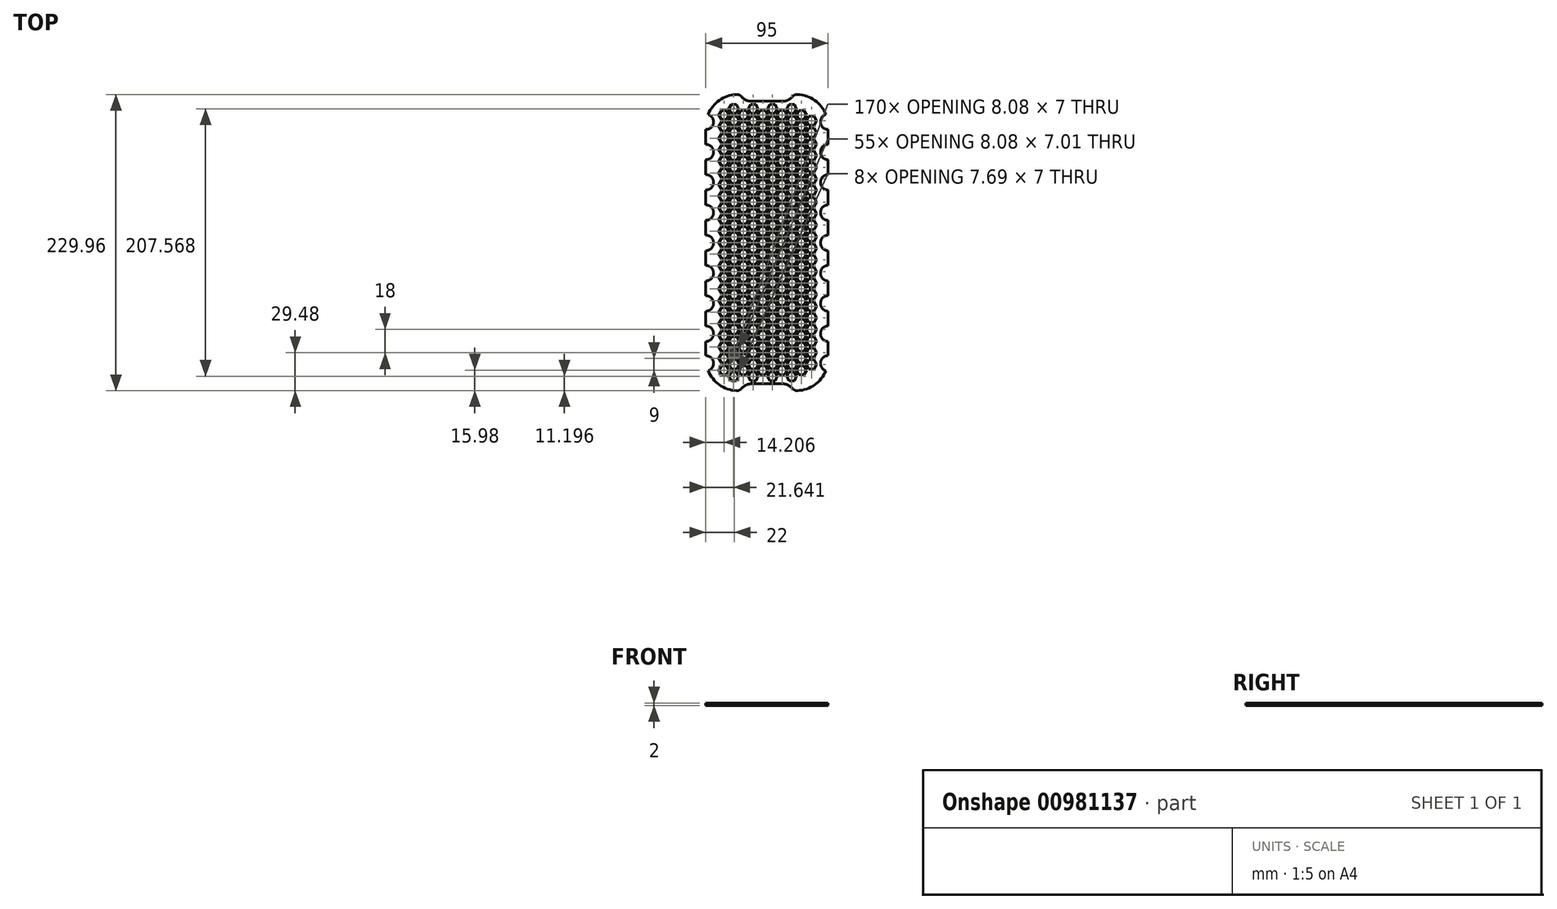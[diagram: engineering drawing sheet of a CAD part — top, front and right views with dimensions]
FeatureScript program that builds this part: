
annotation { "Feature Type Name" : "Feature", "Feature Type Description" : "" }
export const myFeature = defineFeature(function(context is Context, id is Id, definition is map)
    precondition{}
    {
        {
            var Q0;
            Q0=qCreatedBy(makeId("Top.planeOp"),FACE);
            var sketch = newSketch(context, id + "F0", { "sketchPlane" : qUnion([Q0])});
            skLineSegment(sketch, "E0.bottom", {"start": v(47.5, 115) * mm, "end": v(-47.5, 115) * mm});
            skLineSegment(sketch, "E0.top", {"start": v(47.5, -115) * mm, "end": v(-47.5, -115) * mm});
            skLineSegment(sketch, "E0.left", {"start": v(47.5, 115) * mm, "end": v(47.5, -115) * mm});
            skLineSegment(sketch, "E0.right", {"start": v(-47.5, 115) * mm, "end": v(-47.5, -115) * mm});
            skPoint(sketch, "E0.middle", {"position": v(0, 0) * mm});
            skSolve(sketch);
        }
        {
            var Q0;
            Q0 = qSketchRegion(id + "F0", true);
            extrude(context, id + "F1", {"entities" : qUnion([Q0]), "depth" : 2 * mm, "offsetDistance" : 25 * mm});
        }
        {
            var Q0;
            Q0=makeQuery(id+"F1.opExtrude","SWEPT_EDGE",EDGE,{"disambiguationData":[OSD([sQuery(id+"F0.wireOp",EDGE,"E0.top"),sQuery(id+"F0.wireOp",EDGE,"E0.right")])]});
            var Q1;
            Q1=makeQuery(id+"F1.opExtrude","SWEPT_EDGE",EDGE,{"disambiguationData":[OSD([sQuery(id+"F0.wireOp",EDGE,"E0.bottom"),sQuery(id+"F0.wireOp",EDGE,"E0.right")])]});
            var Q2;
            Q2=makeQuery(id+"F1.opExtrude","SWEPT_EDGE",EDGE,{"disambiguationData":[OSD([sQuery(id+"F0.wireOp",EDGE,"E0.bottom"),sQuery(id+"F0.wireOp",EDGE,"E0.left")])]});
            var Q3;
            Q3=makeQuery(id+"F1.opExtrude","SWEPT_EDGE",EDGE,{"disambiguationData":[OSD([sQuery(id+"F0.wireOp",EDGE,"E0.top"),sQuery(id+"F0.wireOp",EDGE,"E0.left")])]});
            fillet(context, id + "F2", {"entities" : qUnion([Q0, Q1, Q2, Q3]), "radius" : 25 * mm, "tangentPropagation" : true, "allowEdgeOverflow" : false});
        }
        {
            var Q0;
            Q0=qCreatedBy(makeId("Top.planeOp"),FACE);
            var sketch = newSketch(context, id + "F3", { "sketchPlane" : qUnion([Q0])});
            skCircle(sketch, "E1", {"center": v(-47.48, 93.75) * mm, "radius": 6 * mm});
            skCircle(sketch, "E2.MirrorC", {"center": v(47.48, 93.75) * mm, "radius": 6 * mm});
            skCircle(sketch, "E3.MirrorC", {"center": v(-47.48, -93.75) * mm, "radius": 6 * mm});
            skCircle(sketch, "E4.MirrorC", {"center": v(47.48, -93.75) * mm, "radius": 6 * mm});
            skCircle(sketch, "E5.0.1.0", {"center": v(-47.48, 70.25) * mm, "radius": 6 * mm});
            skLineSegment(sketch, "E5.direction1", {"start": v(-47.48, 93.75) * mm, "end": v(-47.48, 93.75) * mm});
            skLineSegment(sketch, "E5.direction2", {"start": v(-47.48, 93.75) * mm, "end": v(-47.48, 70.25) * mm, "construction": true});
            skCircle(sketch, "E6.0.0.2", {"center": v(-47.48, 46.75) * mm, "radius": 6 * mm});
            skCircle(sketch, "E6.0.0.3", {"center": v(-47.48, 23.25) * mm, "radius": 6 * mm});
            skCircle(sketch, "E7.0.0.4", {"center": v(-47.48, -0.25) * mm, "radius": 6 * mm});
            skCircle(sketch, "E8.0.0.5", {"center": v(-47.48, -23.75) * mm, "radius": 6 * mm});
            skCircle(sketch, "E9.0.0.6", {"center": v(-47.48, -47.25) * mm, "radius": 6 * mm});
            skCircle(sketch, "E10.MirrorC", {"center": v(47.48, 70.25) * mm, "radius": 6 * mm});
            skCircle(sketch, "E11.MirrorC", {"center": v(47.48, 46.75) * mm, "radius": 6 * mm});
            skCircle(sketch, "E12.MirrorC", {"center": v(47.48, 23.25) * mm, "radius": 6 * mm});
            skCircle(sketch, "E13.MirrorC", {"center": v(47.48, -0.25) * mm, "radius": 6 * mm});
            skCircle(sketch, "E14.MirrorC", {"center": v(47.48, -23.75) * mm, "radius": 6 * mm});
            skCircle(sketch, "E15.MirrorC", {"center": v(47.48, -47.25) * mm, "radius": 6 * mm});
            skCircle(sketch, "E16.MirrorC", {"center": v(47.48, -70.75) * mm, "radius": 6 * mm});
            skCircle(sketch, "E17.0.0.7", {"center": v(-47.48, -70.75) * mm, "radius": 6 * mm});
            skLineSegment(sketch, "E18.bottom", {"start": v(20.86, -109.66) * mm, "end": v(-20.86, -109.66) * mm});
            skLineSegment(sketch, "E18.top", {"start": v(20.86, -119.66) * mm, "end": v(-20.86, -119.66) * mm});
            skLineSegment(sketch, "E18.left", {"start": v(20.86, -109.66) * mm, "end": v(20.86, -119.66) * mm});
            skLineSegment(sketch, "E18.right", {"start": v(-20.86, -109.66) * mm, "end": v(-20.86, -119.66) * mm});
            skPoint(sketch, "E18.middle", {"position": v(0, -114.66) * mm});
            skLineSegment(sketch, "E19.MirrorCS", {"start": v(20.86, 119.66) * mm, "end": v(-20.86, 119.66) * mm});
            skLineSegment(sketch, "E20.MirrorCS", {"start": v(-20.86, 109.66) * mm, "end": v(-20.86, 119.66) * mm});
            skLineSegment(sketch, "E21.MirrorCS", {"start": v(20.86, 109.66) * mm, "end": v(-20.86, 109.66) * mm});
            skLineSegment(sketch, "E22.MirrorCS", {"start": v(20.86, 109.66) * mm, "end": v(20.86, 119.66) * mm});
            skSolve(sketch);
        }
        {
            var Q0;
            Q0 = qSketchRegion(id + "F3", true);
            extrude(context, id + "F4", {"entities" : qUnion([Q0]), "operationType" : NewBodyOperationType.REMOVE, "depth" : 10 * mm, "offsetDistance" : 25 * mm});
        }
        {
            var Q0;
            Q0=makeQuery(id+"F4.boolean.opBoolean","COPY",EDGE,{"derivedFrom":makeQuery(id+"F4.opExtrude","SWEPT_EDGE",EDGE,{"disambiguationData":[OSD([sQuery(id+"F3.wireOp",EDGE,"E18.bottom"),sQuery(id+"F3.wireOp",EDGE,"E18.right")])]})});
            var Q1;
            Q1=makeQuery(id+"F4.boolean.opBoolean","COPY",EDGE,{"derivedFrom":makeQuery(id+"F4.opExtrude","SWEPT_EDGE",EDGE,{"disambiguationData":[OSD([sQuery(id+"F3.wireOp",EDGE,"E18.bottom"),sQuery(id+"F3.wireOp",EDGE,"E18.left")])]})});
            var Q2;
            Q2=makeQuery(id+"F4.boolean.opBoolean","COPY",EDGE,{"derivedFrom":makeQuery(id+"F4.opExtrude","SWEPT_EDGE",EDGE,{"disambiguationData":[OSD([sQuery(id+"F3.wireOp",EDGE,"E20.MirrorCS"),sQuery(id+"F3.wireOp",EDGE,"E21.MirrorCS")])]})});
            var Q3;
            Q3=makeQuery(id+"F4.boolean.opBoolean","COPY",EDGE,{"derivedFrom":makeQuery(id+"F4.opExtrude","SWEPT_EDGE",EDGE,{"disambiguationData":[OSD([sQuery(id+"F3.wireOp",EDGE,"E21.MirrorCS"),sQuery(id+"F3.wireOp",EDGE,"E22.MirrorCS")])]})});
            fillet(context, id + "F5", {"entities" : qUnion([Q0, Q1, Q2, Q3]), "radius" : 10 * mm, "tangentPropagation" : true, "allowEdgeOverflow" : false});
        }
        {
            var Q0;
            {var subQ3=sQuery(id+"F0.wireOp",EDGE,"E0.bottom");var subQ4=sQuery(id+"F3.wireOp",EDGE,"E20.MirrorCS");Q0=makeQuery(id+"F5.opFillet","BLEND_EDGE",EDGE,{"blendedFrom":[makeQuery(id+"F4.boolean.opBoolean","COPY",EDGE,{"derivedFrom":makeQuery(id+"F4.opExtrude","SWEPT_EDGE",EDGE,{"disambiguationData":[OSD([subQ4,sQuery(id+"F3.wireOp",EDGE,"E21.MirrorCS")])]})}),makeQuery(id+"F4.boolean.opBoolean","SPLIT",FACE,{"disambiguationData":[TD([makeQuery(id+"F4.opExtrude","SWEPT_FACE",FACE,{"disambiguationData":[OSD([subQ4])]})])],"derivedFrom":makeQuery(id+"F1.opExtrude","SWEPT_FACE",FACE,{"disambiguationData":[OSD([subQ3])]})})],"blendedInto":[makeQuery(id+"F4.boolean.opBoolean","SPLIT",FACE,{"disambiguationData":[TD([makeQuery(id+"F4.opExtrude","SWEPT_FACE",FACE,{"disambiguationData":[OSD([subQ4])]})])],"derivedFrom":makeQuery(id+"F1.opExtrude","SWEPT_FACE",FACE,{"disambiguationData":[OSD([subQ3])]})})]});}
            var Q1;
            {var subQ3=sQuery(id+"F0.wireOp",EDGE,"E0.bottom");var subQ4=sQuery(id+"F3.wireOp",EDGE,"E22.MirrorCS");Q1=makeQuery(id+"F5.opFillet","BLEND_EDGE",EDGE,{"blendedFrom":[makeQuery(id+"F4.boolean.opBoolean","COPY",EDGE,{"derivedFrom":makeQuery(id+"F4.opExtrude","SWEPT_EDGE",EDGE,{"disambiguationData":[OSD([sQuery(id+"F3.wireOp",EDGE,"E21.MirrorCS"),subQ4])]})}),makeQuery(id+"F4.boolean.opBoolean","SPLIT",FACE,{"disambiguationData":[TD([makeQuery(id+"F4.opExtrude","SWEPT_FACE",FACE,{"disambiguationData":[OSD([subQ4])]})])],"derivedFrom":makeQuery(id+"F1.opExtrude","SWEPT_FACE",FACE,{"disambiguationData":[OSD([subQ3])]})})],"blendedInto":[makeQuery(id+"F4.boolean.opBoolean","SPLIT",FACE,{"disambiguationData":[TD([makeQuery(id+"F4.opExtrude","SWEPT_FACE",FACE,{"disambiguationData":[OSD([subQ4])]})])],"derivedFrom":makeQuery(id+"F1.opExtrude","SWEPT_FACE",FACE,{"disambiguationData":[OSD([subQ3])]})})]});}
            var Q2;
            {var subQ2=sQuery(id+"F0.wireOp",EDGE,"E0.top");var subQ4=sQuery(id+"F3.wireOp",EDGE,"E18.right");Q2=makeQuery(id+"F5.opFillet","BLEND_EDGE",EDGE,{"blendedFrom":[makeQuery(id+"F4.boolean.opBoolean","COPY",EDGE,{"derivedFrom":makeQuery(id+"F4.opExtrude","SWEPT_EDGE",EDGE,{"disambiguationData":[OSD([sQuery(id+"F3.wireOp",EDGE,"E18.bottom"),subQ4])]})}),makeQuery(id+"F4.boolean.opBoolean","SPLIT",FACE,{"disambiguationData":[TD([makeQuery(id+"F4.opExtrude","SWEPT_FACE",FACE,{"disambiguationData":[OSD([subQ4])]})])],"derivedFrom":makeQuery(id+"F1.opExtrude","SWEPT_FACE",FACE,{"disambiguationData":[OSD([subQ2])]})})],"blendedInto":[makeQuery(id+"F4.boolean.opBoolean","SPLIT",FACE,{"disambiguationData":[TD([makeQuery(id+"F4.opExtrude","SWEPT_FACE",FACE,{"disambiguationData":[OSD([subQ4])]})])],"derivedFrom":makeQuery(id+"F1.opExtrude","SWEPT_FACE",FACE,{"disambiguationData":[OSD([subQ2])]})})]});}
            var Q3;
            {var subQ2=sQuery(id+"F0.wireOp",EDGE,"E0.top");var subQ4=sQuery(id+"F3.wireOp",EDGE,"E18.left");Q3=makeQuery(id+"F5.opFillet","BLEND_EDGE",EDGE,{"blendedFrom":[makeQuery(id+"F4.boolean.opBoolean","COPY",EDGE,{"derivedFrom":makeQuery(id+"F4.opExtrude","SWEPT_EDGE",EDGE,{"disambiguationData":[OSD([sQuery(id+"F3.wireOp",EDGE,"E18.bottom"),subQ4])]})}),makeQuery(id+"F4.boolean.opBoolean","SPLIT",FACE,{"disambiguationData":[TD([makeQuery(id+"F4.opExtrude","SWEPT_FACE",FACE,{"disambiguationData":[OSD([subQ4])]})])],"derivedFrom":makeQuery(id+"F1.opExtrude","SWEPT_FACE",FACE,{"disambiguationData":[OSD([subQ2])]})})],"blendedInto":[makeQuery(id+"F4.boolean.opBoolean","SPLIT",FACE,{"disambiguationData":[TD([makeQuery(id+"F4.opExtrude","SWEPT_FACE",FACE,{"disambiguationData":[OSD([subQ4])]})])],"derivedFrom":makeQuery(id+"F1.opExtrude","SWEPT_FACE",FACE,{"disambiguationData":[OSD([subQ2])]})})]});}
            fillet(context, id + "F6", {"entities" : qUnion([Q0, Q1, Q2, Q3]), "radius" : 5 * mm, "tangentPropagation" : true, "allowEdgeOverflow" : false});
        }
        {
            var Q0;
            Q0=qCreatedBy(makeId("Top.planeOp"),FACE);
            var sketch = newSketch(context, id + "F7", { "sketchPlane" : qUnion([Q0])});
            skCircle(sketch, "E23.cCircle", {"center": v(34.5, -94.5) * mm, "radius": 3.5 * mm, "construction": true});
            skLineSegment(sketch, "E23.0", {"start": v(30.46, -94.5) * mm, "end": v(32.48, -91) * mm});
            skLineSegment(sketch, "E23.1", {"start": v(32.48, -91) * mm, "end": v(36.52, -91) * mm});
            skLineSegment(sketch, "E23.2", {"start": v(36.52, -91) * mm, "end": v(38.54, -94.5) * mm});
            skLineSegment(sketch, "E23.3", {"start": v(38.54, -94.5) * mm, "end": v(36.52, -98) * mm});
            skLineSegment(sketch, "E23.4", {"start": v(36.52, -98) * mm, "end": v(32.48, -98) * mm});
            skLineSegment(sketch, "E23.5", {"start": v(32.48, -98) * mm, "end": v(30.46, -94.5) * mm});
            skPoint(sketch, "E23.0.midPoint", {"position": v(31.47, -92.75) * mm});
            skCircle(sketch, "E24.cCircle", {"center": v(34.5, -85.5) * mm, "radius": 3.5 * mm, "construction": true});
            skLineSegment(sketch, "E24.0", {"start": v(30.46, -85.5) * mm, "end": v(32.47, -82) * mm});
            skLineSegment(sketch, "E24.1", {"start": v(32.47, -82) * mm, "end": v(36.51, -82) * mm});
            skLineSegment(sketch, "E24.2", {"start": v(36.51, -82) * mm, "end": v(38.54, -85.5) * mm});
            skLineSegment(sketch, "E24.3", {"start": v(38.54, -85.5) * mm, "end": v(36.53, -89) * mm});
            skLineSegment(sketch, "E24.4", {"start": v(36.53, -89) * mm, "end": v(32.49, -89) * mm});
            skLineSegment(sketch, "E24.5", {"start": v(32.49, -89) * mm, "end": v(30.46, -85.5) * mm});
            skPoint(sketch, "E24.0.midPoint", {"position": v(31.47, -83.76) * mm});
            skCircle(sketch, "E25.0.1.0", {"center": v(34.5, -76.5) * mm, "radius": 3.5 * mm, "construction": true});
            skPoint(sketch, "E25.0.1.1", {"position": v(31.47, -74.75) * mm});
            skLineSegment(sketch, "E25.0.1.2", {"start": v(36.52, -80) * mm, "end": v(32.48, -80) * mm});
            skCircle(sketch, "E25.0.1.3", {"center": v(34.5, -67.5) * mm, "radius": 3.5 * mm, "construction": true});
            skPoint(sketch, "E25.0.1.4", {"position": v(31.47, -65.76) * mm});
            skLineSegment(sketch, "E25.0.1.5", {"start": v(32.49, -71) * mm, "end": v(30.46, -67.5) * mm});
            skLineSegment(sketch, "E25.0.1.6", {"start": v(32.47, -64) * mm, "end": v(36.51, -64) * mm});
            skLineSegment(sketch, "E25.0.1.7", {"start": v(36.53, -71) * mm, "end": v(32.49, -71) * mm});
            skLineSegment(sketch, "E25.0.1.8", {"start": v(36.52, -73) * mm, "end": v(38.54, -76.5) * mm});
            skLineSegment(sketch, "E25.0.1.9", {"start": v(30.46, -76.5) * mm, "end": v(32.48, -73) * mm});
            skLineSegment(sketch, "E25.0.1.10", {"start": v(36.51, -64) * mm, "end": v(38.54, -67.5) * mm});
            skLineSegment(sketch, "E25.0.1.11", {"start": v(30.46, -67.5) * mm, "end": v(32.47, -64) * mm});
            skLineSegment(sketch, "E25.0.1.12", {"start": v(32.48, -80) * mm, "end": v(30.46, -76.5) * mm});
            skLineSegment(sketch, "E25.0.1.13", {"start": v(38.54, -76.5) * mm, "end": v(36.52, -80) * mm});
            skLineSegment(sketch, "E25.0.1.14", {"start": v(38.54, -67.5) * mm, "end": v(36.53, -71) * mm});
            skLineSegment(sketch, "E25.0.1.15", {"start": v(32.48, -73) * mm, "end": v(36.52, -73) * mm});
            skCircle(sketch, "E25.0.2.0", {"center": v(34.5, -58.5) * mm, "radius": 3.5 * mm, "construction": true});
            skPoint(sketch, "E25.0.2.1", {"position": v(31.47, -56.75) * mm});
            skLineSegment(sketch, "E25.0.2.2", {"start": v(36.52, -62) * mm, "end": v(32.48, -62) * mm});
            skCircle(sketch, "E25.0.2.3", {"center": v(34.5, -49.5) * mm, "radius": 3.5 * mm, "construction": true});
            skPoint(sketch, "E25.0.2.4", {"position": v(31.47, -47.76) * mm});
            skLineSegment(sketch, "E25.0.2.5", {"start": v(32.49, -53) * mm, "end": v(30.46, -49.5) * mm});
            skLineSegment(sketch, "E25.0.2.6", {"start": v(32.47, -46) * mm, "end": v(36.51, -46) * mm});
            skLineSegment(sketch, "E25.0.2.7", {"start": v(36.53, -53) * mm, "end": v(32.49, -53) * mm});
            skLineSegment(sketch, "E25.0.2.8", {"start": v(36.52, -55) * mm, "end": v(38.54, -58.5) * mm});
            skLineSegment(sketch, "E25.0.2.9", {"start": v(30.46, -58.5) * mm, "end": v(32.48, -55) * mm});
            skLineSegment(sketch, "E25.0.2.10", {"start": v(36.51, -46) * mm, "end": v(38.54, -49.5) * mm});
            skLineSegment(sketch, "E25.0.2.11", {"start": v(30.46, -49.5) * mm, "end": v(32.47, -46) * mm});
            skLineSegment(sketch, "E25.0.2.12", {"start": v(32.48, -62) * mm, "end": v(30.46, -58.5) * mm});
            skLineSegment(sketch, "E25.0.2.13", {"start": v(38.54, -58.5) * mm, "end": v(36.52, -62) * mm});
            skLineSegment(sketch, "E25.0.2.14", {"start": v(38.54, -49.5) * mm, "end": v(36.53, -53) * mm});
            skLineSegment(sketch, "E25.0.2.15", {"start": v(32.48, -55) * mm, "end": v(36.52, -55) * mm});
            skCircle(sketch, "E25.0.3.0", {"center": v(34.5, -40.5) * mm, "radius": 3.5 * mm, "construction": true});
            skPoint(sketch, "E25.0.3.1", {"position": v(31.47, -38.75) * mm});
            skLineSegment(sketch, "E25.0.3.2", {"start": v(36.52, -44) * mm, "end": v(32.48, -44) * mm});
            skCircle(sketch, "E25.0.3.3", {"center": v(34.5, -31.5) * mm, "radius": 3.5 * mm, "construction": true});
            skPoint(sketch, "E25.0.3.4", {"position": v(31.47, -29.76) * mm});
            skLineSegment(sketch, "E25.0.3.5", {"start": v(32.49, -35) * mm, "end": v(30.46, -31.5) * mm});
            skLineSegment(sketch, "E25.0.3.6", {"start": v(32.47, -28) * mm, "end": v(36.51, -28) * mm});
            skLineSegment(sketch, "E25.0.3.7", {"start": v(36.53, -35) * mm, "end": v(32.49, -35) * mm});
            skLineSegment(sketch, "E25.0.3.8", {"start": v(36.52, -37) * mm, "end": v(38.54, -40.5) * mm});
            skLineSegment(sketch, "E25.0.3.9", {"start": v(30.46, -40.5) * mm, "end": v(32.48, -37) * mm});
            skLineSegment(sketch, "E25.0.3.10", {"start": v(36.51, -28) * mm, "end": v(38.54, -31.5) * mm});
            skLineSegment(sketch, "E25.0.3.11", {"start": v(30.46, -31.5) * mm, "end": v(32.47, -28) * mm});
            skLineSegment(sketch, "E25.0.3.12", {"start": v(32.48, -44) * mm, "end": v(30.46, -40.5) * mm});
            skLineSegment(sketch, "E25.0.3.13", {"start": v(38.54, -40.5) * mm, "end": v(36.52, -44) * mm});
            skLineSegment(sketch, "E25.0.3.14", {"start": v(38.54, -31.5) * mm, "end": v(36.53, -35) * mm});
            skLineSegment(sketch, "E25.0.3.15", {"start": v(32.48, -37) * mm, "end": v(36.52, -37) * mm});
            skCircle(sketch, "E25.0.4.0", {"center": v(34.5, -22.5) * mm, "radius": 3.5 * mm, "construction": true});
            skPoint(sketch, "E25.0.4.1", {"position": v(31.47, -20.75) * mm});
            skLineSegment(sketch, "E25.0.4.2", {"start": v(36.52, -26) * mm, "end": v(32.48, -26) * mm});
            skCircle(sketch, "E25.0.4.3", {"center": v(34.5, -13.5) * mm, "radius": 3.5 * mm, "construction": true});
            skPoint(sketch, "E25.0.4.4", {"position": v(31.47, -11.76) * mm});
            skLineSegment(sketch, "E25.0.4.5", {"start": v(32.49, -17) * mm, "end": v(30.46, -13.5) * mm});
            skLineSegment(sketch, "E25.0.4.6", {"start": v(32.47, -10) * mm, "end": v(36.51, -10) * mm});
            skLineSegment(sketch, "E25.0.4.7", {"start": v(36.53, -17) * mm, "end": v(32.49, -17) * mm});
            skLineSegment(sketch, "E25.0.4.8", {"start": v(36.52, -19) * mm, "end": v(38.54, -22.5) * mm});
            skLineSegment(sketch, "E25.0.4.9", {"start": v(30.46, -22.5) * mm, "end": v(32.48, -19) * mm});
            skLineSegment(sketch, "E25.0.4.10", {"start": v(36.51, -10) * mm, "end": v(38.54, -13.5) * mm});
            skLineSegment(sketch, "E25.0.4.11", {"start": v(30.46, -13.5) * mm, "end": v(32.47, -10) * mm});
            skLineSegment(sketch, "E25.0.4.12", {"start": v(32.48, -26) * mm, "end": v(30.46, -22.5) * mm});
            skLineSegment(sketch, "E25.0.4.13", {"start": v(38.54, -22.5) * mm, "end": v(36.52, -26) * mm});
            skLineSegment(sketch, "E25.0.4.14", {"start": v(38.54, -13.5) * mm, "end": v(36.53, -17) * mm});
            skLineSegment(sketch, "E25.0.4.15", {"start": v(32.48, -19) * mm, "end": v(36.52, -19) * mm});
            skCircle(sketch, "E25.0.5.0", {"center": v(34.5, -4.5) * mm, "radius": 3.5 * mm, "construction": true});
            skPoint(sketch, "E25.0.5.1", {"position": v(31.47, -2.75) * mm});
            skLineSegment(sketch, "E25.0.5.2", {"start": v(36.52, -8) * mm, "end": v(32.48, -8) * mm});
            skCircle(sketch, "E25.0.5.3", {"center": v(34.5, 4.5) * mm, "radius": 3.5 * mm, "construction": true});
            skPoint(sketch, "E25.0.5.4", {"position": v(31.47, 6.24) * mm});
            skLineSegment(sketch, "E25.0.5.5", {"start": v(32.49, 1) * mm, "end": v(30.46, 4.5) * mm});
            skLineSegment(sketch, "E25.0.5.6", {"start": v(32.47, 8) * mm, "end": v(36.51, 8) * mm});
            skLineSegment(sketch, "E25.0.5.7", {"start": v(36.53, 1) * mm, "end": v(32.49, 1) * mm});
            skLineSegment(sketch, "E25.0.5.8", {"start": v(36.52, -1) * mm, "end": v(38.54, -4.5) * mm});
            skLineSegment(sketch, "E25.0.5.9", {"start": v(30.46, -4.5) * mm, "end": v(32.48, -1) * mm});
            skLineSegment(sketch, "E25.0.5.10", {"start": v(36.51, 8) * mm, "end": v(38.54, 4.5) * mm});
            skLineSegment(sketch, "E25.0.5.11", {"start": v(30.46, 4.5) * mm, "end": v(32.47, 8) * mm});
            skLineSegment(sketch, "E25.0.5.12", {"start": v(32.48, -8) * mm, "end": v(30.46, -4.5) * mm});
            skLineSegment(sketch, "E25.0.5.13", {"start": v(38.54, -4.5) * mm, "end": v(36.52, -8) * mm});
            skLineSegment(sketch, "E25.0.5.14", {"start": v(38.54, 4.5) * mm, "end": v(36.53, 1) * mm});
            skLineSegment(sketch, "E25.0.5.15", {"start": v(32.48, -1) * mm, "end": v(36.52, -1) * mm});
            skCircle(sketch, "E25.0.6.0", {"center": v(34.5, 13.5) * mm, "radius": 3.5 * mm, "construction": true});
            skPoint(sketch, "E25.0.6.1", {"position": v(31.47, 15.25) * mm});
            skLineSegment(sketch, "E25.0.6.2", {"start": v(36.52, 10) * mm, "end": v(32.48, 10) * mm});
            skCircle(sketch, "E25.0.6.3", {"center": v(34.5, 22.5) * mm, "radius": 3.5 * mm, "construction": true});
            skPoint(sketch, "E25.0.6.4", {"position": v(31.47, 24.24) * mm});
            skLineSegment(sketch, "E25.0.6.5", {"start": v(32.49, 19) * mm, "end": v(30.46, 22.5) * mm});
            skLineSegment(sketch, "E25.0.6.6", {"start": v(32.47, 26) * mm, "end": v(36.51, 26) * mm});
            skLineSegment(sketch, "E25.0.6.7", {"start": v(36.53, 19) * mm, "end": v(32.49, 19) * mm});
            skLineSegment(sketch, "E25.0.6.8", {"start": v(36.52, 17) * mm, "end": v(38.54, 13.5) * mm});
            skLineSegment(sketch, "E25.0.6.9", {"start": v(30.46, 13.5) * mm, "end": v(32.48, 17) * mm});
            skLineSegment(sketch, "E25.0.6.10", {"start": v(36.51, 26) * mm, "end": v(38.54, 22.5) * mm});
            skLineSegment(sketch, "E25.0.6.11", {"start": v(30.46, 22.5) * mm, "end": v(32.47, 26) * mm});
            skLineSegment(sketch, "E25.0.6.12", {"start": v(32.48, 10) * mm, "end": v(30.46, 13.5) * mm});
            skLineSegment(sketch, "E25.0.6.13", {"start": v(38.54, 13.5) * mm, "end": v(36.52, 10) * mm});
            skLineSegment(sketch, "E25.0.6.14", {"start": v(38.54, 22.5) * mm, "end": v(36.53, 19) * mm});
            skLineSegment(sketch, "E25.0.6.15", {"start": v(32.48, 17) * mm, "end": v(36.52, 17) * mm});
            skCircle(sketch, "E25.0.7.0", {"center": v(34.5, 31.5) * mm, "radius": 3.5 * mm, "construction": true});
            skPoint(sketch, "E25.0.7.1", {"position": v(31.47, 33.25) * mm});
            skLineSegment(sketch, "E25.0.7.2", {"start": v(36.52, 28) * mm, "end": v(32.48, 28) * mm});
            skCircle(sketch, "E25.0.7.3", {"center": v(34.5, 40.5) * mm, "radius": 3.5 * mm, "construction": true});
            skPoint(sketch, "E25.0.7.4", {"position": v(31.47, 42.24) * mm});
            skLineSegment(sketch, "E25.0.7.5", {"start": v(32.49, 37) * mm, "end": v(30.46, 40.5) * mm});
            skLineSegment(sketch, "E25.0.7.6", {"start": v(32.47, 44) * mm, "end": v(36.51, 44) * mm});
            skLineSegment(sketch, "E25.0.7.7", {"start": v(36.53, 37) * mm, "end": v(32.49, 37) * mm});
            skLineSegment(sketch, "E25.0.7.8", {"start": v(36.52, 35) * mm, "end": v(38.54, 31.5) * mm});
            skLineSegment(sketch, "E25.0.7.9", {"start": v(30.46, 31.5) * mm, "end": v(32.48, 35) * mm});
            skLineSegment(sketch, "E25.0.7.10", {"start": v(36.51, 44) * mm, "end": v(38.54, 40.5) * mm});
            skLineSegment(sketch, "E25.0.7.11", {"start": v(30.46, 40.5) * mm, "end": v(32.47, 44) * mm});
            skLineSegment(sketch, "E25.0.7.12", {"start": v(32.48, 28) * mm, "end": v(30.46, 31.5) * mm});
            skLineSegment(sketch, "E25.0.7.13", {"start": v(38.54, 31.5) * mm, "end": v(36.52, 28) * mm});
            skLineSegment(sketch, "E25.0.7.14", {"start": v(38.54, 40.5) * mm, "end": v(36.53, 37) * mm});
            skLineSegment(sketch, "E25.0.7.15", {"start": v(32.48, 35) * mm, "end": v(36.52, 35) * mm});
            skCircle(sketch, "E25.0.8.0", {"center": v(34.5, 49.5) * mm, "radius": 3.5 * mm, "construction": true});
            skPoint(sketch, "E25.0.8.1", {"position": v(31.47, 51.25) * mm});
            skLineSegment(sketch, "E25.0.8.2", {"start": v(36.52, 46) * mm, "end": v(32.48, 46) * mm});
            skCircle(sketch, "E25.0.8.3", {"center": v(34.5, 58.5) * mm, "radius": 3.5 * mm, "construction": true});
            skPoint(sketch, "E25.0.8.4", {"position": v(31.47, 60.24) * mm});
            skLineSegment(sketch, "E25.0.8.5", {"start": v(32.49, 55) * mm, "end": v(30.46, 58.5) * mm});
            skLineSegment(sketch, "E25.0.8.6", {"start": v(32.47, 62) * mm, "end": v(36.51, 62) * mm});
            skLineSegment(sketch, "E25.0.8.7", {"start": v(36.53, 55) * mm, "end": v(32.49, 55) * mm});
            skLineSegment(sketch, "E25.0.8.8", {"start": v(36.52, 53) * mm, "end": v(38.54, 49.5) * mm});
            skLineSegment(sketch, "E25.0.8.9", {"start": v(30.46, 49.5) * mm, "end": v(32.48, 53) * mm});
            skLineSegment(sketch, "E25.0.8.10", {"start": v(36.51, 62) * mm, "end": v(38.54, 58.5) * mm});
            skLineSegment(sketch, "E25.0.8.11", {"start": v(30.46, 58.5) * mm, "end": v(32.47, 62) * mm});
            skLineSegment(sketch, "E25.0.8.12", {"start": v(32.48, 46) * mm, "end": v(30.46, 49.5) * mm});
            skLineSegment(sketch, "E25.0.8.13", {"start": v(38.54, 49.5) * mm, "end": v(36.52, 46) * mm});
            skLineSegment(sketch, "E25.0.8.14", {"start": v(38.54, 58.5) * mm, "end": v(36.53, 55) * mm});
            skLineSegment(sketch, "E25.0.8.15", {"start": v(32.48, 53) * mm, "end": v(36.52, 53) * mm});
            skCircle(sketch, "E25.0.9.0", {"center": v(34.5, 67.5) * mm, "radius": 3.5 * mm, "construction": true});
            skPoint(sketch, "E25.0.9.1", {"position": v(31.47, 69.25) * mm});
            skLineSegment(sketch, "E25.0.9.2", {"start": v(36.52, 64) * mm, "end": v(32.48, 64) * mm});
            skCircle(sketch, "E25.0.9.3", {"center": v(34.5, 76.5) * mm, "radius": 3.5 * mm, "construction": true});
            skPoint(sketch, "E25.0.9.4", {"position": v(31.47, 78.24) * mm});
            skLineSegment(sketch, "E25.0.9.5", {"start": v(32.49, 73) * mm, "end": v(30.46, 76.5) * mm});
            skLineSegment(sketch, "E25.0.9.6", {"start": v(32.47, 80) * mm, "end": v(36.51, 80) * mm});
            skLineSegment(sketch, "E25.0.9.7", {"start": v(36.53, 73) * mm, "end": v(32.49, 73) * mm});
            skLineSegment(sketch, "E25.0.9.8", {"start": v(36.52, 71) * mm, "end": v(38.54, 67.5) * mm});
            skLineSegment(sketch, "E25.0.9.9", {"start": v(30.46, 67.5) * mm, "end": v(32.48, 71) * mm});
            skLineSegment(sketch, "E25.0.9.10", {"start": v(36.51, 80) * mm, "end": v(38.54, 76.5) * mm});
            skLineSegment(sketch, "E25.0.9.11", {"start": v(30.46, 76.5) * mm, "end": v(32.47, 80) * mm});
            skLineSegment(sketch, "E25.0.9.12", {"start": v(32.48, 64) * mm, "end": v(30.46, 67.5) * mm});
            skLineSegment(sketch, "E25.0.9.13", {"start": v(38.54, 67.5) * mm, "end": v(36.52, 64) * mm});
            skLineSegment(sketch, "E25.0.9.14", {"start": v(38.54, 76.5) * mm, "end": v(36.53, 73) * mm});
            skLineSegment(sketch, "E25.0.9.15", {"start": v(32.48, 71) * mm, "end": v(36.52, 71) * mm});
            skCircle(sketch, "E25.0.10.0", {"center": v(34.5, 85.5) * mm, "radius": 3.5 * mm, "construction": true});
            skPoint(sketch, "E25.0.10.1", {"position": v(31.47, 87.25) * mm});
            skLineSegment(sketch, "E25.0.10.2", {"start": v(36.52, 82) * mm, "end": v(32.48, 82) * mm});
            skCircle(sketch, "E25.0.10.3", {"center": v(34.5, 94.5) * mm, "radius": 3.5 * mm, "construction": true});
            skPoint(sketch, "E25.0.10.4", {"position": v(31.47, 96.24) * mm});
            skLineSegment(sketch, "E25.0.10.5", {"start": v(32.49, 91) * mm, "end": v(30.46, 94.5) * mm});
            skLineSegment(sketch, "E25.0.10.6", {"start": v(32.47, 98) * mm, "end": v(36.51, 98) * mm});
            skLineSegment(sketch, "E25.0.10.7", {"start": v(36.53, 91) * mm, "end": v(32.49, 91) * mm});
            skLineSegment(sketch, "E25.0.10.8", {"start": v(36.52, 89) * mm, "end": v(38.54, 85.5) * mm});
            skLineSegment(sketch, "E25.0.10.9", {"start": v(30.46, 85.5) * mm, "end": v(32.48, 89) * mm});
            skLineSegment(sketch, "E25.0.10.10", {"start": v(36.51, 98) * mm, "end": v(38.54, 94.5) * mm});
            skLineSegment(sketch, "E25.0.10.11", {"start": v(30.46, 94.5) * mm, "end": v(32.47, 98) * mm});
            skLineSegment(sketch, "E25.0.10.12", {"start": v(32.48, 82) * mm, "end": v(30.46, 85.5) * mm});
            skLineSegment(sketch, "E25.0.10.13", {"start": v(38.54, 85.5) * mm, "end": v(36.52, 82) * mm});
            skLineSegment(sketch, "E25.0.10.14", {"start": v(38.54, 94.5) * mm, "end": v(36.53, 91) * mm});
            skLineSegment(sketch, "E25.0.10.15", {"start": v(32.48, 89) * mm, "end": v(36.52, 89) * mm});
            skLineSegment(sketch, "E25.direction1", {"start": v(32.48, -98) * mm, "end": v(57.3, -98) * mm, "construction": true});
            skLineSegment(sketch, "E25.direction2", {"start": v(32.48, -98) * mm, "end": v(32.48, -80) * mm, "construction": true});
            skCircle(sketch, "E26.cCircle", {"center": v(26.7, -99) * mm, "radius": 3.5 * mm, "construction": true});
            skLineSegment(sketch, "E26.0", {"start": v(24.69, -95.5) * mm, "end": v(28.73, -95.5) * mm});
            skLineSegment(sketch, "E26.1", {"start": v(28.73, -95.5) * mm, "end": v(30.75, -99) * mm});
            skLineSegment(sketch, "E26.2", {"start": v(30.75, -99) * mm, "end": v(28.73, -102.5) * mm});
            skLineSegment(sketch, "E26.3", {"start": v(28.73, -102.5) * mm, "end": v(24.69, -102.5) * mm});
            skLineSegment(sketch, "E26.4", {"start": v(24.69, -102.5) * mm, "end": v(22.66, -99) * mm});
            skLineSegment(sketch, "E26.5", {"start": v(22.66, -99) * mm, "end": v(24.69, -95.5) * mm});
            skPoint(sketch, "E26.0.midPoint", {"position": v(26.7, -95.5) * mm});
            skLineSegment(sketch, "E27.0.1.0", {"start": v(30.75, -90) * mm, "end": v(28.73, -93.5) * mm});
            skLineSegment(sketch, "E27.0.1.1", {"start": v(28.73, -93.5) * mm, "end": v(24.69, -93.5) * mm});
            skLineSegment(sketch, "E27.0.1.2", {"start": v(24.69, -86.5) * mm, "end": v(28.73, -86.5) * mm});
            skLineSegment(sketch, "E27.0.1.3", {"start": v(22.66, -90) * mm, "end": v(24.69, -86.5) * mm});
            skLineSegment(sketch, "E27.0.1.4", {"start": v(24.69, -93.5) * mm, "end": v(22.66, -90) * mm});
            skLineSegment(sketch, "E27.0.1.5", {"start": v(28.73, -86.5) * mm, "end": v(30.75, -90) * mm});
            skCircle(sketch, "E27.0.1.6", {"center": v(26.7, -90) * mm, "radius": 3.5 * mm, "construction": true});
            skLineSegment(sketch, "E27.0.2.0", {"start": v(30.75, -81) * mm, "end": v(28.73, -84.5) * mm});
            skLineSegment(sketch, "E27.0.2.1", {"start": v(28.73, -84.5) * mm, "end": v(24.69, -84.5) * mm});
            skLineSegment(sketch, "E27.0.2.2", {"start": v(24.69, -77.5) * mm, "end": v(28.73, -77.5) * mm});
            skLineSegment(sketch, "E27.0.2.3", {"start": v(22.66, -81) * mm, "end": v(24.69, -77.5) * mm});
            skLineSegment(sketch, "E27.0.2.4", {"start": v(24.69, -84.5) * mm, "end": v(22.66, -81) * mm});
            skLineSegment(sketch, "E27.0.2.5", {"start": v(28.73, -77.5) * mm, "end": v(30.75, -81) * mm});
            skCircle(sketch, "E27.0.2.6", {"center": v(26.7, -81) * mm, "radius": 3.5 * mm, "construction": true});
            skLineSegment(sketch, "E27.0.3.0", {"start": v(30.75, -72) * mm, "end": v(28.73, -75.5) * mm});
            skLineSegment(sketch, "E27.0.3.1", {"start": v(28.73, -75.5) * mm, "end": v(24.69, -75.5) * mm});
            skLineSegment(sketch, "E27.0.3.2", {"start": v(24.69, -68.5) * mm, "end": v(28.73, -68.5) * mm});
            skLineSegment(sketch, "E27.0.3.3", {"start": v(22.66, -72) * mm, "end": v(24.69, -68.5) * mm});
            skLineSegment(sketch, "E27.0.3.4", {"start": v(24.69, -75.5) * mm, "end": v(22.66, -72) * mm});
            skLineSegment(sketch, "E27.0.3.5", {"start": v(28.73, -68.5) * mm, "end": v(30.75, -72) * mm});
            skCircle(sketch, "E27.0.3.6", {"center": v(26.7, -72) * mm, "radius": 3.5 * mm, "construction": true});
            skLineSegment(sketch, "E27.0.4.0", {"start": v(30.75, -63) * mm, "end": v(28.73, -66.5) * mm});
            skLineSegment(sketch, "E27.0.4.1", {"start": v(28.73, -66.5) * mm, "end": v(24.69, -66.5) * mm});
            skLineSegment(sketch, "E27.0.4.2", {"start": v(24.69, -59.5) * mm, "end": v(28.73, -59.5) * mm});
            skLineSegment(sketch, "E27.0.4.3", {"start": v(22.66, -63) * mm, "end": v(24.69, -59.5) * mm});
            skLineSegment(sketch, "E27.0.4.4", {"start": v(24.69, -66.5) * mm, "end": v(22.66, -63) * mm});
            skLineSegment(sketch, "E27.0.4.5", {"start": v(28.73, -59.5) * mm, "end": v(30.75, -63) * mm});
            skCircle(sketch, "E27.0.4.6", {"center": v(26.7, -63) * mm, "radius": 3.5 * mm, "construction": true});
            skLineSegment(sketch, "E27.0.5.0", {"start": v(30.75, -54) * mm, "end": v(28.73, -57.5) * mm});
            skLineSegment(sketch, "E27.0.5.1", {"start": v(28.73, -57.5) * mm, "end": v(24.69, -57.5) * mm});
            skLineSegment(sketch, "E27.0.5.2", {"start": v(24.69, -50.5) * mm, "end": v(28.73, -50.5) * mm});
            skLineSegment(sketch, "E27.0.5.3", {"start": v(22.66, -54) * mm, "end": v(24.69, -50.5) * mm});
            skLineSegment(sketch, "E27.0.5.4", {"start": v(24.69, -57.5) * mm, "end": v(22.66, -54) * mm});
            skLineSegment(sketch, "E27.0.5.5", {"start": v(28.73, -50.5) * mm, "end": v(30.75, -54) * mm});
            skCircle(sketch, "E27.0.5.6", {"center": v(26.7, -54) * mm, "radius": 3.5 * mm, "construction": true});
            skLineSegment(sketch, "E27.0.6.0", {"start": v(30.75, -45) * mm, "end": v(28.73, -48.5) * mm});
            skLineSegment(sketch, "E27.0.6.1", {"start": v(28.73, -48.5) * mm, "end": v(24.69, -48.5) * mm});
            skLineSegment(sketch, "E27.0.6.2", {"start": v(24.69, -41.5) * mm, "end": v(28.73, -41.5) * mm});
            skLineSegment(sketch, "E27.0.6.3", {"start": v(22.66, -45) * mm, "end": v(24.69, -41.5) * mm});
            skLineSegment(sketch, "E27.0.6.4", {"start": v(24.69, -48.5) * mm, "end": v(22.66, -45) * mm});
            skLineSegment(sketch, "E27.0.6.5", {"start": v(28.73, -41.5) * mm, "end": v(30.75, -45) * mm});
            skCircle(sketch, "E27.0.6.6", {"center": v(26.7, -45) * mm, "radius": 3.5 * mm, "construction": true});
            skLineSegment(sketch, "E27.0.7.0", {"start": v(30.75, -36) * mm, "end": v(28.73, -39.5) * mm});
            skLineSegment(sketch, "E27.0.7.1", {"start": v(28.73, -39.5) * mm, "end": v(24.69, -39.5) * mm});
            skLineSegment(sketch, "E27.0.7.2", {"start": v(24.69, -32.5) * mm, "end": v(28.73, -32.5) * mm});
            skLineSegment(sketch, "E27.0.7.3", {"start": v(22.66, -36) * mm, "end": v(24.69, -32.5) * mm});
            skLineSegment(sketch, "E27.0.7.4", {"start": v(24.69, -39.5) * mm, "end": v(22.66, -36) * mm});
            skLineSegment(sketch, "E27.0.7.5", {"start": v(28.73, -32.5) * mm, "end": v(30.75, -36) * mm});
            skCircle(sketch, "E27.0.7.6", {"center": v(26.7, -36) * mm, "radius": 3.5 * mm, "construction": true});
            skLineSegment(sketch, "E27.0.8.0", {"start": v(30.75, -27) * mm, "end": v(28.73, -30.5) * mm});
            skLineSegment(sketch, "E27.0.8.1", {"start": v(28.73, -30.5) * mm, "end": v(24.69, -30.5) * mm});
            skLineSegment(sketch, "E27.0.8.2", {"start": v(24.69, -23.5) * mm, "end": v(28.73, -23.5) * mm});
            skLineSegment(sketch, "E27.0.8.3", {"start": v(22.66, -27) * mm, "end": v(24.69, -23.5) * mm});
            skLineSegment(sketch, "E27.0.8.4", {"start": v(24.69, -30.5) * mm, "end": v(22.66, -27) * mm});
            skLineSegment(sketch, "E27.0.8.5", {"start": v(28.73, -23.5) * mm, "end": v(30.75, -27) * mm});
            skCircle(sketch, "E27.0.8.6", {"center": v(26.7, -27) * mm, "radius": 3.5 * mm, "construction": true});
            skLineSegment(sketch, "E27.0.9.0", {"start": v(30.75, -18) * mm, "end": v(28.73, -21.5) * mm});
            skLineSegment(sketch, "E27.0.9.1", {"start": v(28.73, -21.5) * mm, "end": v(24.69, -21.5) * mm});
            skLineSegment(sketch, "E27.0.9.2", {"start": v(24.69, -14.5) * mm, "end": v(28.73, -14.5) * mm});
            skLineSegment(sketch, "E27.0.9.3", {"start": v(22.66, -18) * mm, "end": v(24.69, -14.5) * mm});
            skLineSegment(sketch, "E27.0.9.4", {"start": v(24.69, -21.5) * mm, "end": v(22.66, -18) * mm});
            skLineSegment(sketch, "E27.0.9.5", {"start": v(28.73, -14.5) * mm, "end": v(30.75, -18) * mm});
            skCircle(sketch, "E27.0.9.6", {"center": v(26.7, -18) * mm, "radius": 3.5 * mm, "construction": true});
            skLineSegment(sketch, "E27.0.10.0", {"start": v(30.75, -9) * mm, "end": v(28.73, -12.5) * mm});
            skLineSegment(sketch, "E27.0.10.1", {"start": v(28.73, -12.5) * mm, "end": v(24.69, -12.5) * mm});
            skLineSegment(sketch, "E27.0.10.2", {"start": v(24.69, -5.5) * mm, "end": v(28.73, -5.5) * mm});
            skLineSegment(sketch, "E27.0.10.3", {"start": v(22.66, -9) * mm, "end": v(24.69, -5.5) * mm});
            skLineSegment(sketch, "E27.0.10.4", {"start": v(24.69, -12.5) * mm, "end": v(22.66, -9) * mm});
            skLineSegment(sketch, "E27.0.10.5", {"start": v(28.73, -5.5) * mm, "end": v(30.75, -9) * mm});
            skCircle(sketch, "E27.0.10.6", {"center": v(26.7, -9) * mm, "radius": 3.5 * mm, "construction": true});
            skLineSegment(sketch, "E27.0.11.0", {"start": v(30.75, 0) * mm, "end": v(28.73, -3.5) * mm});
            skLineSegment(sketch, "E27.0.11.1", {"start": v(28.73, -3.5) * mm, "end": v(24.69, -3.5) * mm});
            skLineSegment(sketch, "E27.0.11.2", {"start": v(24.69, 3.5) * mm, "end": v(28.73, 3.5) * mm});
            skLineSegment(sketch, "E27.0.11.3", {"start": v(22.66, 0) * mm, "end": v(24.69, 3.5) * mm});
            skLineSegment(sketch, "E27.0.11.4", {"start": v(24.69, -3.5) * mm, "end": v(22.66, 0) * mm});
            skLineSegment(sketch, "E27.0.11.5", {"start": v(28.73, 3.5) * mm, "end": v(30.75, 0) * mm});
            skCircle(sketch, "E27.0.11.6", {"center": v(26.7, 0) * mm, "radius": 3.5 * mm, "construction": true});
            skLineSegment(sketch, "E27.direction1", {"start": v(24.69, -102.5) * mm, "end": v(49.69, -102.5) * mm, "construction": true});
            skLineSegment(sketch, "E27.direction2", {"start": v(24.69, -102.5) * mm, "end": v(24.69, -93.5) * mm, "construction": true});
            skLineSegment(sketch, "E28.0.0.12", {"start": v(30.75, 9) * mm, "end": v(28.73, 5.5) * mm});
            skLineSegment(sketch, "E28.3.0.12", {"start": v(28.73, 5.5) * mm, "end": v(24.69, 5.5) * mm});
            skLineSegment(sketch, "E28.6.0.12", {"start": v(24.69, 12.5) * mm, "end": v(28.73, 12.5) * mm});
            skLineSegment(sketch, "E28.9.0.12", {"start": v(22.66, 9) * mm, "end": v(24.69, 12.5) * mm});
            skLineSegment(sketch, "E28.12.0.12", {"start": v(24.69, 5.5) * mm, "end": v(22.66, 9) * mm});
            skLineSegment(sketch, "E28.15.0.12", {"start": v(28.73, 12.5) * mm, "end": v(30.75, 9) * mm});
            skCircle(sketch, "E28.18.0.12", {"center": v(26.7, 9) * mm, "radius": 3.5 * mm, "construction": true});
            skLineSegment(sketch, "E28.0.0.13", {"start": v(30.75, 18) * mm, "end": v(28.73, 14.5) * mm});
            skLineSegment(sketch, "E28.3.0.13", {"start": v(28.73, 14.5) * mm, "end": v(24.69, 14.5) * mm});
            skLineSegment(sketch, "E28.6.0.13", {"start": v(24.69, 21.5) * mm, "end": v(28.73, 21.5) * mm});
            skLineSegment(sketch, "E28.9.0.13", {"start": v(22.66, 18) * mm, "end": v(24.69, 21.5) * mm});
            skLineSegment(sketch, "E28.12.0.13", {"start": v(24.69, 14.5) * mm, "end": v(22.66, 18) * mm});
            skLineSegment(sketch, "E28.15.0.13", {"start": v(28.73, 21.5) * mm, "end": v(30.75, 18) * mm});
            skCircle(sketch, "E28.18.0.13", {"center": v(26.7, 18) * mm, "radius": 3.5 * mm, "construction": true});
            skLineSegment(sketch, "E28.0.0.14", {"start": v(30.75, 27) * mm, "end": v(28.73, 23.5) * mm});
            skLineSegment(sketch, "E28.3.0.14", {"start": v(28.73, 23.5) * mm, "end": v(24.69, 23.5) * mm});
            skLineSegment(sketch, "E28.6.0.14", {"start": v(24.69, 30.5) * mm, "end": v(28.73, 30.5) * mm});
            skLineSegment(sketch, "E28.9.0.14", {"start": v(22.66, 27) * mm, "end": v(24.69, 30.5) * mm});
            skLineSegment(sketch, "E28.12.0.14", {"start": v(24.69, 23.5) * mm, "end": v(22.66, 27) * mm});
            skLineSegment(sketch, "E28.15.0.14", {"start": v(28.73, 30.5) * mm, "end": v(30.75, 27) * mm});
            skCircle(sketch, "E28.18.0.14", {"center": v(26.7, 27) * mm, "radius": 3.5 * mm, "construction": true});
            skLineSegment(sketch, "E28.0.0.15", {"start": v(30.75, 36) * mm, "end": v(28.73, 32.5) * mm});
            skLineSegment(sketch, "E28.3.0.15", {"start": v(28.73, 32.5) * mm, "end": v(24.69, 32.5) * mm});
            skLineSegment(sketch, "E28.6.0.15", {"start": v(24.69, 39.5) * mm, "end": v(28.73, 39.5) * mm});
            skLineSegment(sketch, "E28.9.0.15", {"start": v(22.66, 36) * mm, "end": v(24.69, 39.5) * mm});
            skLineSegment(sketch, "E28.12.0.15", {"start": v(24.69, 32.5) * mm, "end": v(22.66, 36) * mm});
            skLineSegment(sketch, "E28.15.0.15", {"start": v(28.73, 39.5) * mm, "end": v(30.75, 36) * mm});
            skCircle(sketch, "E28.18.0.15", {"center": v(26.7, 36) * mm, "radius": 3.5 * mm, "construction": true});
            skLineSegment(sketch, "E28.0.0.16", {"start": v(30.75, 45) * mm, "end": v(28.73, 41.5) * mm});
            skLineSegment(sketch, "E28.3.0.16", {"start": v(28.73, 41.5) * mm, "end": v(24.69, 41.5) * mm});
            skLineSegment(sketch, "E28.6.0.16", {"start": v(24.69, 48.5) * mm, "end": v(28.73, 48.5) * mm});
            skLineSegment(sketch, "E28.9.0.16", {"start": v(22.66, 45) * mm, "end": v(24.69, 48.5) * mm});
            skLineSegment(sketch, "E28.12.0.16", {"start": v(24.69, 41.5) * mm, "end": v(22.66, 45) * mm});
            skLineSegment(sketch, "E28.15.0.16", {"start": v(28.73, 48.5) * mm, "end": v(30.75, 45) * mm});
            skCircle(sketch, "E28.18.0.16", {"center": v(26.7, 45) * mm, "radius": 3.5 * mm, "construction": true});
            skLineSegment(sketch, "E28.0.0.17", {"start": v(30.75, 54) * mm, "end": v(28.73, 50.5) * mm});
            skLineSegment(sketch, "E28.3.0.17", {"start": v(28.73, 50.5) * mm, "end": v(24.69, 50.5) * mm});
            skLineSegment(sketch, "E28.6.0.17", {"start": v(24.69, 57.5) * mm, "end": v(28.73, 57.5) * mm});
            skLineSegment(sketch, "E28.9.0.17", {"start": v(22.66, 54) * mm, "end": v(24.69, 57.5) * mm});
            skLineSegment(sketch, "E28.12.0.17", {"start": v(24.69, 50.5) * mm, "end": v(22.66, 54) * mm});
            skLineSegment(sketch, "E28.15.0.17", {"start": v(28.73, 57.5) * mm, "end": v(30.75, 54) * mm});
            skCircle(sketch, "E28.18.0.17", {"center": v(26.7, 54) * mm, "radius": 3.5 * mm, "construction": true});
            skLineSegment(sketch, "E28.0.0.18", {"start": v(30.75, 63) * mm, "end": v(28.73, 59.5) * mm});
            skLineSegment(sketch, "E28.3.0.18", {"start": v(28.73, 59.5) * mm, "end": v(24.69, 59.5) * mm});
            skLineSegment(sketch, "E28.6.0.18", {"start": v(24.69, 66.5) * mm, "end": v(28.73, 66.5) * mm});
            skLineSegment(sketch, "E28.9.0.18", {"start": v(22.66, 63) * mm, "end": v(24.69, 66.5) * mm});
            skLineSegment(sketch, "E28.12.0.18", {"start": v(24.69, 59.5) * mm, "end": v(22.66, 63) * mm});
            skLineSegment(sketch, "E28.15.0.18", {"start": v(28.73, 66.5) * mm, "end": v(30.75, 63) * mm});
            skCircle(sketch, "E28.18.0.18", {"center": v(26.7, 63) * mm, "radius": 3.5 * mm, "construction": true});
            skLineSegment(sketch, "E28.0.0.19", {"start": v(30.75, 72) * mm, "end": v(28.73, 68.5) * mm});
            skLineSegment(sketch, "E28.3.0.19", {"start": v(28.73, 68.5) * mm, "end": v(24.69, 68.5) * mm});
            skLineSegment(sketch, "E28.6.0.19", {"start": v(24.69, 75.5) * mm, "end": v(28.73, 75.5) * mm});
            skLineSegment(sketch, "E28.9.0.19", {"start": v(22.66, 72) * mm, "end": v(24.69, 75.5) * mm});
            skLineSegment(sketch, "E28.12.0.19", {"start": v(24.69, 68.5) * mm, "end": v(22.66, 72) * mm});
            skLineSegment(sketch, "E28.15.0.19", {"start": v(28.73, 75.5) * mm, "end": v(30.75, 72) * mm});
            skCircle(sketch, "E28.18.0.19", {"center": v(26.7, 72) * mm, "radius": 3.5 * mm, "construction": true});
            skLineSegment(sketch, "E28.0.0.20", {"start": v(30.75, 81) * mm, "end": v(28.73, 77.5) * mm});
            skLineSegment(sketch, "E28.3.0.20", {"start": v(28.73, 77.5) * mm, "end": v(24.69, 77.5) * mm});
            skLineSegment(sketch, "E28.6.0.20", {"start": v(24.69, 84.5) * mm, "end": v(28.73, 84.5) * mm});
            skLineSegment(sketch, "E28.9.0.20", {"start": v(22.66, 81) * mm, "end": v(24.69, 84.5) * mm});
            skLineSegment(sketch, "E28.12.0.20", {"start": v(24.69, 77.5) * mm, "end": v(22.66, 81) * mm});
            skLineSegment(sketch, "E28.15.0.20", {"start": v(28.73, 84.5) * mm, "end": v(30.75, 81) * mm});
            skCircle(sketch, "E28.18.0.20", {"center": v(26.7, 81) * mm, "radius": 3.5 * mm, "construction": true});
            skLineSegment(sketch, "E28.0.0.21", {"start": v(30.75, 90) * mm, "end": v(28.73, 86.5) * mm});
            skLineSegment(sketch, "E28.3.0.21", {"start": v(28.73, 86.5) * mm, "end": v(24.69, 86.5) * mm});
            skLineSegment(sketch, "E28.6.0.21", {"start": v(24.69, 93.5) * mm, "end": v(28.73, 93.5) * mm});
            skLineSegment(sketch, "E28.9.0.21", {"start": v(22.66, 90) * mm, "end": v(24.69, 93.5) * mm});
            skLineSegment(sketch, "E28.12.0.21", {"start": v(24.69, 86.5) * mm, "end": v(22.66, 90) * mm});
            skLineSegment(sketch, "E28.15.0.21", {"start": v(28.73, 93.5) * mm, "end": v(30.75, 90) * mm});
            skCircle(sketch, "E28.18.0.21", {"center": v(26.7, 90) * mm, "radius": 3.5 * mm, "construction": true});
            skLineSegment(sketch, "E28.0.0.22", {"start": v(30.75, 99) * mm, "end": v(28.73, 95.5) * mm});
            skLineSegment(sketch, "E28.3.0.22", {"start": v(28.73, 95.5) * mm, "end": v(24.69, 95.5) * mm});
            skLineSegment(sketch, "E28.6.0.22", {"start": v(24.69, 102.5) * mm, "end": v(28.73, 102.5) * mm});
            skLineSegment(sketch, "E28.9.0.22", {"start": v(22.66, 99) * mm, "end": v(24.69, 102.5) * mm});
            skLineSegment(sketch, "E28.12.0.22", {"start": v(24.69, 95.5) * mm, "end": v(22.66, 99) * mm});
            skLineSegment(sketch, "E28.15.0.22", {"start": v(28.73, 102.5) * mm, "end": v(30.75, 99) * mm});
            skCircle(sketch, "E28.18.0.22", {"center": v(26.7, 99) * mm, "radius": 3.5 * mm, "construction": true});
            skCircle(sketch, "E29.1.0.0", {"center": v(11.7, 0) * mm, "radius": 3.5 * mm, "construction": true});
            skLineSegment(sketch, "E29.1.0.1", {"start": v(17.47, -46) * mm, "end": v(21.51, -46) * mm});
            skCircle(sketch, "E29.1.0.2", {"center": v(11.7, -63) * mm, "radius": 3.5 * mm, "construction": true});
            skPoint(sketch, "E29.1.0.3", {"position": v(16.47, 33.25) * mm});
            skPoint(sketch, "E29.1.0.4", {"position": v(16.47, -11.76) * mm});
            skPoint(sketch, "E29.1.0.5", {"position": v(16.47, 42.24) * mm});
            skCircle(sketch, "E29.1.0.6", {"center": v(11.7, 54) * mm, "radius": 3.5 * mm, "construction": true});
            skPoint(sketch, "E29.1.0.7", {"position": v(16.47, -29.76) * mm});
            skLineSegment(sketch, "E29.1.0.8", {"start": v(17.48, -55) * mm, "end": v(21.52, -55) * mm});
            skPoint(sketch, "E29.1.0.9", {"position": v(16.47, -56.75) * mm});
            skLineSegment(sketch, "E29.1.0.10", {"start": v(9.69, -41.5) * mm, "end": v(13.73, -41.5) * mm});
            skCircle(sketch, "E29.1.0.11", {"center": v(11.7, -72) * mm, "radius": 3.5 * mm, "construction": true});
            skCircle(sketch, "E29.1.0.12", {"center": v(11.7, -36) * mm, "radius": 3.5 * mm, "construction": true});
            skCircle(sketch, "E29.1.0.13", {"center": v(19.5, 94.5) * mm, "radius": 3.5 * mm, "construction": true});
            skPoint(sketch, "E29.1.0.14", {"position": v(16.47, -92.75) * mm});
            skCircle(sketch, "E29.1.0.15", {"center": v(11.7, 63) * mm, "radius": 3.5 * mm, "construction": true});
            skCircle(sketch, "E29.1.0.16", {"center": v(11.7, -9) * mm, "radius": 3.5 * mm, "construction": true});
            skLineSegment(sketch, "E29.1.0.17", {"start": v(9.69, -32.5) * mm, "end": v(13.73, -32.5) * mm});
            skPoint(sketch, "E29.1.0.18", {"position": v(16.47, -74.75) * mm});
            skCircle(sketch, "E29.1.0.19", {"center": v(11.7, -90) * mm, "radius": 3.5 * mm, "construction": true});
            skLineSegment(sketch, "E29.1.0.20", {"start": v(9.69, -59.5) * mm, "end": v(13.73, -59.5) * mm});
            skCircle(sketch, "E29.1.0.21", {"center": v(11.7, 99) * mm, "radius": 3.5 * mm, "construction": true});
            skPoint(sketch, "E29.1.0.22", {"position": v(11.7, -95.5) * mm});
            skCircle(sketch, "E29.1.0.23", {"center": v(11.7, -99) * mm, "radius": 3.5 * mm, "construction": true});
            skLineSegment(sketch, "E29.1.0.24", {"start": v(9.69, -77.5) * mm, "end": v(13.73, -77.5) * mm});
            skCircle(sketch, "E29.1.0.25", {"center": v(19.5, 13.5) * mm, "radius": 3.5 * mm, "construction": true});
            skCircle(sketch, "E29.1.0.26", {"center": v(11.7, -81) * mm, "radius": 3.5 * mm, "construction": true});
            skLineSegment(sketch, "E29.1.0.27", {"start": v(17.48, -73) * mm, "end": v(21.52, -73) * mm});
            skCircle(sketch, "E29.1.0.28", {"center": v(11.7, 9) * mm, "radius": 3.5 * mm, "construction": true});
            skLineSegment(sketch, "E29.1.0.29", {"start": v(17.48, -37) * mm, "end": v(21.52, -37) * mm});
            skPoint(sketch, "E29.1.0.30", {"position": v(16.47, 51.25) * mm});
            skCircle(sketch, "E29.1.0.31", {"center": v(19.5, 76.5) * mm, "radius": 3.5 * mm, "construction": true});
            skCircle(sketch, "E29.1.0.32", {"center": v(19.5, -58.5) * mm, "radius": 3.5 * mm, "construction": true});
            skCircle(sketch, "E29.1.0.33", {"center": v(19.5, -49.5) * mm, "radius": 3.5 * mm, "construction": true});
            skPoint(sketch, "E29.1.0.34", {"position": v(16.47, 78.24) * mm});
            skLineSegment(sketch, "E29.1.0.35", {"start": v(9.69, -86.5) * mm, "end": v(13.73, -86.5) * mm});
            skCircle(sketch, "E29.1.0.36", {"center": v(19.5, -40.5) * mm, "radius": 3.5 * mm, "construction": true});
            skCircle(sketch, "E29.1.0.37", {"center": v(19.5, -94.5) * mm, "radius": 3.5 * mm, "construction": true});
            skCircle(sketch, "E29.1.0.38", {"center": v(19.5, -13.5) * mm, "radius": 3.5 * mm, "construction": true});
            skPoint(sketch, "E29.1.0.39", {"position": v(16.47, 60.24) * mm});
            skPoint(sketch, "E29.1.0.40", {"position": v(16.47, 15.25) * mm});
            skLineSegment(sketch, "E29.1.0.41", {"start": v(9.69, -50.5) * mm, "end": v(13.73, -50.5) * mm});
            skCircle(sketch, "E29.1.0.42", {"center": v(19.5, -85.5) * mm, "radius": 3.5 * mm, "construction": true});
            skCircle(sketch, "E29.1.0.43", {"center": v(19.5, 31.5) * mm, "radius": 3.5 * mm, "construction": true});
            skCircle(sketch, "E29.1.0.44", {"center": v(11.7, 36) * mm, "radius": 3.5 * mm, "construction": true});
            skCircle(sketch, "E29.1.0.45", {"center": v(19.5, -76.5) * mm, "radius": 3.5 * mm, "construction": true});
            skPoint(sketch, "E29.1.0.46", {"position": v(16.47, 96.24) * mm});
            skPoint(sketch, "E29.1.0.47", {"position": v(16.47, -2.75) * mm});
            skPoint(sketch, "E29.1.0.48", {"position": v(16.47, -83.76) * mm});
            skCircle(sketch, "E29.1.0.49", {"center": v(11.7, -45) * mm, "radius": 3.5 * mm, "construction": true});
            skCircle(sketch, "E29.1.0.50", {"center": v(11.7, 45) * mm, "radius": 3.5 * mm, "construction": true});
            skPoint(sketch, "E29.1.0.51", {"position": v(16.47, -20.75) * mm});
            skCircle(sketch, "E29.1.0.52", {"center": v(19.5, 67.5) * mm, "radius": 3.5 * mm, "construction": true});
            skLineSegment(sketch, "E29.1.0.53", {"start": v(17.47, -64) * mm, "end": v(21.51, -64) * mm});
            skLineSegment(sketch, "E29.1.0.54", {"start": v(9.69, -68.5) * mm, "end": v(13.73, -68.5) * mm});
            skCircle(sketch, "E29.1.0.55", {"center": v(11.7, 27) * mm, "radius": 3.5 * mm, "construction": true});
            skCircle(sketch, "E29.1.0.56", {"center": v(19.5, -67.5) * mm, "radius": 3.5 * mm, "construction": true});
            skCircle(sketch, "E29.1.0.57", {"center": v(11.7, -54) * mm, "radius": 3.5 * mm, "construction": true});
            skCircle(sketch, "E29.1.0.58", {"center": v(19.5, 85.5) * mm, "radius": 3.5 * mm, "construction": true});
            skCircle(sketch, "E29.1.0.59", {"center": v(11.7, 90) * mm, "radius": 3.5 * mm, "construction": true});
            skPoint(sketch, "E29.1.0.60", {"position": v(16.47, -47.76) * mm});
            skCircle(sketch, "E29.1.0.61", {"center": v(11.7, -18) * mm, "radius": 3.5 * mm, "construction": true});
            skCircle(sketch, "E29.1.0.62", {"center": v(19.5, -31.5) * mm, "radius": 3.5 * mm, "construction": true});
            skPoint(sketch, "E29.1.0.63", {"position": v(16.47, 24.24) * mm});
            skLineSegment(sketch, "E29.1.0.64", {"start": v(17.47, -28) * mm, "end": v(21.51, -28) * mm});
            skCircle(sketch, "E29.1.0.65", {"center": v(11.7, 81) * mm, "radius": 3.5 * mm, "construction": true});
            skPoint(sketch, "E29.1.0.66", {"position": v(16.47, 6.24) * mm});
            skPoint(sketch, "E29.1.0.67", {"position": v(16.47, 87.25) * mm});
            skCircle(sketch, "E29.1.0.68", {"center": v(11.7, 72) * mm, "radius": 3.5 * mm, "construction": true});
            skPoint(sketch, "E29.1.0.69", {"position": v(16.47, 69.25) * mm});
            skLineSegment(sketch, "E29.1.0.70", {"start": v(9.69, -23.5) * mm, "end": v(13.73, -23.5) * mm});
            skPoint(sketch, "E29.1.0.71", {"position": v(16.47, -38.75) * mm});
            skCircle(sketch, "E29.1.0.72", {"center": v(19.5, 58.5) * mm, "radius": 3.5 * mm, "construction": true});
            skLineSegment(sketch, "E29.1.0.73", {"start": v(9.69, -102.5) * mm, "end": v(9.69, -93.5) * mm, "construction": true});
            skCircle(sketch, "E29.1.0.74", {"center": v(11.7, 18) * mm, "radius": 3.5 * mm, "construction": true});
            skLineSegment(sketch, "E29.1.0.75", {"start": v(17.48, -91) * mm, "end": v(21.52, -91) * mm});
            skPoint(sketch, "E29.1.0.76", {"position": v(16.47, -65.76) * mm});
            skCircle(sketch, "E29.1.0.77", {"center": v(19.5, 4.5) * mm, "radius": 3.5 * mm, "construction": true});
            skCircle(sketch, "E29.1.0.78", {"center": v(11.7, -27) * mm, "radius": 3.5 * mm, "construction": true});
            skCircle(sketch, "E29.1.0.79", {"center": v(19.5, -22.5) * mm, "radius": 3.5 * mm, "construction": true});
            skCircle(sketch, "E29.1.0.80", {"center": v(19.5, 40.5) * mm, "radius": 3.5 * mm, "construction": true});
            skCircle(sketch, "E29.1.0.81", {"center": v(19.5, 49.5) * mm, "radius": 3.5 * mm, "construction": true});
            skCircle(sketch, "E29.1.0.82", {"center": v(19.5, 22.5) * mm, "radius": 3.5 * mm, "construction": true});
            skLineSegment(sketch, "E29.1.0.83", {"start": v(17.48, -98) * mm, "end": v(17.48, -80) * mm, "construction": true});
            skCircle(sketch, "E29.1.0.84", {"center": v(19.5, -4.5) * mm, "radius": 3.5 * mm, "construction": true});
            skLineSegment(sketch, "E29.1.0.85", {"start": v(21.51, -10) * mm, "end": v(23.54, -13.5) * mm});
            skLineSegment(sketch, "E29.1.0.86", {"start": v(13.73, -59.5) * mm, "end": v(15.75, -63) * mm});
            skLineSegment(sketch, "E29.1.0.87", {"start": v(13.73, -12.5) * mm, "end": v(9.69, -12.5) * mm});
            skLineSegment(sketch, "E29.1.0.88", {"start": v(21.53, -17) * mm, "end": v(17.49, -17) * mm});
            skLineSegment(sketch, "E29.1.0.89", {"start": v(13.73, -23.5) * mm, "end": v(15.75, -27) * mm});
            skLineSegment(sketch, "E29.1.0.90", {"start": v(13.73, -68.5) * mm, "end": v(15.75, -72) * mm});
            skLineSegment(sketch, "E29.1.0.91", {"start": v(21.52, 28) * mm, "end": v(17.48, 28) * mm});
            skLineSegment(sketch, "E29.1.0.92", {"start": v(21.53, -89) * mm, "end": v(17.49, -89) * mm});
            skLineSegment(sketch, "E29.1.0.93", {"start": v(13.73, -41.5) * mm, "end": v(15.75, -45) * mm});
            skLineSegment(sketch, "E29.1.0.94", {"start": v(13.73, 14.5) * mm, "end": v(9.69, 14.5) * mm});
            skLineSegment(sketch, "E29.1.0.95", {"start": v(21.52, -8) * mm, "end": v(17.48, -8) * mm});
            skLineSegment(sketch, "E29.1.0.96", {"start": v(15.46, -94.5) * mm, "end": v(17.48, -91) * mm});
            skLineSegment(sketch, "E29.1.0.97", {"start": v(9.69, 30.5) * mm, "end": v(13.73, 30.5) * mm});
            skLineSegment(sketch, "E29.1.0.98", {"start": v(7.66, -63) * mm, "end": v(9.69, -59.5) * mm});
            skLineSegment(sketch, "E29.1.0.99", {"start": v(21.51, -28) * mm, "end": v(23.54, -31.5) * mm});
            skLineSegment(sketch, "E29.1.0.100", {"start": v(9.69, -14.5) * mm, "end": v(13.73, -14.5) * mm});
            skLineSegment(sketch, "E29.1.0.101", {"start": v(9.69, -95.5) * mm, "end": v(13.73, -95.5) * mm});
            skLineSegment(sketch, "E29.1.0.102", {"start": v(13.73, 77.5) * mm, "end": v(9.69, 77.5) * mm});
            skLineSegment(sketch, "E29.1.0.103", {"start": v(13.73, -95.5) * mm, "end": v(15.75, -99) * mm});
            skLineSegment(sketch, "E29.1.0.104", {"start": v(7.66, -81) * mm, "end": v(9.69, -77.5) * mm});
            skLineSegment(sketch, "E29.1.0.105", {"start": v(21.51, -64) * mm, "end": v(23.54, -67.5) * mm});
            skLineSegment(sketch, "E29.1.0.106", {"start": v(17.48, 17) * mm, "end": v(21.52, 17) * mm});
            skLineSegment(sketch, "E29.1.0.107", {"start": v(13.73, 32.5) * mm, "end": v(9.69, 32.5) * mm});
            skLineSegment(sketch, "E29.1.0.108", {"start": v(13.73, 50.5) * mm, "end": v(9.69, 50.5) * mm});
            skLineSegment(sketch, "E29.1.0.109", {"start": v(7.66, -45) * mm, "end": v(9.69, -41.5) * mm});
            skLineSegment(sketch, "E29.1.0.110", {"start": v(13.73, -21.5) * mm, "end": v(9.69, -21.5) * mm});
            skLineSegment(sketch, "E29.1.0.111", {"start": v(17.48, 71) * mm, "end": v(21.52, 71) * mm});
            skLineSegment(sketch, "E29.1.0.112", {"start": v(21.52, 10) * mm, "end": v(17.48, 10) * mm});
            skLineSegment(sketch, "E29.1.0.113", {"start": v(21.53, -71) * mm, "end": v(17.49, -71) * mm});
            skLineSegment(sketch, "E29.1.0.114", {"start": v(15.46, -40.5) * mm, "end": v(17.48, -37) * mm});
            skLineSegment(sketch, "E29.1.0.115", {"start": v(17.47, 80) * mm, "end": v(21.51, 80) * mm});
            skLineSegment(sketch, "E29.1.0.116", {"start": v(21.52, 46) * mm, "end": v(17.48, 46) * mm});
            skLineSegment(sketch, "E29.1.0.117", {"start": v(21.52, 82) * mm, "end": v(17.48, 82) * mm});
            skLineSegment(sketch, "E29.1.0.118", {"start": v(21.53, -53) * mm, "end": v(17.49, -53) * mm});
            skLineSegment(sketch, "E29.1.0.119", {"start": v(21.52, -26) * mm, "end": v(17.48, -26) * mm});
            skLineSegment(sketch, "E29.1.0.120", {"start": v(13.73, -93.5) * mm, "end": v(9.69, -93.5) * mm});
            skLineSegment(sketch, "E29.1.0.121", {"start": v(21.52, 64) * mm, "end": v(17.48, 64) * mm});
            skLineSegment(sketch, "E29.1.0.122", {"start": v(21.53, 37) * mm, "end": v(17.49, 37) * mm});
            skLineSegment(sketch, "E29.1.0.123", {"start": v(13.73, -75.5) * mm, "end": v(9.69, -75.5) * mm});
            skLineSegment(sketch, "E29.1.0.124", {"start": v(9.69, 21.5) * mm, "end": v(13.73, 21.5) * mm});
            skLineSegment(sketch, "E29.1.0.125", {"start": v(21.53, 91) * mm, "end": v(17.49, 91) * mm});
            skLineSegment(sketch, "E29.1.0.126", {"start": v(15.46, -67.5) * mm, "end": v(17.47, -64) * mm});
            skLineSegment(sketch, "E29.1.0.127", {"start": v(21.52, -44) * mm, "end": v(17.48, -44) * mm});
            skLineSegment(sketch, "E29.1.0.128", {"start": v(13.73, 41.5) * mm, "end": v(9.69, 41.5) * mm});
            skLineSegment(sketch, "E29.1.0.129", {"start": v(21.52, -80) * mm, "end": v(17.48, -80) * mm});
            skLineSegment(sketch, "E29.1.0.130", {"start": v(17.47, 98) * mm, "end": v(21.51, 98) * mm});
            skLineSegment(sketch, "E29.1.0.131", {"start": v(13.73, 86.5) * mm, "end": v(9.69, 86.5) * mm});
            skLineSegment(sketch, "E29.1.0.132", {"start": v(21.53, 73) * mm, "end": v(17.49, 73) * mm});
            skLineSegment(sketch, "E29.1.0.133", {"start": v(21.51, -46) * mm, "end": v(23.54, -49.5) * mm});
            skLineSegment(sketch, "E29.1.0.134", {"start": v(13.73, -84.5) * mm, "end": v(9.69, -84.5) * mm});
            skLineSegment(sketch, "E29.1.0.135", {"start": v(13.73, -30.5) * mm, "end": v(9.69, -30.5) * mm});
            skLineSegment(sketch, "E29.1.0.136", {"start": v(7.66, -27) * mm, "end": v(9.69, -23.5) * mm});
            skLineSegment(sketch, "E29.1.0.137", {"start": v(9.69, 84.5) * mm, "end": v(13.73, 84.5) * mm});
            skLineSegment(sketch, "E29.1.0.138", {"start": v(9.69, 75.5) * mm, "end": v(13.73, 75.5) * mm});
            skLineSegment(sketch, "E29.1.0.139", {"start": v(17.47, -82) * mm, "end": v(21.51, -82) * mm});
            skLineSegment(sketch, "E29.1.0.140", {"start": v(13.73, -66.5) * mm, "end": v(9.69, -66.5) * mm});
            skLineSegment(sketch, "E29.1.0.141", {"start": v(21.53, 19) * mm, "end": v(17.49, 19) * mm});
            skLineSegment(sketch, "E29.1.0.142", {"start": v(17.47, -10) * mm, "end": v(21.51, -10) * mm});
            skLineSegment(sketch, "E29.1.0.143", {"start": v(13.73, -32.5) * mm, "end": v(15.75, -36) * mm});
            skLineSegment(sketch, "E29.1.0.144", {"start": v(17.48, -1) * mm, "end": v(21.52, -1) * mm});
            skLineSegment(sketch, "E29.1.0.145", {"start": v(21.52, -98) * mm, "end": v(17.48, -98) * mm});
            skLineSegment(sketch, "E29.1.0.146", {"start": v(13.73, 59.5) * mm, "end": v(9.69, 59.5) * mm});
            skLineSegment(sketch, "E29.1.0.147", {"start": v(21.53, 1) * mm, "end": v(17.49, 1) * mm});
            skLineSegment(sketch, "E29.1.0.148", {"start": v(7.66, -99) * mm, "end": v(9.69, -95.5) * mm});
            skLineSegment(sketch, "E29.1.0.149", {"start": v(13.73, -39.5) * mm, "end": v(9.69, -39.5) * mm});
            skLineSegment(sketch, "E29.1.0.150", {"start": v(17.47, 26) * mm, "end": v(21.51, 26) * mm});
            skLineSegment(sketch, "E29.1.0.151", {"start": v(21.52, -37) * mm, "end": v(23.54, -40.5) * mm});
            skLineSegment(sketch, "E29.1.0.152", {"start": v(17.48, -19) * mm, "end": v(21.52, -19) * mm});
            skLineSegment(sketch, "E29.1.0.153", {"start": v(15.46, -85.5) * mm, "end": v(17.47, -82) * mm});
            skLineSegment(sketch, "E29.1.0.154", {"start": v(17.47, 44) * mm, "end": v(21.51, 44) * mm});
            skLineSegment(sketch, "E29.1.0.155", {"start": v(13.73, 23.5) * mm, "end": v(9.69, 23.5) * mm});
            skLineSegment(sketch, "E29.1.0.156", {"start": v(13.73, -3.5) * mm, "end": v(9.69, -3.5) * mm});
            skLineSegment(sketch, "E29.1.0.157", {"start": v(7.66, -72) * mm, "end": v(9.69, -68.5) * mm});
            skLineSegment(sketch, "E29.1.0.158", {"start": v(21.52, -91) * mm, "end": v(23.54, -94.5) * mm});
            skLineSegment(sketch, "E29.1.0.159", {"start": v(7.66, -54) * mm, "end": v(9.69, -50.5) * mm});
            skLineSegment(sketch, "E29.1.0.160", {"start": v(15.46, -76.5) * mm, "end": v(17.48, -73) * mm});
            skLineSegment(sketch, "E29.1.0.161", {"start": v(17.47, 62) * mm, "end": v(21.51, 62) * mm});
            skLineSegment(sketch, "E29.1.0.162", {"start": v(21.51, -82) * mm, "end": v(23.54, -85.5) * mm});
            skLineSegment(sketch, "E29.1.0.163", {"start": v(17.48, 53) * mm, "end": v(21.52, 53) * mm});
            skLineSegment(sketch, "E29.1.0.164", {"start": v(7.66, -36) * mm, "end": v(9.69, -32.5) * mm});
            skLineSegment(sketch, "E29.1.0.165", {"start": v(9.69, 102.5) * mm, "end": v(13.73, 102.5) * mm});
            skLineSegment(sketch, "E29.1.0.166", {"start": v(15.46, -58.5) * mm, "end": v(17.48, -55) * mm});
            skLineSegment(sketch, "E29.1.0.167", {"start": v(13.73, -48.5) * mm, "end": v(9.69, -48.5) * mm});
            skLineSegment(sketch, "E29.1.0.168", {"start": v(21.52, -55) * mm, "end": v(23.54, -58.5) * mm});
            skLineSegment(sketch, "E29.1.0.169", {"start": v(9.69, 39.5) * mm, "end": v(13.73, 39.5) * mm});
            skLineSegment(sketch, "E29.1.0.170", {"start": v(13.73, -57.5) * mm, "end": v(9.69, -57.5) * mm});
            skLineSegment(sketch, "E29.1.0.171", {"start": v(21.53, 55) * mm, "end": v(17.49, 55) * mm});
            skLineSegment(sketch, "E29.1.0.172", {"start": v(9.69, 48.5) * mm, "end": v(13.73, 48.5) * mm});
            skLineSegment(sketch, "E29.1.0.173", {"start": v(9.69, 3.5) * mm, "end": v(13.73, 3.5) * mm});
            skLineSegment(sketch, "E29.1.0.174", {"start": v(9.69, 12.5) * mm, "end": v(13.73, 12.5) * mm});
            skLineSegment(sketch, "E29.1.0.175", {"start": v(13.73, -50.5) * mm, "end": v(15.75, -54) * mm});
            skLineSegment(sketch, "E29.1.0.176", {"start": v(9.69, 93.5) * mm, "end": v(13.73, 93.5) * mm});
            skLineSegment(sketch, "E29.1.0.177", {"start": v(17.48, 89) * mm, "end": v(21.52, 89) * mm});
            skLineSegment(sketch, "E29.1.0.178", {"start": v(13.73, -77.5) * mm, "end": v(15.75, -81) * mm});
            skLineSegment(sketch, "E29.1.0.179", {"start": v(13.73, 5.5) * mm, "end": v(9.69, 5.5) * mm});
            skLineSegment(sketch, "E29.1.0.180", {"start": v(21.52, -73) * mm, "end": v(23.54, -76.5) * mm});
            skLineSegment(sketch, "E29.1.0.181", {"start": v(13.73, -102.5) * mm, "end": v(9.69, -102.5) * mm});
            skLineSegment(sketch, "E29.1.0.182", {"start": v(17.48, 35) * mm, "end": v(21.52, 35) * mm});
            skLineSegment(sketch, "E29.1.0.183", {"start": v(17.47, 8) * mm, "end": v(21.51, 8) * mm});
            skLineSegment(sketch, "E29.1.0.184", {"start": v(9.69, -5.5) * mm, "end": v(13.73, -5.5) * mm});
            skLineSegment(sketch, "E29.1.0.185", {"start": v(13.73, -86.5) * mm, "end": v(15.75, -90) * mm});
            skLineSegment(sketch, "E29.1.0.186", {"start": v(9.69, 57.5) * mm, "end": v(13.73, 57.5) * mm});
            skLineSegment(sketch, "E29.1.0.187", {"start": v(13.73, 68.5) * mm, "end": v(9.69, 68.5) * mm});
            skLineSegment(sketch, "E29.1.0.188", {"start": v(21.52, -62) * mm, "end": v(17.48, -62) * mm});
            skLineSegment(sketch, "E29.1.0.189", {"start": v(15.46, -49.5) * mm, "end": v(17.47, -46) * mm});
            skLineSegment(sketch, "E29.1.0.190", {"start": v(13.73, 95.5) * mm, "end": v(9.69, 95.5) * mm});
            skLineSegment(sketch, "E29.1.0.191", {"start": v(9.69, 66.5) * mm, "end": v(13.73, 66.5) * mm});
            skLineSegment(sketch, "E29.1.0.192", {"start": v(7.66, -90) * mm, "end": v(9.69, -86.5) * mm});
            skLineSegment(sketch, "E29.1.0.193", {"start": v(21.53, -35) * mm, "end": v(17.49, -35) * mm});
            skLineSegment(sketch, "E29.1.0.194", {"start": v(23.54, 40.5) * mm, "end": v(21.53, 37) * mm});
            skLineSegment(sketch, "E29.1.0.195", {"start": v(17.49, 55) * mm, "end": v(15.46, 58.5) * mm});
            skLineSegment(sketch, "E29.1.0.196", {"start": v(9.69, -84.5) * mm, "end": v(7.66, -81) * mm});
            skLineSegment(sketch, "E29.1.0.197", {"start": v(23.54, -31.5) * mm, "end": v(21.53, -35) * mm});
            skLineSegment(sketch, "E29.1.0.198", {"start": v(9.69, -66.5) * mm, "end": v(7.66, -63) * mm});
            skLineSegment(sketch, "E29.1.0.199", {"start": v(23.54, -67.5) * mm, "end": v(21.53, -71) * mm});
            skLineSegment(sketch, "E29.1.0.200", {"start": v(23.54, -4.5) * mm, "end": v(21.52, -8) * mm});
            skLineSegment(sketch, "E29.1.0.201", {"start": v(17.48, -8) * mm, "end": v(15.46, -4.5) * mm});
            skLineSegment(sketch, "E29.1.0.202", {"start": v(21.51, 98) * mm, "end": v(23.54, 94.5) * mm});
            skLineSegment(sketch, "E29.1.0.203", {"start": v(17.49, 37) * mm, "end": v(15.46, 40.5) * mm});
            skLineSegment(sketch, "E29.1.0.204", {"start": v(9.69, -39.5) * mm, "end": v(7.66, -36) * mm});
            skLineSegment(sketch, "E29.1.0.205", {"start": v(7.66, 72) * mm, "end": v(9.69, 75.5) * mm});
            skLineSegment(sketch, "E29.1.0.206", {"start": v(23.54, -94.5) * mm, "end": v(21.52, -98) * mm});
            skLineSegment(sketch, "E29.1.0.207", {"start": v(15.75, -63) * mm, "end": v(13.73, -66.5) * mm});
            skLineSegment(sketch, "E29.1.0.208", {"start": v(9.69, 86.5) * mm, "end": v(7.66, 90) * mm});
            skLineSegment(sketch, "E29.1.0.209", {"start": v(7.66, 81) * mm, "end": v(9.69, 84.5) * mm});
            skLineSegment(sketch, "E29.1.0.210", {"start": v(15.75, 72) * mm, "end": v(13.73, 68.5) * mm});
            skLineSegment(sketch, "E29.1.0.211", {"start": v(9.69, 23.5) * mm, "end": v(7.66, 27) * mm});
            skLineSegment(sketch, "E29.1.0.212", {"start": v(15.46, -31.5) * mm, "end": v(17.47, -28) * mm});
            skLineSegment(sketch, "E29.1.0.213", {"start": v(23.54, 31.5) * mm, "end": v(21.52, 28) * mm});
            skLineSegment(sketch, "E29.1.0.214", {"start": v(17.48, 82) * mm, "end": v(15.46, 85.5) * mm});
            skLineSegment(sketch, "E29.1.0.215", {"start": v(17.48, 64) * mm, "end": v(15.46, 67.5) * mm});
            skLineSegment(sketch, "E29.1.0.216", {"start": v(15.46, 13.5) * mm, "end": v(17.48, 17) * mm});
            skLineSegment(sketch, "E29.1.0.217", {"start": v(15.46, -4.5) * mm, "end": v(17.48, -1) * mm});
            skLineSegment(sketch, "E29.1.0.218", {"start": v(17.49, -35) * mm, "end": v(15.46, -31.5) * mm});
            skLineSegment(sketch, "E29.1.0.219", {"start": v(7.66, 18) * mm, "end": v(9.69, 21.5) * mm});
            skLineSegment(sketch, "E29.1.0.220", {"start": v(23.54, -85.5) * mm, "end": v(21.53, -89) * mm});
            skLineSegment(sketch, "E29.1.0.221", {"start": v(15.46, 76.5) * mm, "end": v(17.47, 80) * mm});
            skLineSegment(sketch, "E29.1.0.222", {"start": v(13.73, 84.5) * mm, "end": v(15.75, 81) * mm});
            skLineSegment(sketch, "E29.1.0.223", {"start": v(15.75, -9) * mm, "end": v(13.73, -12.5) * mm});
            skLineSegment(sketch, "E29.1.0.224", {"start": v(9.69, -57.5) * mm, "end": v(7.66, -54) * mm});
            skLineSegment(sketch, "E29.1.0.225", {"start": v(23.54, -22.5) * mm, "end": v(21.52, -26) * mm});
            skLineSegment(sketch, "E29.1.0.226", {"start": v(13.73, 3.5) * mm, "end": v(15.75, 0) * mm});
            skLineSegment(sketch, "E29.1.0.227", {"start": v(23.54, 94.5) * mm, "end": v(21.53, 91) * mm});
            skLineSegment(sketch, "E29.1.0.228", {"start": v(9.69, 5.5) * mm, "end": v(7.66, 9) * mm});
            skLineSegment(sketch, "E29.1.0.229", {"start": v(15.75, 90) * mm, "end": v(13.73, 86.5) * mm});
            skLineSegment(sketch, "E29.1.0.230", {"start": v(7.66, 45) * mm, "end": v(9.69, 48.5) * mm});
            skLineSegment(sketch, "E29.1.0.231", {"start": v(21.52, 71) * mm, "end": v(23.54, 67.5) * mm});
            skLineSegment(sketch, "E29.1.0.232", {"start": v(7.66, 0) * mm, "end": v(9.69, 3.5) * mm});
            skLineSegment(sketch, "E29.1.0.233", {"start": v(7.66, 54) * mm, "end": v(9.69, 57.5) * mm});
            skLineSegment(sketch, "E29.1.0.234", {"start": v(15.46, 4.5) * mm, "end": v(17.47, 8) * mm});
            skLineSegment(sketch, "E29.1.0.235", {"start": v(21.51, 26) * mm, "end": v(23.54, 22.5) * mm});
            skLineSegment(sketch, "E29.1.0.236", {"start": v(13.73, 75.5) * mm, "end": v(15.75, 72) * mm});
            skLineSegment(sketch, "E29.1.0.237", {"start": v(15.75, 99) * mm, "end": v(13.73, 95.5) * mm});
            skLineSegment(sketch, "E29.1.0.238", {"start": v(7.66, 90) * mm, "end": v(9.69, 93.5) * mm});
            skLineSegment(sketch, "E29.1.0.239", {"start": v(15.75, -90) * mm, "end": v(13.73, -93.5) * mm});
            skLineSegment(sketch, "E29.1.0.240", {"start": v(15.75, 45) * mm, "end": v(13.73, 41.5) * mm});
            skLineSegment(sketch, "E29.1.0.241", {"start": v(15.46, 49.5) * mm, "end": v(17.48, 53) * mm});
            skLineSegment(sketch, "E29.1.0.242", {"start": v(13.73, 57.5) * mm, "end": v(15.75, 54) * mm});
            skLineSegment(sketch, "E29.1.0.243", {"start": v(15.75, -54) * mm, "end": v(13.73, -57.5) * mm});
            skLineSegment(sketch, "E29.1.0.244", {"start": v(15.75, 63) * mm, "end": v(13.73, 59.5) * mm});
            skLineSegment(sketch, "E29.1.0.245", {"start": v(21.51, 8) * mm, "end": v(23.54, 4.5) * mm});
            skLineSegment(sketch, "E29.1.0.246", {"start": v(23.54, -76.5) * mm, "end": v(21.52, -80) * mm});
            skLineSegment(sketch, "E29.1.0.247", {"start": v(7.66, 99) * mm, "end": v(9.69, 102.5) * mm});
            skLineSegment(sketch, "E29.1.0.248", {"start": v(15.46, 40.5) * mm, "end": v(17.47, 44) * mm});
            skLineSegment(sketch, "E29.1.0.249", {"start": v(9.69, -48.5) * mm, "end": v(7.66, -45) * mm});
            skLineSegment(sketch, "E29.1.0.250", {"start": v(9.69, 41.5) * mm, "end": v(7.66, 45) * mm});
            skLineSegment(sketch, "E29.1.0.251", {"start": v(9.69, -102.5) * mm, "end": v(7.66, -99) * mm});
            skLineSegment(sketch, "E29.1.0.252", {"start": v(17.49, 91) * mm, "end": v(15.46, 94.5) * mm});
            skLineSegment(sketch, "E29.1.0.253", {"start": v(15.75, -18) * mm, "end": v(13.73, -21.5) * mm});
            skLineSegment(sketch, "E29.1.0.254", {"start": v(17.49, -53) * mm, "end": v(15.46, -49.5) * mm});
            skLineSegment(sketch, "E29.1.0.255", {"start": v(17.48, -80) * mm, "end": v(15.46, -76.5) * mm});
            skLineSegment(sketch, "E29.1.0.256", {"start": v(23.54, 76.5) * mm, "end": v(21.53, 73) * mm});
            skLineSegment(sketch, "E29.1.0.257", {"start": v(21.52, 35) * mm, "end": v(23.54, 31.5) * mm});
            skLineSegment(sketch, "E29.1.0.258", {"start": v(21.51, 62) * mm, "end": v(23.54, 58.5) * mm});
            skLineSegment(sketch, "E29.1.0.259", {"start": v(13.73, 30.5) * mm, "end": v(15.75, 27) * mm});
            skLineSegment(sketch, "E29.1.0.260", {"start": v(15.75, -99) * mm, "end": v(13.73, -102.5) * mm});
            skLineSegment(sketch, "E29.1.0.261", {"start": v(13.73, -14.5) * mm, "end": v(15.75, -18) * mm});
            skLineSegment(sketch, "E29.1.0.262", {"start": v(13.73, 93.5) * mm, "end": v(15.75, 90) * mm});
            skLineSegment(sketch, "E29.1.0.263", {"start": v(7.66, 9) * mm, "end": v(9.69, 12.5) * mm});
            skLineSegment(sketch, "E29.1.0.264", {"start": v(23.54, 67.5) * mm, "end": v(21.52, 64) * mm});
            skLineSegment(sketch, "E29.1.0.265", {"start": v(17.48, -62) * mm, "end": v(15.46, -58.5) * mm});
            skLineSegment(sketch, "E29.1.0.266", {"start": v(9.69, 68.5) * mm, "end": v(7.66, 72) * mm});
            skLineSegment(sketch, "E29.1.0.267", {"start": v(17.49, -17) * mm, "end": v(15.46, -13.5) * mm});
            skLineSegment(sketch, "E29.1.0.268", {"start": v(23.54, 4.5) * mm, "end": v(21.53, 1) * mm});
            skLineSegment(sketch, "E29.1.0.269", {"start": v(21.51, 80) * mm, "end": v(23.54, 76.5) * mm});
            skLineSegment(sketch, "E29.1.0.270", {"start": v(15.75, -27) * mm, "end": v(13.73, -30.5) * mm});
            skLineSegment(sketch, "E29.1.0.271", {"start": v(23.54, 13.5) * mm, "end": v(21.52, 10) * mm});
            skLineSegment(sketch, "E29.1.0.272", {"start": v(9.69, 32.5) * mm, "end": v(7.66, 36) * mm});
            skLineSegment(sketch, "E29.1.0.273", {"start": v(15.75, -72) * mm, "end": v(13.73, -75.5) * mm});
            skLineSegment(sketch, "E29.1.0.274", {"start": v(13.73, 39.5) * mm, "end": v(15.75, 36) * mm});
            skLineSegment(sketch, "E29.1.0.275", {"start": v(13.73, 102.5) * mm, "end": v(15.75, 99) * mm});
            skLineSegment(sketch, "E29.1.0.276", {"start": v(15.75, 54) * mm, "end": v(13.73, 50.5) * mm});
            skLineSegment(sketch, "E29.1.0.277", {"start": v(15.75, 81) * mm, "end": v(13.73, 77.5) * mm});
            skLineSegment(sketch, "E29.1.0.278", {"start": v(15.75, 0) * mm, "end": v(13.73, -3.5) * mm});
            skLineSegment(sketch, "E29.1.0.279", {"start": v(7.66, 63) * mm, "end": v(9.69, 66.5) * mm});
            skLineSegment(sketch, "E29.1.0.280", {"start": v(13.73, 66.5) * mm, "end": v(15.75, 63) * mm});
            skLineSegment(sketch, "E29.1.0.281", {"start": v(13.73, -5.5) * mm, "end": v(15.75, -9) * mm});
            skLineSegment(sketch, "E29.1.0.282", {"start": v(9.69, -75.5) * mm, "end": v(7.66, -72) * mm});
            skLineSegment(sketch, "E29.1.0.283", {"start": v(17.48, -26) * mm, "end": v(15.46, -22.5) * mm});
            skLineSegment(sketch, "E29.1.0.284", {"start": v(21.52, 17) * mm, "end": v(23.54, 13.5) * mm});
            skLineSegment(sketch, "E29.1.0.285", {"start": v(13.73, 21.5) * mm, "end": v(15.75, 18) * mm});
            skLineSegment(sketch, "E29.1.0.286", {"start": v(23.54, -13.5) * mm, "end": v(21.53, -17) * mm});
            skLineSegment(sketch, "E29.1.0.287", {"start": v(23.54, -58.5) * mm, "end": v(21.52, -62) * mm});
            skLineSegment(sketch, "E29.1.0.288", {"start": v(23.54, 58.5) * mm, "end": v(21.53, 55) * mm});
            skLineSegment(sketch, "E29.1.0.289", {"start": v(21.52, 89) * mm, "end": v(23.54, 85.5) * mm});
            skLineSegment(sketch, "E29.1.0.290", {"start": v(23.54, 22.5) * mm, "end": v(21.53, 19) * mm});
            skLineSegment(sketch, "E29.1.0.291", {"start": v(9.69, -93.5) * mm, "end": v(7.66, -90) * mm});
            skLineSegment(sketch, "E29.1.0.292", {"start": v(9.69, -3.5) * mm, "end": v(7.66, 0) * mm});
            skLineSegment(sketch, "E29.1.0.293", {"start": v(15.75, 18) * mm, "end": v(13.73, 14.5) * mm});
            skLineSegment(sketch, "E29.1.0.294", {"start": v(15.75, 36) * mm, "end": v(13.73, 32.5) * mm});
            skLineSegment(sketch, "E29.1.0.295", {"start": v(21.52, -1) * mm, "end": v(23.54, -4.5) * mm});
            skLineSegment(sketch, "E29.1.0.296", {"start": v(23.54, -49.5) * mm, "end": v(21.53, -53) * mm});
            skLineSegment(sketch, "E29.1.0.297", {"start": v(15.75, -45) * mm, "end": v(13.73, -48.5) * mm});
            skLineSegment(sketch, "E29.1.0.298", {"start": v(15.75, 27) * mm, "end": v(13.73, 23.5) * mm});
            skLineSegment(sketch, "E29.1.0.299", {"start": v(23.54, 85.5) * mm, "end": v(21.52, 82) * mm});
            skLineSegment(sketch, "E29.1.0.300", {"start": v(9.69, 95.5) * mm, "end": v(7.66, 99) * mm});
            skLineSegment(sketch, "E29.1.0.301", {"start": v(15.75, -36) * mm, "end": v(13.73, -39.5) * mm});
            skLineSegment(sketch, "E29.1.0.302", {"start": v(7.66, 27) * mm, "end": v(9.69, 30.5) * mm});
            skLineSegment(sketch, "E29.1.0.303", {"start": v(23.54, -40.5) * mm, "end": v(21.52, -44) * mm});
            skLineSegment(sketch, "E29.1.0.304", {"start": v(15.46, 85.5) * mm, "end": v(17.48, 89) * mm});
            skLineSegment(sketch, "E29.1.0.305", {"start": v(9.69, 50.5) * mm, "end": v(7.66, 54) * mm});
            skLineSegment(sketch, "E29.1.0.306", {"start": v(15.46, -22.5) * mm, "end": v(17.48, -19) * mm});
            skLineSegment(sketch, "E29.1.0.307", {"start": v(17.48, -44) * mm, "end": v(15.46, -40.5) * mm});
            skLineSegment(sketch, "E29.1.0.308", {"start": v(17.49, -89) * mm, "end": v(15.46, -85.5) * mm});
            skLineSegment(sketch, "E29.1.0.309", {"start": v(15.46, 31.5) * mm, "end": v(17.48, 35) * mm});
            skLineSegment(sketch, "E29.1.0.310", {"start": v(7.66, 36) * mm, "end": v(9.69, 39.5) * mm});
            skLineSegment(sketch, "E29.1.0.311", {"start": v(9.69, -30.5) * mm, "end": v(7.66, -27) * mm});
            skLineSegment(sketch, "E29.1.0.312", {"start": v(7.66, -9) * mm, "end": v(9.69, -5.5) * mm});
            skLineSegment(sketch, "E29.1.0.313", {"start": v(17.49, 19) * mm, "end": v(15.46, 22.5) * mm});
            skLineSegment(sketch, "E29.1.0.314", {"start": v(17.48, -98) * mm, "end": v(15.46, -94.5) * mm});
            skLineSegment(sketch, "E29.1.0.315", {"start": v(9.69, 77.5) * mm, "end": v(7.66, 81) * mm});
            skLineSegment(sketch, "E29.1.0.316", {"start": v(15.75, -81) * mm, "end": v(13.73, -84.5) * mm});
            skLineSegment(sketch, "E29.1.0.317", {"start": v(21.51, 44) * mm, "end": v(23.54, 40.5) * mm});
            skLineSegment(sketch, "E29.1.0.318", {"start": v(15.46, -13.5) * mm, "end": v(17.47, -10) * mm});
            skLineSegment(sketch, "E29.1.0.319", {"start": v(21.52, 53) * mm, "end": v(23.54, 49.5) * mm});
            skLineSegment(sketch, "E29.1.0.320", {"start": v(17.49, 1) * mm, "end": v(15.46, 4.5) * mm});
            skLineSegment(sketch, "E29.1.0.321", {"start": v(7.66, -18) * mm, "end": v(9.69, -14.5) * mm});
            skLineSegment(sketch, "E29.1.0.322", {"start": v(17.49, 73) * mm, "end": v(15.46, 76.5) * mm});
            skLineSegment(sketch, "E29.1.0.323", {"start": v(17.48, 10) * mm, "end": v(15.46, 13.5) * mm});
            skLineSegment(sketch, "E29.1.0.324", {"start": v(15.46, 67.5) * mm, "end": v(17.48, 71) * mm});
            skLineSegment(sketch, "E29.1.0.325", {"start": v(17.48, 46) * mm, "end": v(15.46, 49.5) * mm});
            skLineSegment(sketch, "E29.1.0.326", {"start": v(9.69, 59.5) * mm, "end": v(7.66, 63) * mm});
            skLineSegment(sketch, "E29.1.0.327", {"start": v(15.75, 9) * mm, "end": v(13.73, 5.5) * mm});
            skLineSegment(sketch, "E29.1.0.328", {"start": v(13.73, 12.5) * mm, "end": v(15.75, 9) * mm});
            skLineSegment(sketch, "E29.1.0.329", {"start": v(9.69, -21.5) * mm, "end": v(7.66, -18) * mm});
            skLineSegment(sketch, "E29.1.0.330", {"start": v(17.48, 28) * mm, "end": v(15.46, 31.5) * mm});
            skLineSegment(sketch, "E29.1.0.331", {"start": v(23.54, 49.5) * mm, "end": v(21.52, 46) * mm});
            skLineSegment(sketch, "E29.1.0.332", {"start": v(15.46, 58.5) * mm, "end": v(17.47, 62) * mm});
            skLineSegment(sketch, "E29.1.0.333", {"start": v(13.73, 48.5) * mm, "end": v(15.75, 45) * mm});
            skLineSegment(sketch, "E29.1.0.334", {"start": v(21.52, -19) * mm, "end": v(23.54, -22.5) * mm});
            skLineSegment(sketch, "E29.1.0.335", {"start": v(9.69, 14.5) * mm, "end": v(7.66, 18) * mm});
            skLineSegment(sketch, "E29.1.0.336", {"start": v(17.49, -71) * mm, "end": v(15.46, -67.5) * mm});
            skLineSegment(sketch, "E29.1.0.337", {"start": v(15.46, 94.5) * mm, "end": v(17.47, 98) * mm});
            skLineSegment(sketch, "E29.1.0.338", {"start": v(9.69, -12.5) * mm, "end": v(7.66, -9) * mm});
            skLineSegment(sketch, "E29.1.0.339", {"start": v(15.46, 22.5) * mm, "end": v(17.47, 26) * mm});
            skCircle(sketch, "E29.2.0.0", {"center": v(-3.3, 0) * mm, "radius": 3.5 * mm, "construction": true});
            skLineSegment(sketch, "E29.2.0.1", {"start": v(2.47, -46) * mm, "end": v(6.51, -46) * mm});
            skCircle(sketch, "E29.2.0.2", {"center": v(-3.3, -63) * mm, "radius": 3.5 * mm, "construction": true});
            skPoint(sketch, "E29.2.0.3", {"position": v(1.47, 33.25) * mm});
            skPoint(sketch, "E29.2.0.4", {"position": v(1.47, -11.76) * mm});
            skPoint(sketch, "E29.2.0.5", {"position": v(1.47, 42.24) * mm});
            skCircle(sketch, "E29.2.0.6", {"center": v(-3.3, 54) * mm, "radius": 3.5 * mm, "construction": true});
            skPoint(sketch, "E29.2.0.7", {"position": v(1.47, -29.76) * mm});
            skLineSegment(sketch, "E29.2.0.8", {"start": v(2.48, -55) * mm, "end": v(6.52, -55) * mm});
            skPoint(sketch, "E29.2.0.9", {"position": v(1.47, -56.75) * mm});
            skLineSegment(sketch, "E29.2.0.10", {"start": v(-5.31, -41.5) * mm, "end": v(-1.27, -41.5) * mm});
            skCircle(sketch, "E29.2.0.11", {"center": v(-3.3, -72) * mm, "radius": 3.5 * mm, "construction": true});
            skCircle(sketch, "E29.2.0.12", {"center": v(-3.3, -36) * mm, "radius": 3.5 * mm, "construction": true});
            skCircle(sketch, "E29.2.0.13", {"center": v(4.5, 94.5) * mm, "radius": 3.5 * mm, "construction": true});
            skPoint(sketch, "E29.2.0.14", {"position": v(1.47, -92.75) * mm});
            skCircle(sketch, "E29.2.0.15", {"center": v(-3.3, 63) * mm, "radius": 3.5 * mm, "construction": true});
            skCircle(sketch, "E29.2.0.16", {"center": v(-3.3, -9) * mm, "radius": 3.5 * mm, "construction": true});
            skLineSegment(sketch, "E29.2.0.17", {"start": v(-5.31, -32.5) * mm, "end": v(-1.27, -32.5) * mm});
            skPoint(sketch, "E29.2.0.18", {"position": v(1.47, -74.75) * mm});
            skCircle(sketch, "E29.2.0.19", {"center": v(-3.3, -90) * mm, "radius": 3.5 * mm, "construction": true});
            skLineSegment(sketch, "E29.2.0.20", {"start": v(-5.31, -59.5) * mm, "end": v(-1.27, -59.5) * mm});
            skCircle(sketch, "E29.2.0.21", {"center": v(-3.3, 99) * mm, "radius": 3.5 * mm, "construction": true});
            skPoint(sketch, "E29.2.0.22", {"position": v(-3.3, -95.5) * mm});
            skCircle(sketch, "E29.2.0.23", {"center": v(-3.3, -99) * mm, "radius": 3.5 * mm, "construction": true});
            skLineSegment(sketch, "E29.2.0.24", {"start": v(-5.31, -77.5) * mm, "end": v(-1.27, -77.5) * mm});
            skCircle(sketch, "E29.2.0.25", {"center": v(4.5, 13.5) * mm, "radius": 3.5 * mm, "construction": true});
            skCircle(sketch, "E29.2.0.26", {"center": v(-3.3, -81) * mm, "radius": 3.5 * mm, "construction": true});
            skLineSegment(sketch, "E29.2.0.27", {"start": v(2.48, -73) * mm, "end": v(6.52, -73) * mm});
            skCircle(sketch, "E29.2.0.28", {"center": v(-3.3, 9) * mm, "radius": 3.5 * mm, "construction": true});
            skLineSegment(sketch, "E29.2.0.29", {"start": v(2.48, -37) * mm, "end": v(6.52, -37) * mm});
            skPoint(sketch, "E29.2.0.30", {"position": v(1.47, 51.25) * mm});
            skCircle(sketch, "E29.2.0.31", {"center": v(4.5, 76.5) * mm, "radius": 3.5 * mm, "construction": true});
            skCircle(sketch, "E29.2.0.32", {"center": v(4.5, -58.5) * mm, "radius": 3.5 * mm, "construction": true});
            skCircle(sketch, "E29.2.0.33", {"center": v(4.5, -49.5) * mm, "radius": 3.5 * mm, "construction": true});
            skPoint(sketch, "E29.2.0.34", {"position": v(1.47, 78.24) * mm});
            skLineSegment(sketch, "E29.2.0.35", {"start": v(-5.31, -86.5) * mm, "end": v(-1.27, -86.5) * mm});
            skCircle(sketch, "E29.2.0.36", {"center": v(4.5, -40.5) * mm, "radius": 3.5 * mm, "construction": true});
            skCircle(sketch, "E29.2.0.37", {"center": v(4.5, -94.5) * mm, "radius": 3.5 * mm, "construction": true});
            skCircle(sketch, "E29.2.0.38", {"center": v(4.5, -13.5) * mm, "radius": 3.5 * mm, "construction": true});
            skPoint(sketch, "E29.2.0.39", {"position": v(1.47, 60.24) * mm});
            skPoint(sketch, "E29.2.0.40", {"position": v(1.47, 15.25) * mm});
            skLineSegment(sketch, "E29.2.0.41", {"start": v(-5.31, -50.5) * mm, "end": v(-1.27, -50.5) * mm});
            skCircle(sketch, "E29.2.0.42", {"center": v(4.5, -85.5) * mm, "radius": 3.5 * mm, "construction": true});
            skCircle(sketch, "E29.2.0.43", {"center": v(4.5, 31.5) * mm, "radius": 3.5 * mm, "construction": true});
            skCircle(sketch, "E29.2.0.44", {"center": v(-3.3, 36) * mm, "radius": 3.5 * mm, "construction": true});
            skCircle(sketch, "E29.2.0.45", {"center": v(4.5, -76.5) * mm, "radius": 3.5 * mm, "construction": true});
            skPoint(sketch, "E29.2.0.46", {"position": v(1.47, 96.24) * mm});
            skPoint(sketch, "E29.2.0.47", {"position": v(1.47, -2.75) * mm});
            skPoint(sketch, "E29.2.0.48", {"position": v(1.47, -83.76) * mm});
            skCircle(sketch, "E29.2.0.49", {"center": v(-3.3, -45) * mm, "radius": 3.5 * mm, "construction": true});
            skCircle(sketch, "E29.2.0.50", {"center": v(-3.3, 45) * mm, "radius": 3.5 * mm, "construction": true});
            skPoint(sketch, "E29.2.0.51", {"position": v(1.47, -20.75) * mm});
            skCircle(sketch, "E29.2.0.52", {"center": v(4.5, 67.5) * mm, "radius": 3.5 * mm, "construction": true});
            skLineSegment(sketch, "E29.2.0.53", {"start": v(2.47, -64) * mm, "end": v(6.51, -64) * mm});
            skLineSegment(sketch, "E29.2.0.54", {"start": v(-5.31, -68.5) * mm, "end": v(-1.27, -68.5) * mm});
            skCircle(sketch, "E29.2.0.55", {"center": v(-3.3, 27) * mm, "radius": 3.5 * mm, "construction": true});
            skCircle(sketch, "E29.2.0.56", {"center": v(4.5, -67.5) * mm, "radius": 3.5 * mm, "construction": true});
            skCircle(sketch, "E29.2.0.57", {"center": v(-3.3, -54) * mm, "radius": 3.5 * mm, "construction": true});
            skCircle(sketch, "E29.2.0.58", {"center": v(4.5, 85.5) * mm, "radius": 3.5 * mm, "construction": true});
            skCircle(sketch, "E29.2.0.59", {"center": v(-3.3, 90) * mm, "radius": 3.5 * mm, "construction": true});
            skPoint(sketch, "E29.2.0.60", {"position": v(1.47, -47.76) * mm});
            skCircle(sketch, "E29.2.0.61", {"center": v(-3.3, -18) * mm, "radius": 3.5 * mm, "construction": true});
            skCircle(sketch, "E29.2.0.62", {"center": v(4.5, -31.5) * mm, "radius": 3.5 * mm, "construction": true});
            skPoint(sketch, "E29.2.0.63", {"position": v(1.47, 24.24) * mm});
            skLineSegment(sketch, "E29.2.0.64", {"start": v(2.47, -28) * mm, "end": v(6.51, -28) * mm});
            skCircle(sketch, "E29.2.0.65", {"center": v(-3.3, 81) * mm, "radius": 3.5 * mm, "construction": true});
            skPoint(sketch, "E29.2.0.66", {"position": v(1.47, 6.24) * mm});
            skPoint(sketch, "E29.2.0.67", {"position": v(1.47, 87.25) * mm});
            skCircle(sketch, "E29.2.0.68", {"center": v(-3.3, 72) * mm, "radius": 3.5 * mm, "construction": true});
            skPoint(sketch, "E29.2.0.69", {"position": v(1.47, 69.25) * mm});
            skLineSegment(sketch, "E29.2.0.70", {"start": v(-5.31, -23.5) * mm, "end": v(-1.27, -23.5) * mm});
            skPoint(sketch, "E29.2.0.71", {"position": v(1.47, -38.75) * mm});
            skCircle(sketch, "E29.2.0.72", {"center": v(4.5, 58.5) * mm, "radius": 3.5 * mm, "construction": true});
            skLineSegment(sketch, "E29.2.0.73", {"start": v(-5.31, -102.5) * mm, "end": v(-5.31, -93.5) * mm, "construction": true});
            skCircle(sketch, "E29.2.0.74", {"center": v(-3.3, 18) * mm, "radius": 3.5 * mm, "construction": true});
            skLineSegment(sketch, "E29.2.0.75", {"start": v(2.48, -91) * mm, "end": v(6.52, -91) * mm});
            skPoint(sketch, "E29.2.0.76", {"position": v(1.47, -65.76) * mm});
            skCircle(sketch, "E29.2.0.77", {"center": v(4.5, 4.5) * mm, "radius": 3.5 * mm, "construction": true});
            skCircle(sketch, "E29.2.0.78", {"center": v(-3.3, -27) * mm, "radius": 3.5 * mm, "construction": true});
            skCircle(sketch, "E29.2.0.79", {"center": v(4.5, -22.5) * mm, "radius": 3.5 * mm, "construction": true});
            skCircle(sketch, "E29.2.0.80", {"center": v(4.5, 40.5) * mm, "radius": 3.5 * mm, "construction": true});
            skCircle(sketch, "E29.2.0.81", {"center": v(4.5, 49.5) * mm, "radius": 3.5 * mm, "construction": true});
            skCircle(sketch, "E29.2.0.82", {"center": v(4.5, 22.5) * mm, "radius": 3.5 * mm, "construction": true});
            skLineSegment(sketch, "E29.2.0.83", {"start": v(2.48, -98) * mm, "end": v(2.48, -80) * mm, "construction": true});
            skCircle(sketch, "E29.2.0.84", {"center": v(4.5, -4.5) * mm, "radius": 3.5 * mm, "construction": true});
            skLineSegment(sketch, "E29.2.0.85", {"start": v(6.51, -10) * mm, "end": v(8.54, -13.5) * mm});
            skLineSegment(sketch, "E29.2.0.86", {"start": v(-1.27, -59.5) * mm, "end": v(0.75, -63) * mm});
            skLineSegment(sketch, "E29.2.0.87", {"start": v(-1.27, -12.5) * mm, "end": v(-5.31, -12.5) * mm});
            skLineSegment(sketch, "E29.2.0.88", {"start": v(6.53, -17) * mm, "end": v(2.49, -17) * mm});
            skLineSegment(sketch, "E29.2.0.89", {"start": v(-1.27, -23.5) * mm, "end": v(0.75, -27) * mm});
            skLineSegment(sketch, "E29.2.0.90", {"start": v(-1.27, -68.5) * mm, "end": v(0.75, -72) * mm});
            skLineSegment(sketch, "E29.2.0.91", {"start": v(6.52, 28) * mm, "end": v(2.48, 28) * mm});
            skLineSegment(sketch, "E29.2.0.92", {"start": v(6.53, -89) * mm, "end": v(2.49, -89) * mm});
            skLineSegment(sketch, "E29.2.0.93", {"start": v(-1.27, -41.5) * mm, "end": v(0.75, -45) * mm});
            skLineSegment(sketch, "E29.2.0.94", {"start": v(-1.27, 14.5) * mm, "end": v(-5.31, 14.5) * mm});
            skLineSegment(sketch, "E29.2.0.95", {"start": v(6.52, -8) * mm, "end": v(2.48, -8) * mm});
            skLineSegment(sketch, "E29.2.0.96", {"start": v(0.46, -94.5) * mm, "end": v(2.48, -91) * mm});
            skLineSegment(sketch, "E29.2.0.97", {"start": v(-5.31, 30.5) * mm, "end": v(-1.27, 30.5) * mm});
            skLineSegment(sketch, "E29.2.0.98", {"start": v(-7.34, -63) * mm, "end": v(-5.31, -59.5) * mm});
            skLineSegment(sketch, "E29.2.0.99", {"start": v(6.51, -28) * mm, "end": v(8.54, -31.5) * mm});
            skLineSegment(sketch, "E29.2.0.100", {"start": v(-5.31, -14.5) * mm, "end": v(-1.27, -14.5) * mm});
            skLineSegment(sketch, "E29.2.0.101", {"start": v(-5.31, -95.5) * mm, "end": v(-1.27, -95.5) * mm});
            skLineSegment(sketch, "E29.2.0.102", {"start": v(-1.27, 77.5) * mm, "end": v(-5.31, 77.5) * mm});
            skLineSegment(sketch, "E29.2.0.103", {"start": v(-1.27, -95.5) * mm, "end": v(0.75, -99) * mm});
            skLineSegment(sketch, "E29.2.0.104", {"start": v(-7.34, -81) * mm, "end": v(-5.31, -77.5) * mm});
            skLineSegment(sketch, "E29.2.0.105", {"start": v(6.51, -64) * mm, "end": v(8.54, -67.5) * mm});
            skLineSegment(sketch, "E29.2.0.106", {"start": v(2.48, 17) * mm, "end": v(6.52, 17) * mm});
            skLineSegment(sketch, "E29.2.0.107", {"start": v(-1.27, 32.5) * mm, "end": v(-5.31, 32.5) * mm});
            skLineSegment(sketch, "E29.2.0.108", {"start": v(-1.27, 50.5) * mm, "end": v(-5.31, 50.5) * mm});
            skLineSegment(sketch, "E29.2.0.109", {"start": v(-7.34, -45) * mm, "end": v(-5.31, -41.5) * mm});
            skLineSegment(sketch, "E29.2.0.110", {"start": v(-1.27, -21.5) * mm, "end": v(-5.31, -21.5) * mm});
            skLineSegment(sketch, "E29.2.0.111", {"start": v(2.48, 71) * mm, "end": v(6.52, 71) * mm});
            skLineSegment(sketch, "E29.2.0.112", {"start": v(6.52, 10) * mm, "end": v(2.48, 10) * mm});
            skLineSegment(sketch, "E29.2.0.113", {"start": v(6.53, -71) * mm, "end": v(2.49, -71) * mm});
            skLineSegment(sketch, "E29.2.0.114", {"start": v(0.46, -40.5) * mm, "end": v(2.48, -37) * mm});
            skLineSegment(sketch, "E29.2.0.115", {"start": v(2.47, 80) * mm, "end": v(6.51, 80) * mm});
            skLineSegment(sketch, "E29.2.0.116", {"start": v(6.52, 46) * mm, "end": v(2.48, 46) * mm});
            skLineSegment(sketch, "E29.2.0.117", {"start": v(6.52, 82) * mm, "end": v(2.48, 82) * mm});
            skLineSegment(sketch, "E29.2.0.118", {"start": v(6.53, -53) * mm, "end": v(2.49, -53) * mm});
            skLineSegment(sketch, "E29.2.0.119", {"start": v(6.52, -26) * mm, "end": v(2.48, -26) * mm});
            skLineSegment(sketch, "E29.2.0.120", {"start": v(-1.27, -93.5) * mm, "end": v(-5.31, -93.5) * mm});
            skLineSegment(sketch, "E29.2.0.121", {"start": v(6.52, 64) * mm, "end": v(2.48, 64) * mm});
            skLineSegment(sketch, "E29.2.0.122", {"start": v(6.53, 37) * mm, "end": v(2.49, 37) * mm});
            skLineSegment(sketch, "E29.2.0.123", {"start": v(-1.27, -75.5) * mm, "end": v(-5.31, -75.5) * mm});
            skLineSegment(sketch, "E29.2.0.124", {"start": v(-5.31, 21.5) * mm, "end": v(-1.27, 21.5) * mm});
            skLineSegment(sketch, "E29.2.0.125", {"start": v(6.53, 91) * mm, "end": v(2.49, 91) * mm});
            skLineSegment(sketch, "E29.2.0.126", {"start": v(0.46, -67.5) * mm, "end": v(2.47, -64) * mm});
            skLineSegment(sketch, "E29.2.0.127", {"start": v(6.52, -44) * mm, "end": v(2.48, -44) * mm});
            skLineSegment(sketch, "E29.2.0.128", {"start": v(-1.27, 41.5) * mm, "end": v(-5.31, 41.5) * mm});
            skLineSegment(sketch, "E29.2.0.129", {"start": v(6.52, -80) * mm, "end": v(2.48, -80) * mm});
            skLineSegment(sketch, "E29.2.0.130", {"start": v(2.47, 98) * mm, "end": v(6.51, 98) * mm});
            skLineSegment(sketch, "E29.2.0.131", {"start": v(-1.27, 86.5) * mm, "end": v(-5.31, 86.5) * mm});
            skLineSegment(sketch, "E29.2.0.132", {"start": v(6.53, 73) * mm, "end": v(2.49, 73) * mm});
            skLineSegment(sketch, "E29.2.0.133", {"start": v(6.51, -46) * mm, "end": v(8.54, -49.5) * mm});
            skLineSegment(sketch, "E29.2.0.134", {"start": v(-1.27, -84.5) * mm, "end": v(-5.31, -84.5) * mm});
            skLineSegment(sketch, "E29.2.0.135", {"start": v(-1.27, -30.5) * mm, "end": v(-5.31, -30.5) * mm});
            skLineSegment(sketch, "E29.2.0.136", {"start": v(-7.34, -27) * mm, "end": v(-5.31, -23.5) * mm});
            skLineSegment(sketch, "E29.2.0.137", {"start": v(-5.31, 84.5) * mm, "end": v(-1.27, 84.5) * mm});
            skLineSegment(sketch, "E29.2.0.138", {"start": v(-5.31, 75.5) * mm, "end": v(-1.27, 75.5) * mm});
            skLineSegment(sketch, "E29.2.0.139", {"start": v(2.47, -82) * mm, "end": v(6.51, -82) * mm});
            skLineSegment(sketch, "E29.2.0.140", {"start": v(-1.27, -66.5) * mm, "end": v(-5.31, -66.5) * mm});
            skLineSegment(sketch, "E29.2.0.141", {"start": v(6.53, 19) * mm, "end": v(2.49, 19) * mm});
            skLineSegment(sketch, "E29.2.0.142", {"start": v(2.47, -10) * mm, "end": v(6.51, -10) * mm});
            skLineSegment(sketch, "E29.2.0.143", {"start": v(-1.27, -32.5) * mm, "end": v(0.75, -36) * mm});
            skLineSegment(sketch, "E29.2.0.144", {"start": v(2.48, -1) * mm, "end": v(6.52, -1) * mm});
            skLineSegment(sketch, "E29.2.0.145", {"start": v(6.52, -98) * mm, "end": v(2.48, -98) * mm});
            skLineSegment(sketch, "E29.2.0.146", {"start": v(-1.27, 59.5) * mm, "end": v(-5.31, 59.5) * mm});
            skLineSegment(sketch, "E29.2.0.147", {"start": v(6.53, 1) * mm, "end": v(2.49, 1) * mm});
            skLineSegment(sketch, "E29.2.0.148", {"start": v(-7.34, -99) * mm, "end": v(-5.31, -95.5) * mm});
            skLineSegment(sketch, "E29.2.0.149", {"start": v(-1.27, -39.5) * mm, "end": v(-5.31, -39.5) * mm});
            skLineSegment(sketch, "E29.2.0.150", {"start": v(2.47, 26) * mm, "end": v(6.51, 26) * mm});
            skLineSegment(sketch, "E29.2.0.151", {"start": v(6.52, -37) * mm, "end": v(8.54, -40.5) * mm});
            skLineSegment(sketch, "E29.2.0.152", {"start": v(2.48, -19) * mm, "end": v(6.52, -19) * mm});
            skLineSegment(sketch, "E29.2.0.153", {"start": v(0.46, -85.5) * mm, "end": v(2.47, -82) * mm});
            skLineSegment(sketch, "E29.2.0.154", {"start": v(2.47, 44) * mm, "end": v(6.51, 44) * mm});
            skLineSegment(sketch, "E29.2.0.155", {"start": v(-1.27, 23.5) * mm, "end": v(-5.31, 23.5) * mm});
            skLineSegment(sketch, "E29.2.0.156", {"start": v(-1.27, -3.5) * mm, "end": v(-5.31, -3.5) * mm});
            skLineSegment(sketch, "E29.2.0.157", {"start": v(-7.34, -72) * mm, "end": v(-5.31, -68.5) * mm});
            skLineSegment(sketch, "E29.2.0.158", {"start": v(6.52, -91) * mm, "end": v(8.54, -94.5) * mm});
            skLineSegment(sketch, "E29.2.0.159", {"start": v(-7.34, -54) * mm, "end": v(-5.31, -50.5) * mm});
            skLineSegment(sketch, "E29.2.0.160", {"start": v(0.46, -76.5) * mm, "end": v(2.48, -73) * mm});
            skLineSegment(sketch, "E29.2.0.161", {"start": v(2.47, 62) * mm, "end": v(6.51, 62) * mm});
            skLineSegment(sketch, "E29.2.0.162", {"start": v(6.51, -82) * mm, "end": v(8.54, -85.5) * mm});
            skLineSegment(sketch, "E29.2.0.163", {"start": v(2.48, 53) * mm, "end": v(6.52, 53) * mm});
            skLineSegment(sketch, "E29.2.0.164", {"start": v(-7.34, -36) * mm, "end": v(-5.31, -32.5) * mm});
            skLineSegment(sketch, "E29.2.0.165", {"start": v(-5.31, 102.5) * mm, "end": v(-1.27, 102.5) * mm});
            skLineSegment(sketch, "E29.2.0.166", {"start": v(0.46, -58.5) * mm, "end": v(2.48, -55) * mm});
            skLineSegment(sketch, "E29.2.0.167", {"start": v(-1.27, -48.5) * mm, "end": v(-5.31, -48.5) * mm});
            skLineSegment(sketch, "E29.2.0.168", {"start": v(6.52, -55) * mm, "end": v(8.54, -58.5) * mm});
            skLineSegment(sketch, "E29.2.0.169", {"start": v(-5.31, 39.5) * mm, "end": v(-1.27, 39.5) * mm});
            skLineSegment(sketch, "E29.2.0.170", {"start": v(-1.27, -57.5) * mm, "end": v(-5.31, -57.5) * mm});
            skLineSegment(sketch, "E29.2.0.171", {"start": v(6.53, 55) * mm, "end": v(2.49, 55) * mm});
            skLineSegment(sketch, "E29.2.0.172", {"start": v(-5.31, 48.5) * mm, "end": v(-1.27, 48.5) * mm});
            skLineSegment(sketch, "E29.2.0.173", {"start": v(-5.31, 3.5) * mm, "end": v(-1.27, 3.5) * mm});
            skLineSegment(sketch, "E29.2.0.174", {"start": v(-5.31, 12.5) * mm, "end": v(-1.27, 12.5) * mm});
            skLineSegment(sketch, "E29.2.0.175", {"start": v(-1.27, -50.5) * mm, "end": v(0.75, -54) * mm});
            skLineSegment(sketch, "E29.2.0.176", {"start": v(-5.31, 93.5) * mm, "end": v(-1.27, 93.5) * mm});
            skLineSegment(sketch, "E29.2.0.177", {"start": v(2.48, 89) * mm, "end": v(6.52, 89) * mm});
            skLineSegment(sketch, "E29.2.0.178", {"start": v(-1.27, -77.5) * mm, "end": v(0.75, -81) * mm});
            skLineSegment(sketch, "E29.2.0.179", {"start": v(-1.27, 5.5) * mm, "end": v(-5.31, 5.5) * mm});
            skLineSegment(sketch, "E29.2.0.180", {"start": v(6.52, -73) * mm, "end": v(8.54, -76.5) * mm});
            skLineSegment(sketch, "E29.2.0.181", {"start": v(-1.27, -102.5) * mm, "end": v(-5.31, -102.5) * mm});
            skLineSegment(sketch, "E29.2.0.182", {"start": v(2.48, 35) * mm, "end": v(6.52, 35) * mm});
            skLineSegment(sketch, "E29.2.0.183", {"start": v(2.47, 8) * mm, "end": v(6.51, 8) * mm});
            skLineSegment(sketch, "E29.2.0.184", {"start": v(-5.31, -5.5) * mm, "end": v(-1.27, -5.5) * mm});
            skLineSegment(sketch, "E29.2.0.185", {"start": v(-1.27, -86.5) * mm, "end": v(0.75, -90) * mm});
            skLineSegment(sketch, "E29.2.0.186", {"start": v(-5.31, 57.5) * mm, "end": v(-1.27, 57.5) * mm});
            skLineSegment(sketch, "E29.2.0.187", {"start": v(-1.27, 68.5) * mm, "end": v(-5.31, 68.5) * mm});
            skLineSegment(sketch, "E29.2.0.188", {"start": v(6.52, -62) * mm, "end": v(2.48, -62) * mm});
            skLineSegment(sketch, "E29.2.0.189", {"start": v(0.46, -49.5) * mm, "end": v(2.47, -46) * mm});
            skLineSegment(sketch, "E29.2.0.190", {"start": v(-1.27, 95.5) * mm, "end": v(-5.31, 95.5) * mm});
            skLineSegment(sketch, "E29.2.0.191", {"start": v(-5.31, 66.5) * mm, "end": v(-1.27, 66.5) * mm});
            skLineSegment(sketch, "E29.2.0.192", {"start": v(-7.34, -90) * mm, "end": v(-5.31, -86.5) * mm});
            skLineSegment(sketch, "E29.2.0.193", {"start": v(6.53, -35) * mm, "end": v(2.49, -35) * mm});
            skLineSegment(sketch, "E29.2.0.194", {"start": v(8.54, 40.5) * mm, "end": v(6.53, 37) * mm});
            skLineSegment(sketch, "E29.2.0.195", {"start": v(2.49, 55) * mm, "end": v(0.46, 58.5) * mm});
            skLineSegment(sketch, "E29.2.0.196", {"start": v(-5.31, -84.5) * mm, "end": v(-7.34, -81) * mm});
            skLineSegment(sketch, "E29.2.0.197", {"start": v(8.54, -31.5) * mm, "end": v(6.53, -35) * mm});
            skLineSegment(sketch, "E29.2.0.198", {"start": v(-5.31, -66.5) * mm, "end": v(-7.34, -63) * mm});
            skLineSegment(sketch, "E29.2.0.199", {"start": v(8.54, -67.5) * mm, "end": v(6.53, -71) * mm});
            skLineSegment(sketch, "E29.2.0.200", {"start": v(8.54, -4.5) * mm, "end": v(6.52, -8) * mm});
            skLineSegment(sketch, "E29.2.0.201", {"start": v(2.48, -8) * mm, "end": v(0.46, -4.5) * mm});
            skLineSegment(sketch, "E29.2.0.202", {"start": v(6.51, 98) * mm, "end": v(8.54, 94.5) * mm});
            skLineSegment(sketch, "E29.2.0.203", {"start": v(2.49, 37) * mm, "end": v(0.46, 40.5) * mm});
            skLineSegment(sketch, "E29.2.0.204", {"start": v(-5.31, -39.5) * mm, "end": v(-7.34, -36) * mm});
            skLineSegment(sketch, "E29.2.0.205", {"start": v(-7.34, 72) * mm, "end": v(-5.31, 75.5) * mm});
            skLineSegment(sketch, "E29.2.0.206", {"start": v(8.54, -94.5) * mm, "end": v(6.52, -98) * mm});
            skLineSegment(sketch, "E29.2.0.207", {"start": v(0.75, -63) * mm, "end": v(-1.27, -66.5) * mm});
            skLineSegment(sketch, "E29.2.0.208", {"start": v(-5.31, 86.5) * mm, "end": v(-7.34, 90) * mm});
            skLineSegment(sketch, "E29.2.0.209", {"start": v(-7.34, 81) * mm, "end": v(-5.31, 84.5) * mm});
            skLineSegment(sketch, "E29.2.0.210", {"start": v(0.75, 72) * mm, "end": v(-1.27, 68.5) * mm});
            skLineSegment(sketch, "E29.2.0.211", {"start": v(-5.31, 23.5) * mm, "end": v(-7.34, 27) * mm});
            skLineSegment(sketch, "E29.2.0.212", {"start": v(0.46, -31.5) * mm, "end": v(2.47, -28) * mm});
            skLineSegment(sketch, "E29.2.0.213", {"start": v(8.54, 31.5) * mm, "end": v(6.52, 28) * mm});
            skLineSegment(sketch, "E29.2.0.214", {"start": v(2.48, 82) * mm, "end": v(0.46, 85.5) * mm});
            skLineSegment(sketch, "E29.2.0.215", {"start": v(2.48, 64) * mm, "end": v(0.46, 67.5) * mm});
            skLineSegment(sketch, "E29.2.0.216", {"start": v(0.46, 13.5) * mm, "end": v(2.48, 17) * mm});
            skLineSegment(sketch, "E29.2.0.217", {"start": v(0.46, -4.5) * mm, "end": v(2.48, -1) * mm});
            skLineSegment(sketch, "E29.2.0.218", {"start": v(2.49, -35) * mm, "end": v(0.46, -31.5) * mm});
            skLineSegment(sketch, "E29.2.0.219", {"start": v(-7.34, 18) * mm, "end": v(-5.31, 21.5) * mm});
            skLineSegment(sketch, "E29.2.0.220", {"start": v(8.54, -85.5) * mm, "end": v(6.53, -89) * mm});
            skLineSegment(sketch, "E29.2.0.221", {"start": v(0.46, 76.5) * mm, "end": v(2.47, 80) * mm});
            skLineSegment(sketch, "E29.2.0.222", {"start": v(-1.27, 84.5) * mm, "end": v(0.75, 81) * mm});
            skLineSegment(sketch, "E29.2.0.223", {"start": v(0.75, -9) * mm, "end": v(-1.27, -12.5) * mm});
            skLineSegment(sketch, "E29.2.0.224", {"start": v(-5.31, -57.5) * mm, "end": v(-7.34, -54) * mm});
            skLineSegment(sketch, "E29.2.0.225", {"start": v(8.54, -22.5) * mm, "end": v(6.52, -26) * mm});
            skLineSegment(sketch, "E29.2.0.226", {"start": v(-1.27, 3.5) * mm, "end": v(0.75, 0) * mm});
            skLineSegment(sketch, "E29.2.0.227", {"start": v(8.54, 94.5) * mm, "end": v(6.53, 91) * mm});
            skLineSegment(sketch, "E29.2.0.228", {"start": v(-5.31, 5.5) * mm, "end": v(-7.34, 9) * mm});
            skLineSegment(sketch, "E29.2.0.229", {"start": v(0.75, 90) * mm, "end": v(-1.27, 86.5) * mm});
            skLineSegment(sketch, "E29.2.0.230", {"start": v(-7.34, 45) * mm, "end": v(-5.31, 48.5) * mm});
            skLineSegment(sketch, "E29.2.0.231", {"start": v(6.52, 71) * mm, "end": v(8.54, 67.5) * mm});
            skLineSegment(sketch, "E29.2.0.232", {"start": v(-7.34, 0) * mm, "end": v(-5.31, 3.5) * mm});
            skLineSegment(sketch, "E29.2.0.233", {"start": v(-7.34, 54) * mm, "end": v(-5.31, 57.5) * mm});
            skLineSegment(sketch, "E29.2.0.234", {"start": v(0.46, 4.5) * mm, "end": v(2.47, 8) * mm});
            skLineSegment(sketch, "E29.2.0.235", {"start": v(6.51, 26) * mm, "end": v(8.54, 22.5) * mm});
            skLineSegment(sketch, "E29.2.0.236", {"start": v(-1.27, 75.5) * mm, "end": v(0.75, 72) * mm});
            skLineSegment(sketch, "E29.2.0.237", {"start": v(0.75, 99) * mm, "end": v(-1.27, 95.5) * mm});
            skLineSegment(sketch, "E29.2.0.238", {"start": v(-7.34, 90) * mm, "end": v(-5.31, 93.5) * mm});
            skLineSegment(sketch, "E29.2.0.239", {"start": v(0.75, -90) * mm, "end": v(-1.27, -93.5) * mm});
            skLineSegment(sketch, "E29.2.0.240", {"start": v(0.75, 45) * mm, "end": v(-1.27, 41.5) * mm});
            skLineSegment(sketch, "E29.2.0.241", {"start": v(0.46, 49.5) * mm, "end": v(2.48, 53) * mm});
            skLineSegment(sketch, "E29.2.0.242", {"start": v(-1.27, 57.5) * mm, "end": v(0.75, 54) * mm});
            skLineSegment(sketch, "E29.2.0.243", {"start": v(0.75, -54) * mm, "end": v(-1.27, -57.5) * mm});
            skLineSegment(sketch, "E29.2.0.244", {"start": v(0.75, 63) * mm, "end": v(-1.27, 59.5) * mm});
            skLineSegment(sketch, "E29.2.0.245", {"start": v(6.51, 8) * mm, "end": v(8.54, 4.5) * mm});
            skLineSegment(sketch, "E29.2.0.246", {"start": v(8.54, -76.5) * mm, "end": v(6.52, -80) * mm});
            skLineSegment(sketch, "E29.2.0.247", {"start": v(-7.34, 99) * mm, "end": v(-5.31, 102.5) * mm});
            skLineSegment(sketch, "E29.2.0.248", {"start": v(0.46, 40.5) * mm, "end": v(2.47, 44) * mm});
            skLineSegment(sketch, "E29.2.0.249", {"start": v(-5.31, -48.5) * mm, "end": v(-7.34, -45) * mm});
            skLineSegment(sketch, "E29.2.0.250", {"start": v(-5.31, 41.5) * mm, "end": v(-7.34, 45) * mm});
            skLineSegment(sketch, "E29.2.0.251", {"start": v(-5.31, -102.5) * mm, "end": v(-7.34, -99) * mm});
            skLineSegment(sketch, "E29.2.0.252", {"start": v(2.49, 91) * mm, "end": v(0.46, 94.5) * mm});
            skLineSegment(sketch, "E29.2.0.253", {"start": v(0.75, -18) * mm, "end": v(-1.27, -21.5) * mm});
            skLineSegment(sketch, "E29.2.0.254", {"start": v(2.49, -53) * mm, "end": v(0.46, -49.5) * mm});
            skLineSegment(sketch, "E29.2.0.255", {"start": v(2.48, -80) * mm, "end": v(0.46, -76.5) * mm});
            skLineSegment(sketch, "E29.2.0.256", {"start": v(8.54, 76.5) * mm, "end": v(6.53, 73) * mm});
            skLineSegment(sketch, "E29.2.0.257", {"start": v(6.52, 35) * mm, "end": v(8.54, 31.5) * mm});
            skLineSegment(sketch, "E29.2.0.258", {"start": v(6.51, 62) * mm, "end": v(8.54, 58.5) * mm});
            skLineSegment(sketch, "E29.2.0.259", {"start": v(-1.27, 30.5) * mm, "end": v(0.75, 27) * mm});
            skLineSegment(sketch, "E29.2.0.260", {"start": v(0.75, -99) * mm, "end": v(-1.27, -102.5) * mm});
            skLineSegment(sketch, "E29.2.0.261", {"start": v(-1.27, -14.5) * mm, "end": v(0.75, -18) * mm});
            skLineSegment(sketch, "E29.2.0.262", {"start": v(-1.27, 93.5) * mm, "end": v(0.75, 90) * mm});
            skLineSegment(sketch, "E29.2.0.263", {"start": v(-7.34, 9) * mm, "end": v(-5.31, 12.5) * mm});
            skLineSegment(sketch, "E29.2.0.264", {"start": v(8.54, 67.5) * mm, "end": v(6.52, 64) * mm});
            skLineSegment(sketch, "E29.2.0.265", {"start": v(2.48, -62) * mm, "end": v(0.46, -58.5) * mm});
            skLineSegment(sketch, "E29.2.0.266", {"start": v(-5.31, 68.5) * mm, "end": v(-7.34, 72) * mm});
            skLineSegment(sketch, "E29.2.0.267", {"start": v(2.49, -17) * mm, "end": v(0.46, -13.5) * mm});
            skLineSegment(sketch, "E29.2.0.268", {"start": v(8.54, 4.5) * mm, "end": v(6.53, 1) * mm});
            skLineSegment(sketch, "E29.2.0.269", {"start": v(6.51, 80) * mm, "end": v(8.54, 76.5) * mm});
            skLineSegment(sketch, "E29.2.0.270", {"start": v(0.75, -27) * mm, "end": v(-1.27, -30.5) * mm});
            skLineSegment(sketch, "E29.2.0.271", {"start": v(8.54, 13.5) * mm, "end": v(6.52, 10) * mm});
            skLineSegment(sketch, "E29.2.0.272", {"start": v(-5.31, 32.5) * mm, "end": v(-7.34, 36) * mm});
            skLineSegment(sketch, "E29.2.0.273", {"start": v(0.75, -72) * mm, "end": v(-1.27, -75.5) * mm});
            skLineSegment(sketch, "E29.2.0.274", {"start": v(-1.27, 39.5) * mm, "end": v(0.75, 36) * mm});
            skLineSegment(sketch, "E29.2.0.275", {"start": v(-1.27, 102.5) * mm, "end": v(0.75, 99) * mm});
            skLineSegment(sketch, "E29.2.0.276", {"start": v(0.75, 54) * mm, "end": v(-1.27, 50.5) * mm});
            skLineSegment(sketch, "E29.2.0.277", {"start": v(0.75, 81) * mm, "end": v(-1.27, 77.5) * mm});
            skLineSegment(sketch, "E29.2.0.278", {"start": v(0.75, 0) * mm, "end": v(-1.27, -3.5) * mm});
            skLineSegment(sketch, "E29.2.0.279", {"start": v(-7.34, 63) * mm, "end": v(-5.31, 66.5) * mm});
            skLineSegment(sketch, "E29.2.0.280", {"start": v(-1.27, 66.5) * mm, "end": v(0.75, 63) * mm});
            skLineSegment(sketch, "E29.2.0.281", {"start": v(-1.27, -5.5) * mm, "end": v(0.75, -9) * mm});
            skLineSegment(sketch, "E29.2.0.282", {"start": v(-5.31, -75.5) * mm, "end": v(-7.34, -72) * mm});
            skLineSegment(sketch, "E29.2.0.283", {"start": v(2.48, -26) * mm, "end": v(0.46, -22.5) * mm});
            skLineSegment(sketch, "E29.2.0.284", {"start": v(6.52, 17) * mm, "end": v(8.54, 13.5) * mm});
            skLineSegment(sketch, "E29.2.0.285", {"start": v(-1.27, 21.5) * mm, "end": v(0.75, 18) * mm});
            skLineSegment(sketch, "E29.2.0.286", {"start": v(8.54, -13.5) * mm, "end": v(6.53, -17) * mm});
            skLineSegment(sketch, "E29.2.0.287", {"start": v(8.54, -58.5) * mm, "end": v(6.52, -62) * mm});
            skLineSegment(sketch, "E29.2.0.288", {"start": v(8.54, 58.5) * mm, "end": v(6.53, 55) * mm});
            skLineSegment(sketch, "E29.2.0.289", {"start": v(6.52, 89) * mm, "end": v(8.54, 85.5) * mm});
            skLineSegment(sketch, "E29.2.0.290", {"start": v(8.54, 22.5) * mm, "end": v(6.53, 19) * mm});
            skLineSegment(sketch, "E29.2.0.291", {"start": v(-5.31, -93.5) * mm, "end": v(-7.34, -90) * mm});
            skLineSegment(sketch, "E29.2.0.292", {"start": v(-5.31, -3.5) * mm, "end": v(-7.34, 0) * mm});
            skLineSegment(sketch, "E29.2.0.293", {"start": v(0.75, 18) * mm, "end": v(-1.27, 14.5) * mm});
            skLineSegment(sketch, "E29.2.0.294", {"start": v(0.75, 36) * mm, "end": v(-1.27, 32.5) * mm});
            skLineSegment(sketch, "E29.2.0.295", {"start": v(6.52, -1) * mm, "end": v(8.54, -4.5) * mm});
            skLineSegment(sketch, "E29.2.0.296", {"start": v(8.54, -49.5) * mm, "end": v(6.53, -53) * mm});
            skLineSegment(sketch, "E29.2.0.297", {"start": v(0.75, -45) * mm, "end": v(-1.27, -48.5) * mm});
            skLineSegment(sketch, "E29.2.0.298", {"start": v(0.75, 27) * mm, "end": v(-1.27, 23.5) * mm});
            skLineSegment(sketch, "E29.2.0.299", {"start": v(8.54, 85.5) * mm, "end": v(6.52, 82) * mm});
            skLineSegment(sketch, "E29.2.0.300", {"start": v(-5.31, 95.5) * mm, "end": v(-7.34, 99) * mm});
            skLineSegment(sketch, "E29.2.0.301", {"start": v(0.75, -36) * mm, "end": v(-1.27, -39.5) * mm});
            skLineSegment(sketch, "E29.2.0.302", {"start": v(-7.34, 27) * mm, "end": v(-5.31, 30.5) * mm});
            skLineSegment(sketch, "E29.2.0.303", {"start": v(8.54, -40.5) * mm, "end": v(6.52, -44) * mm});
            skLineSegment(sketch, "E29.2.0.304", {"start": v(0.46, 85.5) * mm, "end": v(2.48, 89) * mm});
            skLineSegment(sketch, "E29.2.0.305", {"start": v(-5.31, 50.5) * mm, "end": v(-7.34, 54) * mm});
            skLineSegment(sketch, "E29.2.0.306", {"start": v(0.46, -22.5) * mm, "end": v(2.48, -19) * mm});
            skLineSegment(sketch, "E29.2.0.307", {"start": v(2.48, -44) * mm, "end": v(0.46, -40.5) * mm});
            skLineSegment(sketch, "E29.2.0.308", {"start": v(2.49, -89) * mm, "end": v(0.46, -85.5) * mm});
            skLineSegment(sketch, "E29.2.0.309", {"start": v(0.46, 31.5) * mm, "end": v(2.48, 35) * mm});
            skLineSegment(sketch, "E29.2.0.310", {"start": v(-7.34, 36) * mm, "end": v(-5.31, 39.5) * mm});
            skLineSegment(sketch, "E29.2.0.311", {"start": v(-5.31, -30.5) * mm, "end": v(-7.34, -27) * mm});
            skLineSegment(sketch, "E29.2.0.312", {"start": v(-7.34, -9) * mm, "end": v(-5.31, -5.5) * mm});
            skLineSegment(sketch, "E29.2.0.313", {"start": v(2.49, 19) * mm, "end": v(0.46, 22.5) * mm});
            skLineSegment(sketch, "E29.2.0.314", {"start": v(2.48, -98) * mm, "end": v(0.46, -94.5) * mm});
            skLineSegment(sketch, "E29.2.0.315", {"start": v(-5.31, 77.5) * mm, "end": v(-7.34, 81) * mm});
            skLineSegment(sketch, "E29.2.0.316", {"start": v(0.75, -81) * mm, "end": v(-1.27, -84.5) * mm});
            skLineSegment(sketch, "E29.2.0.317", {"start": v(6.51, 44) * mm, "end": v(8.54, 40.5) * mm});
            skLineSegment(sketch, "E29.2.0.318", {"start": v(0.46, -13.5) * mm, "end": v(2.47, -10) * mm});
            skLineSegment(sketch, "E29.2.0.319", {"start": v(6.52, 53) * mm, "end": v(8.54, 49.5) * mm});
            skLineSegment(sketch, "E29.2.0.320", {"start": v(2.49, 1) * mm, "end": v(0.46, 4.5) * mm});
            skLineSegment(sketch, "E29.2.0.321", {"start": v(-7.34, -18) * mm, "end": v(-5.31, -14.5) * mm});
            skLineSegment(sketch, "E29.2.0.322", {"start": v(2.49, 73) * mm, "end": v(0.46, 76.5) * mm});
            skLineSegment(sketch, "E29.2.0.323", {"start": v(2.48, 10) * mm, "end": v(0.46, 13.5) * mm});
            skLineSegment(sketch, "E29.2.0.324", {"start": v(0.46, 67.5) * mm, "end": v(2.48, 71) * mm});
            skLineSegment(sketch, "E29.2.0.325", {"start": v(2.48, 46) * mm, "end": v(0.46, 49.5) * mm});
            skLineSegment(sketch, "E29.2.0.326", {"start": v(-5.31, 59.5) * mm, "end": v(-7.34, 63) * mm});
            skLineSegment(sketch, "E29.2.0.327", {"start": v(0.75, 9) * mm, "end": v(-1.27, 5.5) * mm});
            skLineSegment(sketch, "E29.2.0.328", {"start": v(-1.27, 12.5) * mm, "end": v(0.75, 9) * mm});
            skLineSegment(sketch, "E29.2.0.329", {"start": v(-5.31, -21.5) * mm, "end": v(-7.34, -18) * mm});
            skLineSegment(sketch, "E29.2.0.330", {"start": v(2.48, 28) * mm, "end": v(0.46, 31.5) * mm});
            skLineSegment(sketch, "E29.2.0.331", {"start": v(8.54, 49.5) * mm, "end": v(6.52, 46) * mm});
            skLineSegment(sketch, "E29.2.0.332", {"start": v(0.46, 58.5) * mm, "end": v(2.47, 62) * mm});
            skLineSegment(sketch, "E29.2.0.333", {"start": v(-1.27, 48.5) * mm, "end": v(0.75, 45) * mm});
            skLineSegment(sketch, "E29.2.0.334", {"start": v(6.52, -19) * mm, "end": v(8.54, -22.5) * mm});
            skLineSegment(sketch, "E29.2.0.335", {"start": v(-5.31, 14.5) * mm, "end": v(-7.34, 18) * mm});
            skLineSegment(sketch, "E29.2.0.336", {"start": v(2.49, -71) * mm, "end": v(0.46, -67.5) * mm});
            skLineSegment(sketch, "E29.2.0.337", {"start": v(0.46, 94.5) * mm, "end": v(2.47, 98) * mm});
            skLineSegment(sketch, "E29.2.0.338", {"start": v(-5.31, -12.5) * mm, "end": v(-7.34, -9) * mm});
            skLineSegment(sketch, "E29.2.0.339", {"start": v(0.46, 22.5) * mm, "end": v(2.47, 26) * mm});
            skCircle(sketch, "E29.3.0.0", {"center": v(-18.3, 0) * mm, "radius": 3.5 * mm, "construction": true});
            skLineSegment(sketch, "E29.3.0.1", {"start": v(-12.53, -46) * mm, "end": v(-8.49, -46) * mm});
            skCircle(sketch, "E29.3.0.2", {"center": v(-18.3, -63) * mm, "radius": 3.5 * mm, "construction": true});
            skPoint(sketch, "E29.3.0.3", {"position": v(-13.53, 33.25) * mm});
            skPoint(sketch, "E29.3.0.4", {"position": v(-13.53, -11.76) * mm});
            skPoint(sketch, "E29.3.0.5", {"position": v(-13.53, 42.24) * mm});
            skCircle(sketch, "E29.3.0.6", {"center": v(-18.3, 54) * mm, "radius": 3.5 * mm, "construction": true});
            skPoint(sketch, "E29.3.0.7", {"position": v(-13.53, -29.76) * mm});
            skLineSegment(sketch, "E29.3.0.8", {"start": v(-12.52, -55) * mm, "end": v(-8.48, -55) * mm});
            skPoint(sketch, "E29.3.0.9", {"position": v(-13.53, -56.75) * mm});
            skLineSegment(sketch, "E29.3.0.10", {"start": v(-20.31, -41.5) * mm, "end": v(-16.27, -41.5) * mm});
            skCircle(sketch, "E29.3.0.11", {"center": v(-18.3, -72) * mm, "radius": 3.5 * mm, "construction": true});
            skCircle(sketch, "E29.3.0.12", {"center": v(-18.3, -36) * mm, "radius": 3.5 * mm, "construction": true});
            skCircle(sketch, "E29.3.0.13", {"center": v(-10.5, 94.5) * mm, "radius": 3.5 * mm, "construction": true});
            skPoint(sketch, "E29.3.0.14", {"position": v(-13.53, -92.75) * mm});
            skCircle(sketch, "E29.3.0.15", {"center": v(-18.3, 63) * mm, "radius": 3.5 * mm, "construction": true});
            skCircle(sketch, "E29.3.0.16", {"center": v(-18.3, -9) * mm, "radius": 3.5 * mm, "construction": true});
            skLineSegment(sketch, "E29.3.0.17", {"start": v(-20.31, -32.5) * mm, "end": v(-16.27, -32.5) * mm});
            skPoint(sketch, "E29.3.0.18", {"position": v(-13.53, -74.75) * mm});
            skCircle(sketch, "E29.3.0.19", {"center": v(-18.3, -90) * mm, "radius": 3.5 * mm, "construction": true});
            skLineSegment(sketch, "E29.3.0.20", {"start": v(-20.31, -59.5) * mm, "end": v(-16.27, -59.5) * mm});
            skCircle(sketch, "E29.3.0.21", {"center": v(-18.3, 99) * mm, "radius": 3.5 * mm, "construction": true});
            skPoint(sketch, "E29.3.0.22", {"position": v(-18.3, -95.5) * mm});
            skCircle(sketch, "E29.3.0.23", {"center": v(-18.3, -99) * mm, "radius": 3.5 * mm, "construction": true});
            skLineSegment(sketch, "E29.3.0.24", {"start": v(-20.31, -77.5) * mm, "end": v(-16.27, -77.5) * mm});
            skCircle(sketch, "E29.3.0.25", {"center": v(-10.5, 13.5) * mm, "radius": 3.5 * mm, "construction": true});
            skCircle(sketch, "E29.3.0.26", {"center": v(-18.3, -81) * mm, "radius": 3.5 * mm, "construction": true});
            skLineSegment(sketch, "E29.3.0.27", {"start": v(-12.52, -73) * mm, "end": v(-8.48, -73) * mm});
            skCircle(sketch, "E29.3.0.28", {"center": v(-18.3, 9) * mm, "radius": 3.5 * mm, "construction": true});
            skLineSegment(sketch, "E29.3.0.29", {"start": v(-12.52, -37) * mm, "end": v(-8.48, -37) * mm});
            skPoint(sketch, "E29.3.0.30", {"position": v(-13.53, 51.25) * mm});
            skCircle(sketch, "E29.3.0.31", {"center": v(-10.5, 76.5) * mm, "radius": 3.5 * mm, "construction": true});
            skCircle(sketch, "E29.3.0.32", {"center": v(-10.5, -58.5) * mm, "radius": 3.5 * mm, "construction": true});
            skCircle(sketch, "E29.3.0.33", {"center": v(-10.5, -49.5) * mm, "radius": 3.5 * mm, "construction": true});
            skPoint(sketch, "E29.3.0.34", {"position": v(-13.53, 78.24) * mm});
            skLineSegment(sketch, "E29.3.0.35", {"start": v(-20.31, -86.5) * mm, "end": v(-16.27, -86.5) * mm});
            skCircle(sketch, "E29.3.0.36", {"center": v(-10.5, -40.5) * mm, "radius": 3.5 * mm, "construction": true});
            skCircle(sketch, "E29.3.0.37", {"center": v(-10.5, -94.5) * mm, "radius": 3.5 * mm, "construction": true});
            skCircle(sketch, "E29.3.0.38", {"center": v(-10.5, -13.5) * mm, "radius": 3.5 * mm, "construction": true});
            skPoint(sketch, "E29.3.0.39", {"position": v(-13.53, 60.24) * mm});
            skPoint(sketch, "E29.3.0.40", {"position": v(-13.53, 15.25) * mm});
            skLineSegment(sketch, "E29.3.0.41", {"start": v(-20.31, -50.5) * mm, "end": v(-16.27, -50.5) * mm});
            skCircle(sketch, "E29.3.0.42", {"center": v(-10.5, -85.5) * mm, "radius": 3.5 * mm, "construction": true});
            skCircle(sketch, "E29.3.0.43", {"center": v(-10.5, 31.5) * mm, "radius": 3.5 * mm, "construction": true});
            skCircle(sketch, "E29.3.0.44", {"center": v(-18.3, 36) * mm, "radius": 3.5 * mm, "construction": true});
            skCircle(sketch, "E29.3.0.45", {"center": v(-10.5, -76.5) * mm, "radius": 3.5 * mm, "construction": true});
            skPoint(sketch, "E29.3.0.46", {"position": v(-13.53, 96.24) * mm});
            skPoint(sketch, "E29.3.0.47", {"position": v(-13.53, -2.75) * mm});
            skPoint(sketch, "E29.3.0.48", {"position": v(-13.53, -83.76) * mm});
            skCircle(sketch, "E29.3.0.49", {"center": v(-18.3, -45) * mm, "radius": 3.5 * mm, "construction": true});
            skCircle(sketch, "E29.3.0.50", {"center": v(-18.3, 45) * mm, "radius": 3.5 * mm, "construction": true});
            skPoint(sketch, "E29.3.0.51", {"position": v(-13.53, -20.75) * mm});
            skCircle(sketch, "E29.3.0.52", {"center": v(-10.5, 67.5) * mm, "radius": 3.5 * mm, "construction": true});
            skLineSegment(sketch, "E29.3.0.53", {"start": v(-12.53, -64) * mm, "end": v(-8.49, -64) * mm});
            skLineSegment(sketch, "E29.3.0.54", {"start": v(-20.31, -68.5) * mm, "end": v(-16.27, -68.5) * mm});
            skCircle(sketch, "E29.3.0.55", {"center": v(-18.3, 27) * mm, "radius": 3.5 * mm, "construction": true});
            skCircle(sketch, "E29.3.0.56", {"center": v(-10.5, -67.5) * mm, "radius": 3.5 * mm, "construction": true});
            skCircle(sketch, "E29.3.0.57", {"center": v(-18.3, -54) * mm, "radius": 3.5 * mm, "construction": true});
            skCircle(sketch, "E29.3.0.58", {"center": v(-10.5, 85.5) * mm, "radius": 3.5 * mm, "construction": true});
            skCircle(sketch, "E29.3.0.59", {"center": v(-18.3, 90) * mm, "radius": 3.5 * mm, "construction": true});
            skPoint(sketch, "E29.3.0.60", {"position": v(-13.53, -47.76) * mm});
            skCircle(sketch, "E29.3.0.61", {"center": v(-18.3, -18) * mm, "radius": 3.5 * mm, "construction": true});
            skCircle(sketch, "E29.3.0.62", {"center": v(-10.5, -31.5) * mm, "radius": 3.5 * mm, "construction": true});
            skPoint(sketch, "E29.3.0.63", {"position": v(-13.53, 24.24) * mm});
            skLineSegment(sketch, "E29.3.0.64", {"start": v(-12.53, -28) * mm, "end": v(-8.49, -28) * mm});
            skCircle(sketch, "E29.3.0.65", {"center": v(-18.3, 81) * mm, "radius": 3.5 * mm, "construction": true});
            skPoint(sketch, "E29.3.0.66", {"position": v(-13.53, 6.24) * mm});
            skPoint(sketch, "E29.3.0.67", {"position": v(-13.53, 87.25) * mm});
            skCircle(sketch, "E29.3.0.68", {"center": v(-18.3, 72) * mm, "radius": 3.5 * mm, "construction": true});
            skPoint(sketch, "E29.3.0.69", {"position": v(-13.53, 69.25) * mm});
            skLineSegment(sketch, "E29.3.0.70", {"start": v(-20.31, -23.5) * mm, "end": v(-16.27, -23.5) * mm});
            skPoint(sketch, "E29.3.0.71", {"position": v(-13.53, -38.75) * mm});
            skCircle(sketch, "E29.3.0.72", {"center": v(-10.5, 58.5) * mm, "radius": 3.5 * mm, "construction": true});
            skLineSegment(sketch, "E29.3.0.73", {"start": v(-20.31, -102.5) * mm, "end": v(-20.31, -93.5) * mm, "construction": true});
            skCircle(sketch, "E29.3.0.74", {"center": v(-18.3, 18) * mm, "radius": 3.5 * mm, "construction": true});
            skLineSegment(sketch, "E29.3.0.75", {"start": v(-12.52, -91) * mm, "end": v(-8.48, -91) * mm});
            skPoint(sketch, "E29.3.0.76", {"position": v(-13.53, -65.76) * mm});
            skCircle(sketch, "E29.3.0.77", {"center": v(-10.5, 4.5) * mm, "radius": 3.5 * mm, "construction": true});
            skCircle(sketch, "E29.3.0.78", {"center": v(-18.3, -27) * mm, "radius": 3.5 * mm, "construction": true});
            skCircle(sketch, "E29.3.0.79", {"center": v(-10.5, -22.5) * mm, "radius": 3.5 * mm, "construction": true});
            skCircle(sketch, "E29.3.0.80", {"center": v(-10.5, 40.5) * mm, "radius": 3.5 * mm, "construction": true});
            skCircle(sketch, "E29.3.0.81", {"center": v(-10.5, 49.5) * mm, "radius": 3.5 * mm, "construction": true});
            skCircle(sketch, "E29.3.0.82", {"center": v(-10.5, 22.5) * mm, "radius": 3.5 * mm, "construction": true});
            skLineSegment(sketch, "E29.3.0.83", {"start": v(-12.52, -98) * mm, "end": v(-12.52, -80) * mm, "construction": true});
            skCircle(sketch, "E29.3.0.84", {"center": v(-10.5, -4.5) * mm, "radius": 3.5 * mm, "construction": true});
            skLineSegment(sketch, "E29.3.0.85", {"start": v(-8.49, -10) * mm, "end": v(-6.46, -13.5) * mm});
            skLineSegment(sketch, "E29.3.0.86", {"start": v(-16.27, -59.5) * mm, "end": v(-14.25, -63) * mm});
            skLineSegment(sketch, "E29.3.0.87", {"start": v(-16.27, -12.5) * mm, "end": v(-20.31, -12.5) * mm});
            skLineSegment(sketch, "E29.3.0.88", {"start": v(-8.47, -17) * mm, "end": v(-12.51, -17) * mm});
            skLineSegment(sketch, "E29.3.0.89", {"start": v(-16.27, -23.5) * mm, "end": v(-14.25, -27) * mm});
            skLineSegment(sketch, "E29.3.0.90", {"start": v(-16.27, -68.5) * mm, "end": v(-14.25, -72) * mm});
            skLineSegment(sketch, "E29.3.0.91", {"start": v(-8.48, 28) * mm, "end": v(-12.52, 28) * mm});
            skLineSegment(sketch, "E29.3.0.92", {"start": v(-8.47, -89) * mm, "end": v(-12.51, -89) * mm});
            skLineSegment(sketch, "E29.3.0.93", {"start": v(-16.27, -41.5) * mm, "end": v(-14.25, -45) * mm});
            skLineSegment(sketch, "E29.3.0.94", {"start": v(-16.27, 14.5) * mm, "end": v(-20.31, 14.5) * mm});
            skLineSegment(sketch, "E29.3.0.95", {"start": v(-8.48, -8) * mm, "end": v(-12.52, -8) * mm});
            skLineSegment(sketch, "E29.3.0.96", {"start": v(-14.54, -94.5) * mm, "end": v(-12.52, -91) * mm});
            skLineSegment(sketch, "E29.3.0.97", {"start": v(-20.31, 30.5) * mm, "end": v(-16.27, 30.5) * mm});
            skLineSegment(sketch, "E29.3.0.98", {"start": v(-22.34, -63) * mm, "end": v(-20.31, -59.5) * mm});
            skLineSegment(sketch, "E29.3.0.99", {"start": v(-8.49, -28) * mm, "end": v(-6.46, -31.5) * mm});
            skLineSegment(sketch, "E29.3.0.100", {"start": v(-20.31, -14.5) * mm, "end": v(-16.27, -14.5) * mm});
            skLineSegment(sketch, "E29.3.0.101", {"start": v(-20.31, -95.5) * mm, "end": v(-16.27, -95.5) * mm});
            skLineSegment(sketch, "E29.3.0.102", {"start": v(-16.27, 77.5) * mm, "end": v(-20.31, 77.5) * mm});
            skLineSegment(sketch, "E29.3.0.103", {"start": v(-16.27, -95.5) * mm, "end": v(-14.25, -99) * mm});
            skLineSegment(sketch, "E29.3.0.104", {"start": v(-22.34, -81) * mm, "end": v(-20.31, -77.5) * mm});
            skLineSegment(sketch, "E29.3.0.105", {"start": v(-8.49, -64) * mm, "end": v(-6.46, -67.5) * mm});
            skLineSegment(sketch, "E29.3.0.106", {"start": v(-12.52, 17) * mm, "end": v(-8.48, 17) * mm});
            skLineSegment(sketch, "E29.3.0.107", {"start": v(-16.27, 32.5) * mm, "end": v(-20.31, 32.5) * mm});
            skLineSegment(sketch, "E29.3.0.108", {"start": v(-16.27, 50.5) * mm, "end": v(-20.31, 50.5) * mm});
            skLineSegment(sketch, "E29.3.0.109", {"start": v(-22.34, -45) * mm, "end": v(-20.31, -41.5) * mm});
            skLineSegment(sketch, "E29.3.0.110", {"start": v(-16.27, -21.5) * mm, "end": v(-20.31, -21.5) * mm});
            skLineSegment(sketch, "E29.3.0.111", {"start": v(-12.52, 71) * mm, "end": v(-8.48, 71) * mm});
            skLineSegment(sketch, "E29.3.0.112", {"start": v(-8.48, 10) * mm, "end": v(-12.52, 10) * mm});
            skLineSegment(sketch, "E29.3.0.113", {"start": v(-8.47, -71) * mm, "end": v(-12.51, -71) * mm});
            skLineSegment(sketch, "E29.3.0.114", {"start": v(-14.54, -40.5) * mm, "end": v(-12.52, -37) * mm});
            skLineSegment(sketch, "E29.3.0.115", {"start": v(-12.53, 80) * mm, "end": v(-8.49, 80) * mm});
            skLineSegment(sketch, "E29.3.0.116", {"start": v(-8.48, 46) * mm, "end": v(-12.52, 46) * mm});
            skLineSegment(sketch, "E29.3.0.117", {"start": v(-8.48, 82) * mm, "end": v(-12.52, 82) * mm});
            skLineSegment(sketch, "E29.3.0.118", {"start": v(-8.47, -53) * mm, "end": v(-12.51, -53) * mm});
            skLineSegment(sketch, "E29.3.0.119", {"start": v(-8.48, -26) * mm, "end": v(-12.52, -26) * mm});
            skLineSegment(sketch, "E29.3.0.120", {"start": v(-16.27, -93.5) * mm, "end": v(-20.31, -93.5) * mm});
            skLineSegment(sketch, "E29.3.0.121", {"start": v(-8.48, 64) * mm, "end": v(-12.52, 64) * mm});
            skLineSegment(sketch, "E29.3.0.122", {"start": v(-8.47, 37) * mm, "end": v(-12.51, 37) * mm});
            skLineSegment(sketch, "E29.3.0.123", {"start": v(-16.27, -75.5) * mm, "end": v(-20.31, -75.5) * mm});
            skLineSegment(sketch, "E29.3.0.124", {"start": v(-20.31, 21.5) * mm, "end": v(-16.27, 21.5) * mm});
            skLineSegment(sketch, "E29.3.0.125", {"start": v(-8.47, 91) * mm, "end": v(-12.51, 91) * mm});
            skLineSegment(sketch, "E29.3.0.126", {"start": v(-14.54, -67.5) * mm, "end": v(-12.53, -64) * mm});
            skLineSegment(sketch, "E29.3.0.127", {"start": v(-8.48, -44) * mm, "end": v(-12.52, -44) * mm});
            skLineSegment(sketch, "E29.3.0.128", {"start": v(-16.27, 41.5) * mm, "end": v(-20.31, 41.5) * mm});
            skLineSegment(sketch, "E29.3.0.129", {"start": v(-8.48, -80) * mm, "end": v(-12.52, -80) * mm});
            skLineSegment(sketch, "E29.3.0.130", {"start": v(-12.53, 98) * mm, "end": v(-8.49, 98) * mm});
            skLineSegment(sketch, "E29.3.0.131", {"start": v(-16.27, 86.5) * mm, "end": v(-20.31, 86.5) * mm});
            skLineSegment(sketch, "E29.3.0.132", {"start": v(-8.47, 73) * mm, "end": v(-12.51, 73) * mm});
            skLineSegment(sketch, "E29.3.0.133", {"start": v(-8.49, -46) * mm, "end": v(-6.46, -49.5) * mm});
            skLineSegment(sketch, "E29.3.0.134", {"start": v(-16.27, -84.5) * mm, "end": v(-20.31, -84.5) * mm});
            skLineSegment(sketch, "E29.3.0.135", {"start": v(-16.27, -30.5) * mm, "end": v(-20.31, -30.5) * mm});
            skLineSegment(sketch, "E29.3.0.136", {"start": v(-22.34, -27) * mm, "end": v(-20.31, -23.5) * mm});
            skLineSegment(sketch, "E29.3.0.137", {"start": v(-20.31, 84.5) * mm, "end": v(-16.27, 84.5) * mm});
            skLineSegment(sketch, "E29.3.0.138", {"start": v(-20.31, 75.5) * mm, "end": v(-16.27, 75.5) * mm});
            skLineSegment(sketch, "E29.3.0.139", {"start": v(-12.53, -82) * mm, "end": v(-8.49, -82) * mm});
            skLineSegment(sketch, "E29.3.0.140", {"start": v(-16.27, -66.5) * mm, "end": v(-20.31, -66.5) * mm});
            skLineSegment(sketch, "E29.3.0.141", {"start": v(-8.47, 19) * mm, "end": v(-12.51, 19) * mm});
            skLineSegment(sketch, "E29.3.0.142", {"start": v(-12.53, -10) * mm, "end": v(-8.49, -10) * mm});
            skLineSegment(sketch, "E29.3.0.143", {"start": v(-16.27, -32.5) * mm, "end": v(-14.25, -36) * mm});
            skLineSegment(sketch, "E29.3.0.144", {"start": v(-12.52, -1) * mm, "end": v(-8.48, -1) * mm});
            skLineSegment(sketch, "E29.3.0.145", {"start": v(-8.48, -98) * mm, "end": v(-12.52, -98) * mm});
            skLineSegment(sketch, "E29.3.0.146", {"start": v(-16.27, 59.5) * mm, "end": v(-20.31, 59.5) * mm});
            skLineSegment(sketch, "E29.3.0.147", {"start": v(-8.47, 1) * mm, "end": v(-12.51, 1) * mm});
            skLineSegment(sketch, "E29.3.0.148", {"start": v(-22.34, -99) * mm, "end": v(-20.31, -95.5) * mm});
            skLineSegment(sketch, "E29.3.0.149", {"start": v(-16.27, -39.5) * mm, "end": v(-20.31, -39.5) * mm});
            skLineSegment(sketch, "E29.3.0.150", {"start": v(-12.53, 26) * mm, "end": v(-8.49, 26) * mm});
            skLineSegment(sketch, "E29.3.0.151", {"start": v(-8.48, -37) * mm, "end": v(-6.46, -40.5) * mm});
            skLineSegment(sketch, "E29.3.0.152", {"start": v(-12.52, -19) * mm, "end": v(-8.48, -19) * mm});
            skLineSegment(sketch, "E29.3.0.153", {"start": v(-14.54, -85.5) * mm, "end": v(-12.53, -82) * mm});
            skLineSegment(sketch, "E29.3.0.154", {"start": v(-12.53, 44) * mm, "end": v(-8.49, 44) * mm});
            skLineSegment(sketch, "E29.3.0.155", {"start": v(-16.27, 23.5) * mm, "end": v(-20.31, 23.5) * mm});
            skLineSegment(sketch, "E29.3.0.156", {"start": v(-16.27, -3.5) * mm, "end": v(-20.31, -3.5) * mm});
            skLineSegment(sketch, "E29.3.0.157", {"start": v(-22.34, -72) * mm, "end": v(-20.31, -68.5) * mm});
            skLineSegment(sketch, "E29.3.0.158", {"start": v(-8.48, -91) * mm, "end": v(-6.46, -94.5) * mm});
            skLineSegment(sketch, "E29.3.0.159", {"start": v(-22.34, -54) * mm, "end": v(-20.31, -50.5) * mm});
            skLineSegment(sketch, "E29.3.0.160", {"start": v(-14.54, -76.5) * mm, "end": v(-12.52, -73) * mm});
            skLineSegment(sketch, "E29.3.0.161", {"start": v(-12.53, 62) * mm, "end": v(-8.49, 62) * mm});
            skLineSegment(sketch, "E29.3.0.162", {"start": v(-8.49, -82) * mm, "end": v(-6.46, -85.5) * mm});
            skLineSegment(sketch, "E29.3.0.163", {"start": v(-12.52, 53) * mm, "end": v(-8.48, 53) * mm});
            skLineSegment(sketch, "E29.3.0.164", {"start": v(-22.34, -36) * mm, "end": v(-20.31, -32.5) * mm});
            skLineSegment(sketch, "E29.3.0.165", {"start": v(-20.31, 102.5) * mm, "end": v(-16.27, 102.5) * mm});
            skLineSegment(sketch, "E29.3.0.166", {"start": v(-14.54, -58.5) * mm, "end": v(-12.52, -55) * mm});
            skLineSegment(sketch, "E29.3.0.167", {"start": v(-16.27, -48.5) * mm, "end": v(-20.31, -48.5) * mm});
            skLineSegment(sketch, "E29.3.0.168", {"start": v(-8.48, -55) * mm, "end": v(-6.46, -58.5) * mm});
            skLineSegment(sketch, "E29.3.0.169", {"start": v(-20.31, 39.5) * mm, "end": v(-16.27, 39.5) * mm});
            skLineSegment(sketch, "E29.3.0.170", {"start": v(-16.27, -57.5) * mm, "end": v(-20.31, -57.5) * mm});
            skLineSegment(sketch, "E29.3.0.171", {"start": v(-8.47, 55) * mm, "end": v(-12.51, 55) * mm});
            skLineSegment(sketch, "E29.3.0.172", {"start": v(-20.31, 48.5) * mm, "end": v(-16.27, 48.5) * mm});
            skLineSegment(sketch, "E29.3.0.173", {"start": v(-20.31, 3.5) * mm, "end": v(-16.27, 3.5) * mm});
            skLineSegment(sketch, "E29.3.0.174", {"start": v(-20.31, 12.5) * mm, "end": v(-16.27, 12.5) * mm});
            skLineSegment(sketch, "E29.3.0.175", {"start": v(-16.27, -50.5) * mm, "end": v(-14.25, -54) * mm});
            skLineSegment(sketch, "E29.3.0.176", {"start": v(-20.31, 93.5) * mm, "end": v(-16.27, 93.5) * mm});
            skLineSegment(sketch, "E29.3.0.177", {"start": v(-12.52, 89) * mm, "end": v(-8.48, 89) * mm});
            skLineSegment(sketch, "E29.3.0.178", {"start": v(-16.27, -77.5) * mm, "end": v(-14.25, -81) * mm});
            skLineSegment(sketch, "E29.3.0.179", {"start": v(-16.27, 5.5) * mm, "end": v(-20.31, 5.5) * mm});
            skLineSegment(sketch, "E29.3.0.180", {"start": v(-8.48, -73) * mm, "end": v(-6.46, -76.5) * mm});
            skLineSegment(sketch, "E29.3.0.181", {"start": v(-16.27, -102.5) * mm, "end": v(-20.31, -102.5) * mm});
            skLineSegment(sketch, "E29.3.0.182", {"start": v(-12.52, 35) * mm, "end": v(-8.48, 35) * mm});
            skLineSegment(sketch, "E29.3.0.183", {"start": v(-12.53, 8) * mm, "end": v(-8.49, 8) * mm});
            skLineSegment(sketch, "E29.3.0.184", {"start": v(-20.31, -5.5) * mm, "end": v(-16.27, -5.5) * mm});
            skLineSegment(sketch, "E29.3.0.185", {"start": v(-16.27, -86.5) * mm, "end": v(-14.25, -90) * mm});
            skLineSegment(sketch, "E29.3.0.186", {"start": v(-20.31, 57.5) * mm, "end": v(-16.27, 57.5) * mm});
            skLineSegment(sketch, "E29.3.0.187", {"start": v(-16.27, 68.5) * mm, "end": v(-20.31, 68.5) * mm});
            skLineSegment(sketch, "E29.3.0.188", {"start": v(-8.48, -62) * mm, "end": v(-12.52, -62) * mm});
            skLineSegment(sketch, "E29.3.0.189", {"start": v(-14.54, -49.5) * mm, "end": v(-12.53, -46) * mm});
            skLineSegment(sketch, "E29.3.0.190", {"start": v(-16.27, 95.5) * mm, "end": v(-20.31, 95.5) * mm});
            skLineSegment(sketch, "E29.3.0.191", {"start": v(-20.31, 66.5) * mm, "end": v(-16.27, 66.5) * mm});
            skLineSegment(sketch, "E29.3.0.192", {"start": v(-22.34, -90) * mm, "end": v(-20.31, -86.5) * mm});
            skLineSegment(sketch, "E29.3.0.193", {"start": v(-8.47, -35) * mm, "end": v(-12.51, -35) * mm});
            skLineSegment(sketch, "E29.3.0.194", {"start": v(-6.46, 40.5) * mm, "end": v(-8.47, 37) * mm});
            skLineSegment(sketch, "E29.3.0.195", {"start": v(-12.51, 55) * mm, "end": v(-14.54, 58.5) * mm});
            skLineSegment(sketch, "E29.3.0.196", {"start": v(-20.31, -84.5) * mm, "end": v(-22.34, -81) * mm});
            skLineSegment(sketch, "E29.3.0.197", {"start": v(-6.46, -31.5) * mm, "end": v(-8.47, -35) * mm});
            skLineSegment(sketch, "E29.3.0.198", {"start": v(-20.31, -66.5) * mm, "end": v(-22.34, -63) * mm});
            skLineSegment(sketch, "E29.3.0.199", {"start": v(-6.46, -67.5) * mm, "end": v(-8.47, -71) * mm});
            skLineSegment(sketch, "E29.3.0.200", {"start": v(-6.46, -4.5) * mm, "end": v(-8.48, -8) * mm});
            skLineSegment(sketch, "E29.3.0.201", {"start": v(-12.52, -8) * mm, "end": v(-14.54, -4.5) * mm});
            skLineSegment(sketch, "E29.3.0.202", {"start": v(-8.49, 98) * mm, "end": v(-6.46, 94.5) * mm});
            skLineSegment(sketch, "E29.3.0.203", {"start": v(-12.51, 37) * mm, "end": v(-14.54, 40.5) * mm});
            skLineSegment(sketch, "E29.3.0.204", {"start": v(-20.31, -39.5) * mm, "end": v(-22.34, -36) * mm});
            skLineSegment(sketch, "E29.3.0.205", {"start": v(-22.34, 72) * mm, "end": v(-20.31, 75.5) * mm});
            skLineSegment(sketch, "E29.3.0.206", {"start": v(-6.46, -94.5) * mm, "end": v(-8.48, -98) * mm});
            skLineSegment(sketch, "E29.3.0.207", {"start": v(-14.25, -63) * mm, "end": v(-16.27, -66.5) * mm});
            skLineSegment(sketch, "E29.3.0.208", {"start": v(-20.31, 86.5) * mm, "end": v(-22.34, 90) * mm});
            skLineSegment(sketch, "E29.3.0.209", {"start": v(-22.34, 81) * mm, "end": v(-20.31, 84.5) * mm});
            skLineSegment(sketch, "E29.3.0.210", {"start": v(-14.25, 72) * mm, "end": v(-16.27, 68.5) * mm});
            skLineSegment(sketch, "E29.3.0.211", {"start": v(-20.31, 23.5) * mm, "end": v(-22.34, 27) * mm});
            skLineSegment(sketch, "E29.3.0.212", {"start": v(-14.54, -31.5) * mm, "end": v(-12.53, -28) * mm});
            skLineSegment(sketch, "E29.3.0.213", {"start": v(-6.46, 31.5) * mm, "end": v(-8.48, 28) * mm});
            skLineSegment(sketch, "E29.3.0.214", {"start": v(-12.52, 82) * mm, "end": v(-14.54, 85.5) * mm});
            skLineSegment(sketch, "E29.3.0.215", {"start": v(-12.52, 64) * mm, "end": v(-14.54, 67.5) * mm});
            skLineSegment(sketch, "E29.3.0.216", {"start": v(-14.54, 13.5) * mm, "end": v(-12.52, 17) * mm});
            skLineSegment(sketch, "E29.3.0.217", {"start": v(-14.54, -4.5) * mm, "end": v(-12.52, -1) * mm});
            skLineSegment(sketch, "E29.3.0.218", {"start": v(-12.51, -35) * mm, "end": v(-14.54, -31.5) * mm});
            skLineSegment(sketch, "E29.3.0.219", {"start": v(-22.34, 18) * mm, "end": v(-20.31, 21.5) * mm});
            skLineSegment(sketch, "E29.3.0.220", {"start": v(-6.46, -85.5) * mm, "end": v(-8.47, -89) * mm});
            skLineSegment(sketch, "E29.3.0.221", {"start": v(-14.54, 76.5) * mm, "end": v(-12.53, 80) * mm});
            skLineSegment(sketch, "E29.3.0.222", {"start": v(-16.27, 84.5) * mm, "end": v(-14.25, 81) * mm});
            skLineSegment(sketch, "E29.3.0.223", {"start": v(-14.25, -9) * mm, "end": v(-16.27, -12.5) * mm});
            skLineSegment(sketch, "E29.3.0.224", {"start": v(-20.31, -57.5) * mm, "end": v(-22.34, -54) * mm});
            skLineSegment(sketch, "E29.3.0.225", {"start": v(-6.46, -22.5) * mm, "end": v(-8.48, -26) * mm});
            skLineSegment(sketch, "E29.3.0.226", {"start": v(-16.27, 3.5) * mm, "end": v(-14.25, 0) * mm});
            skLineSegment(sketch, "E29.3.0.227", {"start": v(-6.46, 94.5) * mm, "end": v(-8.47, 91) * mm});
            skLineSegment(sketch, "E29.3.0.228", {"start": v(-20.31, 5.5) * mm, "end": v(-22.34, 9) * mm});
            skLineSegment(sketch, "E29.3.0.229", {"start": v(-14.25, 90) * mm, "end": v(-16.27, 86.5) * mm});
            skLineSegment(sketch, "E29.3.0.230", {"start": v(-22.34, 45) * mm, "end": v(-20.31, 48.5) * mm});
            skLineSegment(sketch, "E29.3.0.231", {"start": v(-8.48, 71) * mm, "end": v(-6.46, 67.5) * mm});
            skLineSegment(sketch, "E29.3.0.232", {"start": v(-22.34, 0) * mm, "end": v(-20.31, 3.5) * mm});
            skLineSegment(sketch, "E29.3.0.233", {"start": v(-22.34, 54) * mm, "end": v(-20.31, 57.5) * mm});
            skLineSegment(sketch, "E29.3.0.234", {"start": v(-14.54, 4.5) * mm, "end": v(-12.53, 8) * mm});
            skLineSegment(sketch, "E29.3.0.235", {"start": v(-8.49, 26) * mm, "end": v(-6.46, 22.5) * mm});
            skLineSegment(sketch, "E29.3.0.236", {"start": v(-16.27, 75.5) * mm, "end": v(-14.25, 72) * mm});
            skLineSegment(sketch, "E29.3.0.237", {"start": v(-14.25, 99) * mm, "end": v(-16.27, 95.5) * mm});
            skLineSegment(sketch, "E29.3.0.238", {"start": v(-22.34, 90) * mm, "end": v(-20.31, 93.5) * mm});
            skLineSegment(sketch, "E29.3.0.239", {"start": v(-14.25, -90) * mm, "end": v(-16.27, -93.5) * mm});
            skLineSegment(sketch, "E29.3.0.240", {"start": v(-14.25, 45) * mm, "end": v(-16.27, 41.5) * mm});
            skLineSegment(sketch, "E29.3.0.241", {"start": v(-14.54, 49.5) * mm, "end": v(-12.52, 53) * mm});
            skLineSegment(sketch, "E29.3.0.242", {"start": v(-16.27, 57.5) * mm, "end": v(-14.25, 54) * mm});
            skLineSegment(sketch, "E29.3.0.243", {"start": v(-14.25, -54) * mm, "end": v(-16.27, -57.5) * mm});
            skLineSegment(sketch, "E29.3.0.244", {"start": v(-14.25, 63) * mm, "end": v(-16.27, 59.5) * mm});
            skLineSegment(sketch, "E29.3.0.245", {"start": v(-8.49, 8) * mm, "end": v(-6.46, 4.5) * mm});
            skLineSegment(sketch, "E29.3.0.246", {"start": v(-6.46, -76.5) * mm, "end": v(-8.48, -80) * mm});
            skLineSegment(sketch, "E29.3.0.247", {"start": v(-22.34, 99) * mm, "end": v(-20.31, 102.5) * mm});
            skLineSegment(sketch, "E29.3.0.248", {"start": v(-14.54, 40.5) * mm, "end": v(-12.53, 44) * mm});
            skLineSegment(sketch, "E29.3.0.249", {"start": v(-20.31, -48.5) * mm, "end": v(-22.34, -45) * mm});
            skLineSegment(sketch, "E29.3.0.250", {"start": v(-20.31, 41.5) * mm, "end": v(-22.34, 45) * mm});
            skLineSegment(sketch, "E29.3.0.251", {"start": v(-20.31, -102.5) * mm, "end": v(-22.34, -99) * mm});
            skLineSegment(sketch, "E29.3.0.252", {"start": v(-12.51, 91) * mm, "end": v(-14.54, 94.5) * mm});
            skLineSegment(sketch, "E29.3.0.253", {"start": v(-14.25, -18) * mm, "end": v(-16.27, -21.5) * mm});
            skLineSegment(sketch, "E29.3.0.254", {"start": v(-12.51, -53) * mm, "end": v(-14.54, -49.5) * mm});
            skLineSegment(sketch, "E29.3.0.255", {"start": v(-12.52, -80) * mm, "end": v(-14.54, -76.5) * mm});
            skLineSegment(sketch, "E29.3.0.256", {"start": v(-6.46, 76.5) * mm, "end": v(-8.47, 73) * mm});
            skLineSegment(sketch, "E29.3.0.257", {"start": v(-8.48, 35) * mm, "end": v(-6.46, 31.5) * mm});
            skLineSegment(sketch, "E29.3.0.258", {"start": v(-8.49, 62) * mm, "end": v(-6.46, 58.5) * mm});
            skLineSegment(sketch, "E29.3.0.259", {"start": v(-16.27, 30.5) * mm, "end": v(-14.25, 27) * mm});
            skLineSegment(sketch, "E29.3.0.260", {"start": v(-14.25, -99) * mm, "end": v(-16.27, -102.5) * mm});
            skLineSegment(sketch, "E29.3.0.261", {"start": v(-16.27, -14.5) * mm, "end": v(-14.25, -18) * mm});
            skLineSegment(sketch, "E29.3.0.262", {"start": v(-16.27, 93.5) * mm, "end": v(-14.25, 90) * mm});
            skLineSegment(sketch, "E29.3.0.263", {"start": v(-22.34, 9) * mm, "end": v(-20.31, 12.5) * mm});
            skLineSegment(sketch, "E29.3.0.264", {"start": v(-6.46, 67.5) * mm, "end": v(-8.48, 64) * mm});
            skLineSegment(sketch, "E29.3.0.265", {"start": v(-12.52, -62) * mm, "end": v(-14.54, -58.5) * mm});
            skLineSegment(sketch, "E29.3.0.266", {"start": v(-20.31, 68.5) * mm, "end": v(-22.34, 72) * mm});
            skLineSegment(sketch, "E29.3.0.267", {"start": v(-12.51, -17) * mm, "end": v(-14.54, -13.5) * mm});
            skLineSegment(sketch, "E29.3.0.268", {"start": v(-6.46, 4.5) * mm, "end": v(-8.47, 1) * mm});
            skLineSegment(sketch, "E29.3.0.269", {"start": v(-8.49, 80) * mm, "end": v(-6.46, 76.5) * mm});
            skLineSegment(sketch, "E29.3.0.270", {"start": v(-14.25, -27) * mm, "end": v(-16.27, -30.5) * mm});
            skLineSegment(sketch, "E29.3.0.271", {"start": v(-6.46, 13.5) * mm, "end": v(-8.48, 10) * mm});
            skLineSegment(sketch, "E29.3.0.272", {"start": v(-20.31, 32.5) * mm, "end": v(-22.34, 36) * mm});
            skLineSegment(sketch, "E29.3.0.273", {"start": v(-14.25, -72) * mm, "end": v(-16.27, -75.5) * mm});
            skLineSegment(sketch, "E29.3.0.274", {"start": v(-16.27, 39.5) * mm, "end": v(-14.25, 36) * mm});
            skLineSegment(sketch, "E29.3.0.275", {"start": v(-16.27, 102.5) * mm, "end": v(-14.25, 99) * mm});
            skLineSegment(sketch, "E29.3.0.276", {"start": v(-14.25, 54) * mm, "end": v(-16.27, 50.5) * mm});
            skLineSegment(sketch, "E29.3.0.277", {"start": v(-14.25, 81) * mm, "end": v(-16.27, 77.5) * mm});
            skLineSegment(sketch, "E29.3.0.278", {"start": v(-14.25, 0) * mm, "end": v(-16.27, -3.5) * mm});
            skLineSegment(sketch, "E29.3.0.279", {"start": v(-22.34, 63) * mm, "end": v(-20.31, 66.5) * mm});
            skLineSegment(sketch, "E29.3.0.280", {"start": v(-16.27, 66.5) * mm, "end": v(-14.25, 63) * mm});
            skLineSegment(sketch, "E29.3.0.281", {"start": v(-16.27, -5.5) * mm, "end": v(-14.25, -9) * mm});
            skLineSegment(sketch, "E29.3.0.282", {"start": v(-20.31, -75.5) * mm, "end": v(-22.34, -72) * mm});
            skLineSegment(sketch, "E29.3.0.283", {"start": v(-12.52, -26) * mm, "end": v(-14.54, -22.5) * mm});
            skLineSegment(sketch, "E29.3.0.284", {"start": v(-8.48, 17) * mm, "end": v(-6.46, 13.5) * mm});
            skLineSegment(sketch, "E29.3.0.285", {"start": v(-16.27, 21.5) * mm, "end": v(-14.25, 18) * mm});
            skLineSegment(sketch, "E29.3.0.286", {"start": v(-6.46, -13.5) * mm, "end": v(-8.47, -17) * mm});
            skLineSegment(sketch, "E29.3.0.287", {"start": v(-6.46, -58.5) * mm, "end": v(-8.48, -62) * mm});
            skLineSegment(sketch, "E29.3.0.288", {"start": v(-6.46, 58.5) * mm, "end": v(-8.47, 55) * mm});
            skLineSegment(sketch, "E29.3.0.289", {"start": v(-8.48, 89) * mm, "end": v(-6.46, 85.5) * mm});
            skLineSegment(sketch, "E29.3.0.290", {"start": v(-6.46, 22.5) * mm, "end": v(-8.47, 19) * mm});
            skLineSegment(sketch, "E29.3.0.291", {"start": v(-20.31, -93.5) * mm, "end": v(-22.34, -90) * mm});
            skLineSegment(sketch, "E29.3.0.292", {"start": v(-20.31, -3.5) * mm, "end": v(-22.34, 0) * mm});
            skLineSegment(sketch, "E29.3.0.293", {"start": v(-14.25, 18) * mm, "end": v(-16.27, 14.5) * mm});
            skLineSegment(sketch, "E29.3.0.294", {"start": v(-14.25, 36) * mm, "end": v(-16.27, 32.5) * mm});
            skLineSegment(sketch, "E29.3.0.295", {"start": v(-8.48, -1) * mm, "end": v(-6.46, -4.5) * mm});
            skLineSegment(sketch, "E29.3.0.296", {"start": v(-6.46, -49.5) * mm, "end": v(-8.47, -53) * mm});
            skLineSegment(sketch, "E29.3.0.297", {"start": v(-14.25, -45) * mm, "end": v(-16.27, -48.5) * mm});
            skLineSegment(sketch, "E29.3.0.298", {"start": v(-14.25, 27) * mm, "end": v(-16.27, 23.5) * mm});
            skLineSegment(sketch, "E29.3.0.299", {"start": v(-6.46, 85.5) * mm, "end": v(-8.48, 82) * mm});
            skLineSegment(sketch, "E29.3.0.300", {"start": v(-20.31, 95.5) * mm, "end": v(-22.34, 99) * mm});
            skLineSegment(sketch, "E29.3.0.301", {"start": v(-14.25, -36) * mm, "end": v(-16.27, -39.5) * mm});
            skLineSegment(sketch, "E29.3.0.302", {"start": v(-22.34, 27) * mm, "end": v(-20.31, 30.5) * mm});
            skLineSegment(sketch, "E29.3.0.303", {"start": v(-6.46, -40.5) * mm, "end": v(-8.48, -44) * mm});
            skLineSegment(sketch, "E29.3.0.304", {"start": v(-14.54, 85.5) * mm, "end": v(-12.52, 89) * mm});
            skLineSegment(sketch, "E29.3.0.305", {"start": v(-20.31, 50.5) * mm, "end": v(-22.34, 54) * mm});
            skLineSegment(sketch, "E29.3.0.306", {"start": v(-14.54, -22.5) * mm, "end": v(-12.52, -19) * mm});
            skLineSegment(sketch, "E29.3.0.307", {"start": v(-12.52, -44) * mm, "end": v(-14.54, -40.5) * mm});
            skLineSegment(sketch, "E29.3.0.308", {"start": v(-12.51, -89) * mm, "end": v(-14.54, -85.5) * mm});
            skLineSegment(sketch, "E29.3.0.309", {"start": v(-14.54, 31.5) * mm, "end": v(-12.52, 35) * mm});
            skLineSegment(sketch, "E29.3.0.310", {"start": v(-22.34, 36) * mm, "end": v(-20.31, 39.5) * mm});
            skLineSegment(sketch, "E29.3.0.311", {"start": v(-20.31, -30.5) * mm, "end": v(-22.34, -27) * mm});
            skLineSegment(sketch, "E29.3.0.312", {"start": v(-22.34, -9) * mm, "end": v(-20.31, -5.5) * mm});
            skLineSegment(sketch, "E29.3.0.313", {"start": v(-12.51, 19) * mm, "end": v(-14.54, 22.5) * mm});
            skLineSegment(sketch, "E29.3.0.314", {"start": v(-12.52, -98) * mm, "end": v(-14.54, -94.5) * mm});
            skLineSegment(sketch, "E29.3.0.315", {"start": v(-20.31, 77.5) * mm, "end": v(-22.34, 81) * mm});
            skLineSegment(sketch, "E29.3.0.316", {"start": v(-14.25, -81) * mm, "end": v(-16.27, -84.5) * mm});
            skLineSegment(sketch, "E29.3.0.317", {"start": v(-8.49, 44) * mm, "end": v(-6.46, 40.5) * mm});
            skLineSegment(sketch, "E29.3.0.318", {"start": v(-14.54, -13.5) * mm, "end": v(-12.53, -10) * mm});
            skLineSegment(sketch, "E29.3.0.319", {"start": v(-8.48, 53) * mm, "end": v(-6.46, 49.5) * mm});
            skLineSegment(sketch, "E29.3.0.320", {"start": v(-12.51, 1) * mm, "end": v(-14.54, 4.5) * mm});
            skLineSegment(sketch, "E29.3.0.321", {"start": v(-22.34, -18) * mm, "end": v(-20.31, -14.5) * mm});
            skLineSegment(sketch, "E29.3.0.322", {"start": v(-12.51, 73) * mm, "end": v(-14.54, 76.5) * mm});
            skLineSegment(sketch, "E29.3.0.323", {"start": v(-12.52, 10) * mm, "end": v(-14.54, 13.5) * mm});
            skLineSegment(sketch, "E29.3.0.324", {"start": v(-14.54, 67.5) * mm, "end": v(-12.52, 71) * mm});
            skLineSegment(sketch, "E29.3.0.325", {"start": v(-12.52, 46) * mm, "end": v(-14.54, 49.5) * mm});
            skLineSegment(sketch, "E29.3.0.326", {"start": v(-20.31, 59.5) * mm, "end": v(-22.34, 63) * mm});
            skLineSegment(sketch, "E29.3.0.327", {"start": v(-14.25, 9) * mm, "end": v(-16.27, 5.5) * mm});
            skLineSegment(sketch, "E29.3.0.328", {"start": v(-16.27, 12.5) * mm, "end": v(-14.25, 9) * mm});
            skLineSegment(sketch, "E29.3.0.329", {"start": v(-20.31, -21.5) * mm, "end": v(-22.34, -18) * mm});
            skLineSegment(sketch, "E29.3.0.330", {"start": v(-12.52, 28) * mm, "end": v(-14.54, 31.5) * mm});
            skLineSegment(sketch, "E29.3.0.331", {"start": v(-6.46, 49.5) * mm, "end": v(-8.48, 46) * mm});
            skLineSegment(sketch, "E29.3.0.332", {"start": v(-14.54, 58.5) * mm, "end": v(-12.53, 62) * mm});
            skLineSegment(sketch, "E29.3.0.333", {"start": v(-16.27, 48.5) * mm, "end": v(-14.25, 45) * mm});
            skLineSegment(sketch, "E29.3.0.334", {"start": v(-8.48, -19) * mm, "end": v(-6.46, -22.5) * mm});
            skLineSegment(sketch, "E29.3.0.335", {"start": v(-20.31, 14.5) * mm, "end": v(-22.34, 18) * mm});
            skLineSegment(sketch, "E29.3.0.336", {"start": v(-12.51, -71) * mm, "end": v(-14.54, -67.5) * mm});
            skLineSegment(sketch, "E29.3.0.337", {"start": v(-14.54, 94.5) * mm, "end": v(-12.53, 98) * mm});
            skLineSegment(sketch, "E29.3.0.338", {"start": v(-20.31, -12.5) * mm, "end": v(-22.34, -9) * mm});
            skLineSegment(sketch, "E29.3.0.339", {"start": v(-14.54, 22.5) * mm, "end": v(-12.53, 26) * mm});
            skCircle(sketch, "E29.4.0.0", {"center": v(-33.3, 0) * mm, "radius": 3.5 * mm, "construction": true});
            skLineSegment(sketch, "E29.4.0.1", {"start": v(-27.53, -46) * mm, "end": v(-23.49, -46) * mm});
            skCircle(sketch, "E29.4.0.2", {"center": v(-33.3, -63) * mm, "radius": 3.5 * mm, "construction": true});
            skPoint(sketch, "E29.4.0.3", {"position": v(-28.53, 33.25) * mm});
            skPoint(sketch, "E29.4.0.4", {"position": v(-28.53, -11.76) * mm});
            skPoint(sketch, "E29.4.0.5", {"position": v(-28.53, 42.24) * mm});
            skCircle(sketch, "E29.4.0.6", {"center": v(-33.3, 54) * mm, "radius": 3.5 * mm, "construction": true});
            skPoint(sketch, "E29.4.0.7", {"position": v(-28.53, -29.76) * mm});
            skLineSegment(sketch, "E29.4.0.8", {"start": v(-27.52, -55) * mm, "end": v(-23.48, -55) * mm});
            skPoint(sketch, "E29.4.0.9", {"position": v(-28.53, -56.75) * mm});
            skLineSegment(sketch, "E29.4.0.10", {"start": v(-35.31, -41.5) * mm, "end": v(-31.27, -41.5) * mm});
            skCircle(sketch, "E29.4.0.11", {"center": v(-33.3, -72) * mm, "radius": 3.5 * mm, "construction": true});
            skCircle(sketch, "E29.4.0.12", {"center": v(-33.3, -36) * mm, "radius": 3.5 * mm, "construction": true});
            skCircle(sketch, "E29.4.0.13", {"center": v(-25.5, 94.5) * mm, "radius": 3.5 * mm, "construction": true});
            skPoint(sketch, "E29.4.0.14", {"position": v(-28.53, -92.75) * mm});
            skCircle(sketch, "E29.4.0.15", {"center": v(-33.3, 63) * mm, "radius": 3.5 * mm, "construction": true});
            skCircle(sketch, "E29.4.0.16", {"center": v(-33.3, -9) * mm, "radius": 3.5 * mm, "construction": true});
            skLineSegment(sketch, "E29.4.0.17", {"start": v(-35.31, -32.5) * mm, "end": v(-31.27, -32.5) * mm});
            skPoint(sketch, "E29.4.0.18", {"position": v(-28.53, -74.75) * mm});
            skCircle(sketch, "E29.4.0.19", {"center": v(-33.3, -90) * mm, "radius": 3.5 * mm, "construction": true});
            skLineSegment(sketch, "E29.4.0.20", {"start": v(-35.31, -59.5) * mm, "end": v(-31.27, -59.5) * mm});
            skCircle(sketch, "E29.4.0.21", {"center": v(-33.3, 99) * mm, "radius": 3.5 * mm, "construction": true});
            skPoint(sketch, "E29.4.0.22", {"position": v(-33.3, -95.5) * mm});
            skCircle(sketch, "E29.4.0.23", {"center": v(-33.3, -99) * mm, "radius": 3.5 * mm, "construction": true});
            skLineSegment(sketch, "E29.4.0.24", {"start": v(-35.31, -77.5) * mm, "end": v(-31.27, -77.5) * mm});
            skCircle(sketch, "E29.4.0.25", {"center": v(-25.5, 13.5) * mm, "radius": 3.5 * mm, "construction": true});
            skCircle(sketch, "E29.4.0.26", {"center": v(-33.3, -81) * mm, "radius": 3.5 * mm, "construction": true});
            skLineSegment(sketch, "E29.4.0.27", {"start": v(-27.52, -73) * mm, "end": v(-23.48, -73) * mm});
            skCircle(sketch, "E29.4.0.28", {"center": v(-33.3, 9) * mm, "radius": 3.5 * mm, "construction": true});
            skLineSegment(sketch, "E29.4.0.29", {"start": v(-27.52, -37) * mm, "end": v(-23.48, -37) * mm});
            skPoint(sketch, "E29.4.0.30", {"position": v(-28.53, 51.25) * mm});
            skCircle(sketch, "E29.4.0.31", {"center": v(-25.5, 76.5) * mm, "radius": 3.5 * mm, "construction": true});
            skCircle(sketch, "E29.4.0.32", {"center": v(-25.5, -58.5) * mm, "radius": 3.5 * mm, "construction": true});
            skCircle(sketch, "E29.4.0.33", {"center": v(-25.5, -49.5) * mm, "radius": 3.5 * mm, "construction": true});
            skPoint(sketch, "E29.4.0.34", {"position": v(-28.53, 78.24) * mm});
            skLineSegment(sketch, "E29.4.0.35", {"start": v(-35.31, -86.5) * mm, "end": v(-31.27, -86.5) * mm});
            skCircle(sketch, "E29.4.0.36", {"center": v(-25.5, -40.5) * mm, "radius": 3.5 * mm, "construction": true});
            skCircle(sketch, "E29.4.0.37", {"center": v(-25.5, -94.5) * mm, "radius": 3.5 * mm, "construction": true});
            skCircle(sketch, "E29.4.0.38", {"center": v(-25.5, -13.5) * mm, "radius": 3.5 * mm, "construction": true});
            skPoint(sketch, "E29.4.0.39", {"position": v(-28.53, 60.24) * mm});
            skPoint(sketch, "E29.4.0.40", {"position": v(-28.53, 15.25) * mm});
            skLineSegment(sketch, "E29.4.0.41", {"start": v(-35.31, -50.5) * mm, "end": v(-31.27, -50.5) * mm});
            skCircle(sketch, "E29.4.0.42", {"center": v(-25.5, -85.5) * mm, "radius": 3.5 * mm, "construction": true});
            skCircle(sketch, "E29.4.0.43", {"center": v(-25.5, 31.5) * mm, "radius": 3.5 * mm, "construction": true});
            skCircle(sketch, "E29.4.0.44", {"center": v(-33.3, 36) * mm, "radius": 3.5 * mm, "construction": true});
            skCircle(sketch, "E29.4.0.45", {"center": v(-25.5, -76.5) * mm, "radius": 3.5 * mm, "construction": true});
            skPoint(sketch, "E29.4.0.46", {"position": v(-28.53, 96.24) * mm});
            skPoint(sketch, "E29.4.0.47", {"position": v(-28.53, -2.75) * mm});
            skPoint(sketch, "E29.4.0.48", {"position": v(-28.53, -83.76) * mm});
            skCircle(sketch, "E29.4.0.49", {"center": v(-33.3, -45) * mm, "radius": 3.5 * mm, "construction": true});
            skCircle(sketch, "E29.4.0.50", {"center": v(-33.3, 45) * mm, "radius": 3.5 * mm, "construction": true});
            skPoint(sketch, "E29.4.0.51", {"position": v(-28.53, -20.75) * mm});
            skCircle(sketch, "E29.4.0.52", {"center": v(-25.5, 67.5) * mm, "radius": 3.5 * mm, "construction": true});
            skLineSegment(sketch, "E29.4.0.53", {"start": v(-27.53, -64) * mm, "end": v(-23.49, -64) * mm});
            skLineSegment(sketch, "E29.4.0.54", {"start": v(-35.31, -68.5) * mm, "end": v(-31.27, -68.5) * mm});
            skCircle(sketch, "E29.4.0.55", {"center": v(-33.3, 27) * mm, "radius": 3.5 * mm, "construction": true});
            skCircle(sketch, "E29.4.0.56", {"center": v(-25.5, -67.5) * mm, "radius": 3.5 * mm, "construction": true});
            skCircle(sketch, "E29.4.0.57", {"center": v(-33.3, -54) * mm, "radius": 3.5 * mm, "construction": true});
            skCircle(sketch, "E29.4.0.58", {"center": v(-25.5, 85.5) * mm, "radius": 3.5 * mm, "construction": true});
            skCircle(sketch, "E29.4.0.59", {"center": v(-33.3, 90) * mm, "radius": 3.5 * mm, "construction": true});
            skPoint(sketch, "E29.4.0.60", {"position": v(-28.53, -47.76) * mm});
            skCircle(sketch, "E29.4.0.61", {"center": v(-33.3, -18) * mm, "radius": 3.5 * mm, "construction": true});
            skCircle(sketch, "E29.4.0.62", {"center": v(-25.5, -31.5) * mm, "radius": 3.5 * mm, "construction": true});
            skPoint(sketch, "E29.4.0.63", {"position": v(-28.53, 24.24) * mm});
            skLineSegment(sketch, "E29.4.0.64", {"start": v(-27.53, -28) * mm, "end": v(-23.49, -28) * mm});
            skCircle(sketch, "E29.4.0.65", {"center": v(-33.3, 81) * mm, "radius": 3.5 * mm, "construction": true});
            skPoint(sketch, "E29.4.0.66", {"position": v(-28.53, 6.24) * mm});
            skPoint(sketch, "E29.4.0.67", {"position": v(-28.53, 87.25) * mm});
            skCircle(sketch, "E29.4.0.68", {"center": v(-33.3, 72) * mm, "radius": 3.5 * mm, "construction": true});
            skPoint(sketch, "E29.4.0.69", {"position": v(-28.53, 69.25) * mm});
            skLineSegment(sketch, "E29.4.0.70", {"start": v(-35.31, -23.5) * mm, "end": v(-31.27, -23.5) * mm});
            skPoint(sketch, "E29.4.0.71", {"position": v(-28.53, -38.75) * mm});
            skCircle(sketch, "E29.4.0.72", {"center": v(-25.5, 58.5) * mm, "radius": 3.5 * mm, "construction": true});
            skLineSegment(sketch, "E29.4.0.73", {"start": v(-35.31, -102.5) * mm, "end": v(-35.31, -93.5) * mm, "construction": true});
            skCircle(sketch, "E29.4.0.74", {"center": v(-33.3, 18) * mm, "radius": 3.5 * mm, "construction": true});
            skLineSegment(sketch, "E29.4.0.75", {"start": v(-27.52, -91) * mm, "end": v(-23.48, -91) * mm});
            skPoint(sketch, "E29.4.0.76", {"position": v(-28.53, -65.76) * mm});
            skCircle(sketch, "E29.4.0.77", {"center": v(-25.5, 4.5) * mm, "radius": 3.5 * mm, "construction": true});
            skCircle(sketch, "E29.4.0.78", {"center": v(-33.3, -27) * mm, "radius": 3.5 * mm, "construction": true});
            skCircle(sketch, "E29.4.0.79", {"center": v(-25.5, -22.5) * mm, "radius": 3.5 * mm, "construction": true});
            skCircle(sketch, "E29.4.0.80", {"center": v(-25.5, 40.5) * mm, "radius": 3.5 * mm, "construction": true});
            skCircle(sketch, "E29.4.0.81", {"center": v(-25.5, 49.5) * mm, "radius": 3.5 * mm, "construction": true});
            skCircle(sketch, "E29.4.0.82", {"center": v(-25.5, 22.5) * mm, "radius": 3.5 * mm, "construction": true});
            skLineSegment(sketch, "E29.4.0.83", {"start": v(-27.52, -98) * mm, "end": v(-27.52, -80) * mm, "construction": true});
            skCircle(sketch, "E29.4.0.84", {"center": v(-25.5, -4.5) * mm, "radius": 3.5 * mm, "construction": true});
            skLineSegment(sketch, "E29.4.0.85", {"start": v(-23.49, -10) * mm, "end": v(-21.46, -13.5) * mm});
            skLineSegment(sketch, "E29.4.0.86", {"start": v(-31.27, -59.5) * mm, "end": v(-29.25, -63) * mm});
            skLineSegment(sketch, "E29.4.0.87", {"start": v(-31.27, -12.5) * mm, "end": v(-35.31, -12.5) * mm});
            skLineSegment(sketch, "E29.4.0.88", {"start": v(-23.47, -17) * mm, "end": v(-27.51, -17) * mm});
            skLineSegment(sketch, "E29.4.0.89", {"start": v(-31.27, -23.5) * mm, "end": v(-29.25, -27) * mm});
            skLineSegment(sketch, "E29.4.0.90", {"start": v(-31.27, -68.5) * mm, "end": v(-29.25, -72) * mm});
            skLineSegment(sketch, "E29.4.0.91", {"start": v(-23.48, 28) * mm, "end": v(-27.52, 28) * mm});
            skLineSegment(sketch, "E29.4.0.92", {"start": v(-23.47, -89) * mm, "end": v(-27.51, -89) * mm});
            skLineSegment(sketch, "E29.4.0.93", {"start": v(-31.27, -41.5) * mm, "end": v(-29.25, -45) * mm});
            skLineSegment(sketch, "E29.4.0.94", {"start": v(-31.27, 14.5) * mm, "end": v(-35.31, 14.5) * mm});
            skLineSegment(sketch, "E29.4.0.95", {"start": v(-23.48, -8) * mm, "end": v(-27.52, -8) * mm});
            skLineSegment(sketch, "E29.4.0.96", {"start": v(-29.54, -94.5) * mm, "end": v(-27.52, -91) * mm});
            skLineSegment(sketch, "E29.4.0.97", {"start": v(-35.31, 30.5) * mm, "end": v(-31.27, 30.5) * mm});
            skLineSegment(sketch, "E29.4.0.98", {"start": v(-37.34, -63) * mm, "end": v(-35.31, -59.5) * mm});
            skLineSegment(sketch, "E29.4.0.99", {"start": v(-23.49, -28) * mm, "end": v(-21.46, -31.5) * mm});
            skLineSegment(sketch, "E29.4.0.100", {"start": v(-35.31, -14.5) * mm, "end": v(-31.27, -14.5) * mm});
            skLineSegment(sketch, "E29.4.0.101", {"start": v(-35.31, -95.5) * mm, "end": v(-31.27, -95.5) * mm});
            skLineSegment(sketch, "E29.4.0.102", {"start": v(-31.27, 77.5) * mm, "end": v(-35.31, 77.5) * mm});
            skLineSegment(sketch, "E29.4.0.103", {"start": v(-31.27, -95.5) * mm, "end": v(-29.25, -99) * mm});
            skLineSegment(sketch, "E29.4.0.104", {"start": v(-37.34, -81) * mm, "end": v(-35.31, -77.5) * mm});
            skLineSegment(sketch, "E29.4.0.105", {"start": v(-23.49, -64) * mm, "end": v(-21.46, -67.5) * mm});
            skLineSegment(sketch, "E29.4.0.106", {"start": v(-27.52, 17) * mm, "end": v(-23.48, 17) * mm});
            skLineSegment(sketch, "E29.4.0.107", {"start": v(-31.27, 32.5) * mm, "end": v(-35.31, 32.5) * mm});
            skLineSegment(sketch, "E29.4.0.108", {"start": v(-31.27, 50.5) * mm, "end": v(-35.31, 50.5) * mm});
            skLineSegment(sketch, "E29.4.0.109", {"start": v(-37.34, -45) * mm, "end": v(-35.31, -41.5) * mm});
            skLineSegment(sketch, "E29.4.0.110", {"start": v(-31.27, -21.5) * mm, "end": v(-35.31, -21.5) * mm});
            skLineSegment(sketch, "E29.4.0.111", {"start": v(-27.52, 71) * mm, "end": v(-23.48, 71) * mm});
            skLineSegment(sketch, "E29.4.0.112", {"start": v(-23.48, 10) * mm, "end": v(-27.52, 10) * mm});
            skLineSegment(sketch, "E29.4.0.113", {"start": v(-23.47, -71) * mm, "end": v(-27.51, -71) * mm});
            skLineSegment(sketch, "E29.4.0.114", {"start": v(-29.54, -40.5) * mm, "end": v(-27.52, -37) * mm});
            skLineSegment(sketch, "E29.4.0.115", {"start": v(-27.53, 80) * mm, "end": v(-23.49, 80) * mm});
            skLineSegment(sketch, "E29.4.0.116", {"start": v(-23.48, 46) * mm, "end": v(-27.52, 46) * mm});
            skLineSegment(sketch, "E29.4.0.117", {"start": v(-23.48, 82) * mm, "end": v(-27.52, 82) * mm});
            skLineSegment(sketch, "E29.4.0.118", {"start": v(-23.47, -53) * mm, "end": v(-27.51, -53) * mm});
            skLineSegment(sketch, "E29.4.0.119", {"start": v(-23.48, -26) * mm, "end": v(-27.52, -26) * mm});
            skLineSegment(sketch, "E29.4.0.120", {"start": v(-31.27, -93.5) * mm, "end": v(-35.31, -93.5) * mm});
            skLineSegment(sketch, "E29.4.0.121", {"start": v(-23.48, 64) * mm, "end": v(-27.52, 64) * mm});
            skLineSegment(sketch, "E29.4.0.122", {"start": v(-23.47, 37) * mm, "end": v(-27.51, 37) * mm});
            skLineSegment(sketch, "E29.4.0.123", {"start": v(-31.27, -75.5) * mm, "end": v(-35.31, -75.5) * mm});
            skLineSegment(sketch, "E29.4.0.124", {"start": v(-35.31, 21.5) * mm, "end": v(-31.27, 21.5) * mm});
            skLineSegment(sketch, "E29.4.0.125", {"start": v(-23.47, 91) * mm, "end": v(-27.51, 91) * mm});
            skLineSegment(sketch, "E29.4.0.126", {"start": v(-29.54, -67.5) * mm, "end": v(-27.53, -64) * mm});
            skLineSegment(sketch, "E29.4.0.127", {"start": v(-23.48, -44) * mm, "end": v(-27.52, -44) * mm});
            skLineSegment(sketch, "E29.4.0.128", {"start": v(-31.27, 41.5) * mm, "end": v(-35.31, 41.5) * mm});
            skLineSegment(sketch, "E29.4.0.129", {"start": v(-23.48, -80) * mm, "end": v(-27.52, -80) * mm});
            skLineSegment(sketch, "E29.4.0.130", {"start": v(-27.53, 98) * mm, "end": v(-23.49, 98) * mm});
            skLineSegment(sketch, "E29.4.0.131", {"start": v(-31.27, 86.5) * mm, "end": v(-35.31, 86.5) * mm});
            skLineSegment(sketch, "E29.4.0.132", {"start": v(-23.47, 73) * mm, "end": v(-27.51, 73) * mm});
            skLineSegment(sketch, "E29.4.0.133", {"start": v(-23.49, -46) * mm, "end": v(-21.46, -49.5) * mm});
            skLineSegment(sketch, "E29.4.0.134", {"start": v(-31.27, -84.5) * mm, "end": v(-35.31, -84.5) * mm});
            skLineSegment(sketch, "E29.4.0.135", {"start": v(-31.27, -30.5) * mm, "end": v(-35.31, -30.5) * mm});
            skLineSegment(sketch, "E29.4.0.136", {"start": v(-37.34, -27) * mm, "end": v(-35.31, -23.5) * mm});
            skLineSegment(sketch, "E29.4.0.137", {"start": v(-35.31, 84.5) * mm, "end": v(-31.27, 84.5) * mm});
            skLineSegment(sketch, "E29.4.0.138", {"start": v(-35.31, 75.5) * mm, "end": v(-31.27, 75.5) * mm});
            skLineSegment(sketch, "E29.4.0.139", {"start": v(-27.53, -82) * mm, "end": v(-23.49, -82) * mm});
            skLineSegment(sketch, "E29.4.0.140", {"start": v(-31.27, -66.5) * mm, "end": v(-35.31, -66.5) * mm});
            skLineSegment(sketch, "E29.4.0.141", {"start": v(-23.47, 19) * mm, "end": v(-27.51, 19) * mm});
            skLineSegment(sketch, "E29.4.0.142", {"start": v(-27.53, -10) * mm, "end": v(-23.49, -10) * mm});
            skLineSegment(sketch, "E29.4.0.143", {"start": v(-31.27, -32.5) * mm, "end": v(-29.25, -36) * mm});
            skLineSegment(sketch, "E29.4.0.144", {"start": v(-27.52, -1) * mm, "end": v(-23.48, -1) * mm});
            skLineSegment(sketch, "E29.4.0.145", {"start": v(-23.48, -98) * mm, "end": v(-27.52, -98) * mm});
            skLineSegment(sketch, "E29.4.0.146", {"start": v(-31.27, 59.5) * mm, "end": v(-35.31, 59.5) * mm});
            skLineSegment(sketch, "E29.4.0.147", {"start": v(-23.47, 1) * mm, "end": v(-27.51, 1) * mm});
            skLineSegment(sketch, "E29.4.0.148", {"start": v(-37.34, -99) * mm, "end": v(-35.31, -95.5) * mm});
            skLineSegment(sketch, "E29.4.0.149", {"start": v(-31.27, -39.5) * mm, "end": v(-35.31, -39.5) * mm});
            skLineSegment(sketch, "E29.4.0.150", {"start": v(-27.53, 26) * mm, "end": v(-23.49, 26) * mm});
            skLineSegment(sketch, "E29.4.0.151", {"start": v(-23.48, -37) * mm, "end": v(-21.46, -40.5) * mm});
            skLineSegment(sketch, "E29.4.0.152", {"start": v(-27.52, -19) * mm, "end": v(-23.48, -19) * mm});
            skLineSegment(sketch, "E29.4.0.153", {"start": v(-29.54, -85.5) * mm, "end": v(-27.53, -82) * mm});
            skLineSegment(sketch, "E29.4.0.154", {"start": v(-27.53, 44) * mm, "end": v(-23.49, 44) * mm});
            skLineSegment(sketch, "E29.4.0.155", {"start": v(-31.27, 23.5) * mm, "end": v(-35.31, 23.5) * mm});
            skLineSegment(sketch, "E29.4.0.156", {"start": v(-31.27, -3.5) * mm, "end": v(-35.31, -3.5) * mm});
            skLineSegment(sketch, "E29.4.0.157", {"start": v(-37.34, -72) * mm, "end": v(-35.31, -68.5) * mm});
            skLineSegment(sketch, "E29.4.0.158", {"start": v(-23.48, -91) * mm, "end": v(-21.46, -94.5) * mm});
            skLineSegment(sketch, "E29.4.0.159", {"start": v(-37.34, -54) * mm, "end": v(-35.31, -50.5) * mm});
            skLineSegment(sketch, "E29.4.0.160", {"start": v(-29.54, -76.5) * mm, "end": v(-27.52, -73) * mm});
            skLineSegment(sketch, "E29.4.0.161", {"start": v(-27.53, 62) * mm, "end": v(-23.49, 62) * mm});
            skLineSegment(sketch, "E29.4.0.162", {"start": v(-23.49, -82) * mm, "end": v(-21.46, -85.5) * mm});
            skLineSegment(sketch, "E29.4.0.163", {"start": v(-27.52, 53) * mm, "end": v(-23.48, 53) * mm});
            skLineSegment(sketch, "E29.4.0.164", {"start": v(-37.34, -36) * mm, "end": v(-35.31, -32.5) * mm});
            skLineSegment(sketch, "E29.4.0.165", {"start": v(-35.31, 102.5) * mm, "end": v(-31.27, 102.5) * mm});
            skLineSegment(sketch, "E29.4.0.166", {"start": v(-29.54, -58.5) * mm, "end": v(-27.52, -55) * mm});
            skLineSegment(sketch, "E29.4.0.167", {"start": v(-31.27, -48.5) * mm, "end": v(-35.31, -48.5) * mm});
            skLineSegment(sketch, "E29.4.0.168", {"start": v(-23.48, -55) * mm, "end": v(-21.46, -58.5) * mm});
            skLineSegment(sketch, "E29.4.0.169", {"start": v(-35.31, 39.5) * mm, "end": v(-31.27, 39.5) * mm});
            skLineSegment(sketch, "E29.4.0.170", {"start": v(-31.27, -57.5) * mm, "end": v(-35.31, -57.5) * mm});
            skLineSegment(sketch, "E29.4.0.171", {"start": v(-23.47, 55) * mm, "end": v(-27.51, 55) * mm});
            skLineSegment(sketch, "E29.4.0.172", {"start": v(-35.31, 48.5) * mm, "end": v(-31.27, 48.5) * mm});
            skLineSegment(sketch, "E29.4.0.173", {"start": v(-35.31, 3.5) * mm, "end": v(-31.27, 3.5) * mm});
            skLineSegment(sketch, "E29.4.0.174", {"start": v(-35.31, 12.5) * mm, "end": v(-31.27, 12.5) * mm});
            skLineSegment(sketch, "E29.4.0.175", {"start": v(-31.27, -50.5) * mm, "end": v(-29.25, -54) * mm});
            skLineSegment(sketch, "E29.4.0.176", {"start": v(-35.31, 93.5) * mm, "end": v(-31.27, 93.5) * mm});
            skLineSegment(sketch, "E29.4.0.177", {"start": v(-27.52, 89) * mm, "end": v(-23.48, 89) * mm});
            skLineSegment(sketch, "E29.4.0.178", {"start": v(-31.27, -77.5) * mm, "end": v(-29.25, -81) * mm});
            skLineSegment(sketch, "E29.4.0.179", {"start": v(-31.27, 5.5) * mm, "end": v(-35.31, 5.5) * mm});
            skLineSegment(sketch, "E29.4.0.180", {"start": v(-23.48, -73) * mm, "end": v(-21.46, -76.5) * mm});
            skLineSegment(sketch, "E29.4.0.181", {"start": v(-31.27, -102.5) * mm, "end": v(-35.31, -102.5) * mm});
            skLineSegment(sketch, "E29.4.0.182", {"start": v(-27.52, 35) * mm, "end": v(-23.48, 35) * mm});
            skLineSegment(sketch, "E29.4.0.183", {"start": v(-27.53, 8) * mm, "end": v(-23.49, 8) * mm});
            skLineSegment(sketch, "E29.4.0.184", {"start": v(-35.31, -5.5) * mm, "end": v(-31.27, -5.5) * mm});
            skLineSegment(sketch, "E29.4.0.185", {"start": v(-31.27, -86.5) * mm, "end": v(-29.25, -90) * mm});
            skLineSegment(sketch, "E29.4.0.186", {"start": v(-35.31, 57.5) * mm, "end": v(-31.27, 57.5) * mm});
            skLineSegment(sketch, "E29.4.0.187", {"start": v(-31.27, 68.5) * mm, "end": v(-35.31, 68.5) * mm});
            skLineSegment(sketch, "E29.4.0.188", {"start": v(-23.48, -62) * mm, "end": v(-27.52, -62) * mm});
            skLineSegment(sketch, "E29.4.0.189", {"start": v(-29.54, -49.5) * mm, "end": v(-27.53, -46) * mm});
            skLineSegment(sketch, "E29.4.0.190", {"start": v(-31.27, 95.5) * mm, "end": v(-35.31, 95.5) * mm});
            skLineSegment(sketch, "E29.4.0.191", {"start": v(-35.31, 66.5) * mm, "end": v(-31.27, 66.5) * mm});
            skLineSegment(sketch, "E29.4.0.192", {"start": v(-37.34, -90) * mm, "end": v(-35.31, -86.5) * mm});
            skLineSegment(sketch, "E29.4.0.193", {"start": v(-23.47, -35) * mm, "end": v(-27.51, -35) * mm});
            skLineSegment(sketch, "E29.4.0.194", {"start": v(-21.46, 40.5) * mm, "end": v(-23.47, 37) * mm});
            skLineSegment(sketch, "E29.4.0.195", {"start": v(-27.51, 55) * mm, "end": v(-29.54, 58.5) * mm});
            skLineSegment(sketch, "E29.4.0.196", {"start": v(-35.31, -84.5) * mm, "end": v(-37.34, -81) * mm});
            skLineSegment(sketch, "E29.4.0.197", {"start": v(-21.46, -31.5) * mm, "end": v(-23.47, -35) * mm});
            skLineSegment(sketch, "E29.4.0.198", {"start": v(-35.31, -66.5) * mm, "end": v(-37.34, -63) * mm});
            skLineSegment(sketch, "E29.4.0.199", {"start": v(-21.46, -67.5) * mm, "end": v(-23.47, -71) * mm});
            skLineSegment(sketch, "E29.4.0.200", {"start": v(-21.46, -4.5) * mm, "end": v(-23.48, -8) * mm});
            skLineSegment(sketch, "E29.4.0.201", {"start": v(-27.52, -8) * mm, "end": v(-29.54, -4.5) * mm});
            skLineSegment(sketch, "E29.4.0.202", {"start": v(-23.49, 98) * mm, "end": v(-21.46, 94.5) * mm});
            skLineSegment(sketch, "E29.4.0.203", {"start": v(-27.51, 37) * mm, "end": v(-29.54, 40.5) * mm});
            skLineSegment(sketch, "E29.4.0.204", {"start": v(-35.31, -39.5) * mm, "end": v(-37.34, -36) * mm});
            skLineSegment(sketch, "E29.4.0.205", {"start": v(-37.34, 72) * mm, "end": v(-35.31, 75.5) * mm});
            skLineSegment(sketch, "E29.4.0.206", {"start": v(-21.46, -94.5) * mm, "end": v(-23.48, -98) * mm});
            skLineSegment(sketch, "E29.4.0.207", {"start": v(-29.25, -63) * mm, "end": v(-31.27, -66.5) * mm});
            skLineSegment(sketch, "E29.4.0.208", {"start": v(-35.31, 86.5) * mm, "end": v(-37.34, 90) * mm});
            skLineSegment(sketch, "E29.4.0.209", {"start": v(-37.34, 81) * mm, "end": v(-35.31, 84.5) * mm});
            skLineSegment(sketch, "E29.4.0.210", {"start": v(-29.25, 72) * mm, "end": v(-31.27, 68.5) * mm});
            skLineSegment(sketch, "E29.4.0.211", {"start": v(-35.31, 23.5) * mm, "end": v(-37.34, 27) * mm});
            skLineSegment(sketch, "E29.4.0.212", {"start": v(-29.54, -31.5) * mm, "end": v(-27.53, -28) * mm});
            skLineSegment(sketch, "E29.4.0.213", {"start": v(-21.46, 31.5) * mm, "end": v(-23.48, 28) * mm});
            skLineSegment(sketch, "E29.4.0.214", {"start": v(-27.52, 82) * mm, "end": v(-29.54, 85.5) * mm});
            skLineSegment(sketch, "E29.4.0.215", {"start": v(-27.52, 64) * mm, "end": v(-29.54, 67.5) * mm});
            skLineSegment(sketch, "E29.4.0.216", {"start": v(-29.54, 13.5) * mm, "end": v(-27.52, 17) * mm});
            skLineSegment(sketch, "E29.4.0.217", {"start": v(-29.54, -4.5) * mm, "end": v(-27.52, -1) * mm});
            skLineSegment(sketch, "E29.4.0.218", {"start": v(-27.51, -35) * mm, "end": v(-29.54, -31.5) * mm});
            skLineSegment(sketch, "E29.4.0.219", {"start": v(-37.34, 18) * mm, "end": v(-35.31, 21.5) * mm});
            skLineSegment(sketch, "E29.4.0.220", {"start": v(-21.46, -85.5) * mm, "end": v(-23.47, -89) * mm});
            skLineSegment(sketch, "E29.4.0.221", {"start": v(-29.54, 76.5) * mm, "end": v(-27.53, 80) * mm});
            skLineSegment(sketch, "E29.4.0.222", {"start": v(-31.27, 84.5) * mm, "end": v(-29.25, 81) * mm});
            skLineSegment(sketch, "E29.4.0.223", {"start": v(-29.25, -9) * mm, "end": v(-31.27, -12.5) * mm});
            skLineSegment(sketch, "E29.4.0.224", {"start": v(-35.31, -57.5) * mm, "end": v(-37.34, -54) * mm});
            skLineSegment(sketch, "E29.4.0.225", {"start": v(-21.46, -22.5) * mm, "end": v(-23.48, -26) * mm});
            skLineSegment(sketch, "E29.4.0.226", {"start": v(-31.27, 3.5) * mm, "end": v(-29.25, 0) * mm});
            skLineSegment(sketch, "E29.4.0.227", {"start": v(-21.46, 94.5) * mm, "end": v(-23.47, 91) * mm});
            skLineSegment(sketch, "E29.4.0.228", {"start": v(-35.31, 5.5) * mm, "end": v(-37.34, 9) * mm});
            skLineSegment(sketch, "E29.4.0.229", {"start": v(-29.25, 90) * mm, "end": v(-31.27, 86.5) * mm});
            skLineSegment(sketch, "E29.4.0.230", {"start": v(-37.34, 45) * mm, "end": v(-35.31, 48.5) * mm});
            skLineSegment(sketch, "E29.4.0.231", {"start": v(-23.48, 71) * mm, "end": v(-21.46, 67.5) * mm});
            skLineSegment(sketch, "E29.4.0.232", {"start": v(-37.34, 0) * mm, "end": v(-35.31, 3.5) * mm});
            skLineSegment(sketch, "E29.4.0.233", {"start": v(-37.34, 54) * mm, "end": v(-35.31, 57.5) * mm});
            skLineSegment(sketch, "E29.4.0.234", {"start": v(-29.54, 4.5) * mm, "end": v(-27.53, 8) * mm});
            skLineSegment(sketch, "E29.4.0.235", {"start": v(-23.49, 26) * mm, "end": v(-21.46, 22.5) * mm});
            skLineSegment(sketch, "E29.4.0.236", {"start": v(-31.27, 75.5) * mm, "end": v(-29.25, 72) * mm});
            skLineSegment(sketch, "E29.4.0.237", {"start": v(-29.25, 99) * mm, "end": v(-31.27, 95.5) * mm});
            skLineSegment(sketch, "E29.4.0.238", {"start": v(-37.34, 90) * mm, "end": v(-35.31, 93.5) * mm});
            skLineSegment(sketch, "E29.4.0.239", {"start": v(-29.25, -90) * mm, "end": v(-31.27, -93.5) * mm});
            skLineSegment(sketch, "E29.4.0.240", {"start": v(-29.25, 45) * mm, "end": v(-31.27, 41.5) * mm});
            skLineSegment(sketch, "E29.4.0.241", {"start": v(-29.54, 49.5) * mm, "end": v(-27.52, 53) * mm});
            skLineSegment(sketch, "E29.4.0.242", {"start": v(-31.27, 57.5) * mm, "end": v(-29.25, 54) * mm});
            skLineSegment(sketch, "E29.4.0.243", {"start": v(-29.25, -54) * mm, "end": v(-31.27, -57.5) * mm});
            skLineSegment(sketch, "E29.4.0.244", {"start": v(-29.25, 63) * mm, "end": v(-31.27, 59.5) * mm});
            skLineSegment(sketch, "E29.4.0.245", {"start": v(-23.49, 8) * mm, "end": v(-21.46, 4.5) * mm});
            skLineSegment(sketch, "E29.4.0.246", {"start": v(-21.46, -76.5) * mm, "end": v(-23.48, -80) * mm});
            skLineSegment(sketch, "E29.4.0.247", {"start": v(-37.34, 99) * mm, "end": v(-35.31, 102.5) * mm});
            skLineSegment(sketch, "E29.4.0.248", {"start": v(-29.54, 40.5) * mm, "end": v(-27.53, 44) * mm});
            skLineSegment(sketch, "E29.4.0.249", {"start": v(-35.31, -48.5) * mm, "end": v(-37.34, -45) * mm});
            skLineSegment(sketch, "E29.4.0.250", {"start": v(-35.31, 41.5) * mm, "end": v(-37.34, 45) * mm});
            skLineSegment(sketch, "E29.4.0.251", {"start": v(-35.31, -102.5) * mm, "end": v(-37.34, -99) * mm});
            skLineSegment(sketch, "E29.4.0.252", {"start": v(-27.51, 91) * mm, "end": v(-29.54, 94.5) * mm});
            skLineSegment(sketch, "E29.4.0.253", {"start": v(-29.25, -18) * mm, "end": v(-31.27, -21.5) * mm});
            skLineSegment(sketch, "E29.4.0.254", {"start": v(-27.51, -53) * mm, "end": v(-29.54, -49.5) * mm});
            skLineSegment(sketch, "E29.4.0.255", {"start": v(-27.52, -80) * mm, "end": v(-29.54, -76.5) * mm});
            skLineSegment(sketch, "E29.4.0.256", {"start": v(-21.46, 76.5) * mm, "end": v(-23.47, 73) * mm});
            skLineSegment(sketch, "E29.4.0.257", {"start": v(-23.48, 35) * mm, "end": v(-21.46, 31.5) * mm});
            skLineSegment(sketch, "E29.4.0.258", {"start": v(-23.49, 62) * mm, "end": v(-21.46, 58.5) * mm});
            skLineSegment(sketch, "E29.4.0.259", {"start": v(-31.27, 30.5) * mm, "end": v(-29.25, 27) * mm});
            skLineSegment(sketch, "E29.4.0.260", {"start": v(-29.25, -99) * mm, "end": v(-31.27, -102.5) * mm});
            skLineSegment(sketch, "E29.4.0.261", {"start": v(-31.27, -14.5) * mm, "end": v(-29.25, -18) * mm});
            skLineSegment(sketch, "E29.4.0.262", {"start": v(-31.27, 93.5) * mm, "end": v(-29.25, 90) * mm});
            skLineSegment(sketch, "E29.4.0.263", {"start": v(-37.34, 9) * mm, "end": v(-35.31, 12.5) * mm});
            skLineSegment(sketch, "E29.4.0.264", {"start": v(-21.46, 67.5) * mm, "end": v(-23.48, 64) * mm});
            skLineSegment(sketch, "E29.4.0.265", {"start": v(-27.52, -62) * mm, "end": v(-29.54, -58.5) * mm});
            skLineSegment(sketch, "E29.4.0.266", {"start": v(-35.31, 68.5) * mm, "end": v(-37.34, 72) * mm});
            skLineSegment(sketch, "E29.4.0.267", {"start": v(-27.51, -17) * mm, "end": v(-29.54, -13.5) * mm});
            skLineSegment(sketch, "E29.4.0.268", {"start": v(-21.46, 4.5) * mm, "end": v(-23.47, 1) * mm});
            skLineSegment(sketch, "E29.4.0.269", {"start": v(-23.49, 80) * mm, "end": v(-21.46, 76.5) * mm});
            skLineSegment(sketch, "E29.4.0.270", {"start": v(-29.25, -27) * mm, "end": v(-31.27, -30.5) * mm});
            skLineSegment(sketch, "E29.4.0.271", {"start": v(-21.46, 13.5) * mm, "end": v(-23.48, 10) * mm});
            skLineSegment(sketch, "E29.4.0.272", {"start": v(-35.31, 32.5) * mm, "end": v(-37.34, 36) * mm});
            skLineSegment(sketch, "E29.4.0.273", {"start": v(-29.25, -72) * mm, "end": v(-31.27, -75.5) * mm});
            skLineSegment(sketch, "E29.4.0.274", {"start": v(-31.27, 39.5) * mm, "end": v(-29.25, 36) * mm});
            skLineSegment(sketch, "E29.4.0.275", {"start": v(-31.27, 102.5) * mm, "end": v(-29.25, 99) * mm});
            skLineSegment(sketch, "E29.4.0.276", {"start": v(-29.25, 54) * mm, "end": v(-31.27, 50.5) * mm});
            skLineSegment(sketch, "E29.4.0.277", {"start": v(-29.25, 81) * mm, "end": v(-31.27, 77.5) * mm});
            skLineSegment(sketch, "E29.4.0.278", {"start": v(-29.25, 0) * mm, "end": v(-31.27, -3.5) * mm});
            skLineSegment(sketch, "E29.4.0.279", {"start": v(-37.34, 63) * mm, "end": v(-35.31, 66.5) * mm});
            skLineSegment(sketch, "E29.4.0.280", {"start": v(-31.27, 66.5) * mm, "end": v(-29.25, 63) * mm});
            skLineSegment(sketch, "E29.4.0.281", {"start": v(-31.27, -5.5) * mm, "end": v(-29.25, -9) * mm});
            skLineSegment(sketch, "E29.4.0.282", {"start": v(-35.31, -75.5) * mm, "end": v(-37.34, -72) * mm});
            skLineSegment(sketch, "E29.4.0.283", {"start": v(-27.52, -26) * mm, "end": v(-29.54, -22.5) * mm});
            skLineSegment(sketch, "E29.4.0.284", {"start": v(-23.48, 17) * mm, "end": v(-21.46, 13.5) * mm});
            skLineSegment(sketch, "E29.4.0.285", {"start": v(-31.27, 21.5) * mm, "end": v(-29.25, 18) * mm});
            skLineSegment(sketch, "E29.4.0.286", {"start": v(-21.46, -13.5) * mm, "end": v(-23.47, -17) * mm});
            skLineSegment(sketch, "E29.4.0.287", {"start": v(-21.46, -58.5) * mm, "end": v(-23.48, -62) * mm});
            skLineSegment(sketch, "E29.4.0.288", {"start": v(-21.46, 58.5) * mm, "end": v(-23.47, 55) * mm});
            skLineSegment(sketch, "E29.4.0.289", {"start": v(-23.48, 89) * mm, "end": v(-21.46, 85.5) * mm});
            skLineSegment(sketch, "E29.4.0.290", {"start": v(-21.46, 22.5) * mm, "end": v(-23.47, 19) * mm});
            skLineSegment(sketch, "E29.4.0.291", {"start": v(-35.31, -93.5) * mm, "end": v(-37.34, -90) * mm});
            skLineSegment(sketch, "E29.4.0.292", {"start": v(-35.31, -3.5) * mm, "end": v(-37.34, 0) * mm});
            skLineSegment(sketch, "E29.4.0.293", {"start": v(-29.25, 18) * mm, "end": v(-31.27, 14.5) * mm});
            skLineSegment(sketch, "E29.4.0.294", {"start": v(-29.25, 36) * mm, "end": v(-31.27, 32.5) * mm});
            skLineSegment(sketch, "E29.4.0.295", {"start": v(-23.48, -1) * mm, "end": v(-21.46, -4.5) * mm});
            skLineSegment(sketch, "E29.4.0.296", {"start": v(-21.46, -49.5) * mm, "end": v(-23.47, -53) * mm});
            skLineSegment(sketch, "E29.4.0.297", {"start": v(-29.25, -45) * mm, "end": v(-31.27, -48.5) * mm});
            skLineSegment(sketch, "E29.4.0.298", {"start": v(-29.25, 27) * mm, "end": v(-31.27, 23.5) * mm});
            skLineSegment(sketch, "E29.4.0.299", {"start": v(-21.46, 85.5) * mm, "end": v(-23.48, 82) * mm});
            skLineSegment(sketch, "E29.4.0.300", {"start": v(-35.31, 95.5) * mm, "end": v(-37.34, 99) * mm});
            skLineSegment(sketch, "E29.4.0.301", {"start": v(-29.25, -36) * mm, "end": v(-31.27, -39.5) * mm});
            skLineSegment(sketch, "E29.4.0.302", {"start": v(-37.34, 27) * mm, "end": v(-35.31, 30.5) * mm});
            skLineSegment(sketch, "E29.4.0.303", {"start": v(-21.46, -40.5) * mm, "end": v(-23.48, -44) * mm});
            skLineSegment(sketch, "E29.4.0.304", {"start": v(-29.54, 85.5) * mm, "end": v(-27.52, 89) * mm});
            skLineSegment(sketch, "E29.4.0.305", {"start": v(-35.31, 50.5) * mm, "end": v(-37.34, 54) * mm});
            skLineSegment(sketch, "E29.4.0.306", {"start": v(-29.54, -22.5) * mm, "end": v(-27.52, -19) * mm});
            skLineSegment(sketch, "E29.4.0.307", {"start": v(-27.52, -44) * mm, "end": v(-29.54, -40.5) * mm});
            skLineSegment(sketch, "E29.4.0.308", {"start": v(-27.51, -89) * mm, "end": v(-29.54, -85.5) * mm});
            skLineSegment(sketch, "E29.4.0.309", {"start": v(-29.54, 31.5) * mm, "end": v(-27.52, 35) * mm});
            skLineSegment(sketch, "E29.4.0.310", {"start": v(-37.34, 36) * mm, "end": v(-35.31, 39.5) * mm});
            skLineSegment(sketch, "E29.4.0.311", {"start": v(-35.31, -30.5) * mm, "end": v(-37.34, -27) * mm});
            skLineSegment(sketch, "E29.4.0.312", {"start": v(-37.34, -9) * mm, "end": v(-35.31, -5.5) * mm});
            skLineSegment(sketch, "E29.4.0.313", {"start": v(-27.51, 19) * mm, "end": v(-29.54, 22.5) * mm});
            skLineSegment(sketch, "E29.4.0.314", {"start": v(-27.52, -98) * mm, "end": v(-29.54, -94.5) * mm});
            skLineSegment(sketch, "E29.4.0.315", {"start": v(-35.31, 77.5) * mm, "end": v(-37.34, 81) * mm});
            skLineSegment(sketch, "E29.4.0.316", {"start": v(-29.25, -81) * mm, "end": v(-31.27, -84.5) * mm});
            skLineSegment(sketch, "E29.4.0.317", {"start": v(-23.49, 44) * mm, "end": v(-21.46, 40.5) * mm});
            skLineSegment(sketch, "E29.4.0.318", {"start": v(-29.54, -13.5) * mm, "end": v(-27.53, -10) * mm});
            skLineSegment(sketch, "E29.4.0.319", {"start": v(-23.48, 53) * mm, "end": v(-21.46, 49.5) * mm});
            skLineSegment(sketch, "E29.4.0.320", {"start": v(-27.51, 1) * mm, "end": v(-29.54, 4.5) * mm});
            skLineSegment(sketch, "E29.4.0.321", {"start": v(-37.34, -18) * mm, "end": v(-35.31, -14.5) * mm});
            skLineSegment(sketch, "E29.4.0.322", {"start": v(-27.51, 73) * mm, "end": v(-29.54, 76.5) * mm});
            skLineSegment(sketch, "E29.4.0.323", {"start": v(-27.52, 10) * mm, "end": v(-29.54, 13.5) * mm});
            skLineSegment(sketch, "E29.4.0.324", {"start": v(-29.54, 67.5) * mm, "end": v(-27.52, 71) * mm});
            skLineSegment(sketch, "E29.4.0.325", {"start": v(-27.52, 46) * mm, "end": v(-29.54, 49.5) * mm});
            skLineSegment(sketch, "E29.4.0.326", {"start": v(-35.31, 59.5) * mm, "end": v(-37.34, 63) * mm});
            skLineSegment(sketch, "E29.4.0.327", {"start": v(-29.25, 9) * mm, "end": v(-31.27, 5.5) * mm});
            skLineSegment(sketch, "E29.4.0.328", {"start": v(-31.27, 12.5) * mm, "end": v(-29.25, 9) * mm});
            skLineSegment(sketch, "E29.4.0.329", {"start": v(-35.31, -21.5) * mm, "end": v(-37.34, -18) * mm});
            skLineSegment(sketch, "E29.4.0.330", {"start": v(-27.52, 28) * mm, "end": v(-29.54, 31.5) * mm});
            skLineSegment(sketch, "E29.4.0.331", {"start": v(-21.46, 49.5) * mm, "end": v(-23.48, 46) * mm});
            skLineSegment(sketch, "E29.4.0.332", {"start": v(-29.54, 58.5) * mm, "end": v(-27.53, 62) * mm});
            skLineSegment(sketch, "E29.4.0.333", {"start": v(-31.27, 48.5) * mm, "end": v(-29.25, 45) * mm});
            skLineSegment(sketch, "E29.4.0.334", {"start": v(-23.48, -19) * mm, "end": v(-21.46, -22.5) * mm});
            skLineSegment(sketch, "E29.4.0.335", {"start": v(-35.31, 14.5) * mm, "end": v(-37.34, 18) * mm});
            skLineSegment(sketch, "E29.4.0.336", {"start": v(-27.51, -71) * mm, "end": v(-29.54, -67.5) * mm});
            skLineSegment(sketch, "E29.4.0.337", {"start": v(-29.54, 94.5) * mm, "end": v(-27.53, 98) * mm});
            skLineSegment(sketch, "E29.4.0.338", {"start": v(-35.31, -12.5) * mm, "end": v(-37.34, -9) * mm});
            skLineSegment(sketch, "E29.4.0.339", {"start": v(-29.54, 22.5) * mm, "end": v(-27.53, 26) * mm});
            skLineSegment(sketch, "E29.direction1", {"start": v(24.69, -102.5) * mm, "end": v(9.69, -102.5) * mm, "construction": true});
            skPoint(sketch, "E30.4.0.14", {"position": v(-28.64, -101.55) * mm});
            skLineSegment(sketch, "E30.4.0.75", {"start": v(-27.68, -100.28) * mm, "end": v(-23.9, -100.28) * mm});
            skLineSegment(sketch, "E30.4.0.96", {"start": v(-29.7, -103.78) * mm, "end": v(-27.68, -100.28) * mm});
            skLineSegment(sketch, "E30.4.0.145", {"start": v(-23.64, -107.28) * mm, "end": v(-27.68, -107.28) * mm});
            skLineSegment(sketch, "E30.4.0.158", {"start": v(-23.9, -100.28) * mm, "end": v(-22.01, -103.56) * mm});
            skLineSegment(sketch, "E30.4.0.206", {"start": v(-22.01, -103.56) * mm, "end": v(-23.64, -107.28) * mm});
            skLineSegment(sketch, "E30.4.0.314", {"start": v(-27.68, -107.28) * mm, "end": v(-29.7, -103.78) * mm});
            skLineSegment(sketch, "E31.1.0.0", {"start": v(-7.01, -103.56) * mm, "end": v(-8.64, -107.28) * mm});
            skLineSegment(sketch, "E31.1.0.1", {"start": v(-12.68, -107.28) * mm, "end": v(-14.7, -103.78) * mm});
            skLineSegment(sketch, "E31.1.0.2", {"start": v(-8.64, -107.28) * mm, "end": v(-12.68, -107.28) * mm});
            skLineSegment(sketch, "E31.1.0.3", {"start": v(-12.68, -100.28) * mm, "end": v(-8.9, -100.28) * mm});
            skPoint(sketch, "E31.1.0.4", {"position": v(-13.64, -101.55) * mm});
            skLineSegment(sketch, "E31.1.0.5", {"start": v(-8.9, -100.28) * mm, "end": v(-7.01, -103.56) * mm});
            skLineSegment(sketch, "E31.1.0.6", {"start": v(-14.7, -103.78) * mm, "end": v(-12.68, -100.28) * mm});
            skLineSegment(sketch, "E31.2.0.0", {"start": v(7.99, -103.56) * mm, "end": v(6.36, -107.28) * mm});
            skLineSegment(sketch, "E31.2.0.1", {"start": v(2.32, -107.28) * mm, "end": v(0.3, -103.78) * mm});
            skLineSegment(sketch, "E31.2.0.2", {"start": v(6.36, -107.28) * mm, "end": v(2.32, -107.28) * mm});
            skLineSegment(sketch, "E31.2.0.3", {"start": v(2.32, -100.28) * mm, "end": v(6.1, -100.28) * mm});
            skPoint(sketch, "E31.2.0.4", {"position": v(1.36, -101.55) * mm});
            skLineSegment(sketch, "E31.2.0.5", {"start": v(6.1, -100.28) * mm, "end": v(7.99, -103.56) * mm});
            skLineSegment(sketch, "E31.2.0.6", {"start": v(0.3, -103.78) * mm, "end": v(2.32, -100.28) * mm});
            skLineSegment(sketch, "E31.3.0.0", {"start": v(22.99, -103.56) * mm, "end": v(21.36, -107.28) * mm});
            skLineSegment(sketch, "E31.3.0.1", {"start": v(17.32, -107.28) * mm, "end": v(15.3, -103.78) * mm});
            skLineSegment(sketch, "E31.3.0.2", {"start": v(21.36, -107.28) * mm, "end": v(17.32, -107.28) * mm});
            skLineSegment(sketch, "E31.3.0.3", {"start": v(17.32, -100.28) * mm, "end": v(21.1, -100.28) * mm});
            skPoint(sketch, "E31.3.0.4", {"position": v(16.36, -101.55) * mm});
            skLineSegment(sketch, "E31.3.0.5", {"start": v(21.1, -100.28) * mm, "end": v(22.99, -103.56) * mm});
            skLineSegment(sketch, "E31.3.0.6", {"start": v(15.3, -103.78) * mm, "end": v(17.32, -100.28) * mm});
            skLineSegment(sketch, "E31.direction1", {"start": v(-27.68, -107.28) * mm, "end": v(-12.68, -107.28) * mm, "construction": true});
            skLineSegment(sketch, "E32.MirrorCS", {"start": v(-29.7, 103.78) * mm, "end": v(-27.68, 100.28) * mm});
            skLineSegment(sketch, "E33.MirrorCS", {"start": v(-27.68, 100.28) * mm, "end": v(-23.9, 100.28) * mm});
            skLineSegment(sketch, "E34.MirrorCS", {"start": v(-23.9, 100.28) * mm, "end": v(-22.01, 103.56) * mm});
            skLineSegment(sketch, "E35.MirrorCS", {"start": v(-22.01, 103.56) * mm, "end": v(-23.64, 107.28) * mm});
            skLineSegment(sketch, "E36.MirrorCS", {"start": v(-27.68, 107.28) * mm, "end": v(-12.68, 107.28) * mm, "construction": true});
            skLineSegment(sketch, "E37.MirrorCS", {"start": v(-27.68, 107.28) * mm, "end": v(-29.7, 103.78) * mm});
            skLineSegment(sketch, "E38", {"start": v(-27.68, 107.28) * mm, "end": v(-23.64, 107.28) * mm});
            skLineSegment(sketch, "E39.1.0.0", {"start": v(-12.68, 107.28) * mm, "end": v(-14.7, 103.78) * mm});
            skLineSegment(sketch, "E39.1.0.1", {"start": v(-14.7, 103.78) * mm, "end": v(-12.68, 100.28) * mm});
            skLineSegment(sketch, "E39.1.0.2", {"start": v(-8.9, 100.28) * mm, "end": v(-7.01, 103.56) * mm});
            skLineSegment(sketch, "E39.1.0.3", {"start": v(-12.68, 107.28) * mm, "end": v(-8.64, 107.28) * mm});
            skLineSegment(sketch, "E39.1.0.4", {"start": v(-12.68, 100.28) * mm, "end": v(-8.9, 100.28) * mm});
            skLineSegment(sketch, "E39.1.0.5", {"start": v(-7.01, 103.56) * mm, "end": v(-8.64, 107.28) * mm});
            skLineSegment(sketch, "E39.2.0.0", {"start": v(2.32, 107.28) * mm, "end": v(0.3, 103.78) * mm});
            skLineSegment(sketch, "E39.2.0.1", {"start": v(0.3, 103.78) * mm, "end": v(2.32, 100.28) * mm});
            skLineSegment(sketch, "E39.2.0.2", {"start": v(6.1, 100.28) * mm, "end": v(7.99, 103.56) * mm});
            skLineSegment(sketch, "E39.2.0.3", {"start": v(2.32, 107.28) * mm, "end": v(6.36, 107.28) * mm});
            skLineSegment(sketch, "E39.2.0.4", {"start": v(2.32, 100.28) * mm, "end": v(6.1, 100.28) * mm});
            skLineSegment(sketch, "E39.2.0.5", {"start": v(7.99, 103.56) * mm, "end": v(6.36, 107.28) * mm});
            skLineSegment(sketch, "E39.3.0.0", {"start": v(17.32, 107.28) * mm, "end": v(15.3, 103.78) * mm});
            skLineSegment(sketch, "E39.3.0.1", {"start": v(15.3, 103.78) * mm, "end": v(17.32, 100.28) * mm});
            skLineSegment(sketch, "E39.3.0.2", {"start": v(21.1, 100.28) * mm, "end": v(22.99, 103.56) * mm});
            skLineSegment(sketch, "E39.3.0.3", {"start": v(17.32, 107.28) * mm, "end": v(21.36, 107.28) * mm});
            skLineSegment(sketch, "E39.3.0.4", {"start": v(17.32, 100.28) * mm, "end": v(21.1, 100.28) * mm});
            skLineSegment(sketch, "E39.3.0.5", {"start": v(22.99, 103.56) * mm, "end": v(21.36, 107.28) * mm});
            skLineSegment(sketch, "E39.direction1", {"start": v(-27.68, 100.28) * mm, "end": v(-12.68, 100.28) * mm, "construction": true});
            skSolve(sketch);
        }
        {
            var Q0;
            Q0 = qSketchRegion(id + "F7", true);
            extrude(context, id + "F8", {"entities" : qUnion([Q0]), "operationType" : NewBodyOperationType.REMOVE, "depth" : 10 * mm, "offsetDistance" : 25 * mm});
        }
    });
